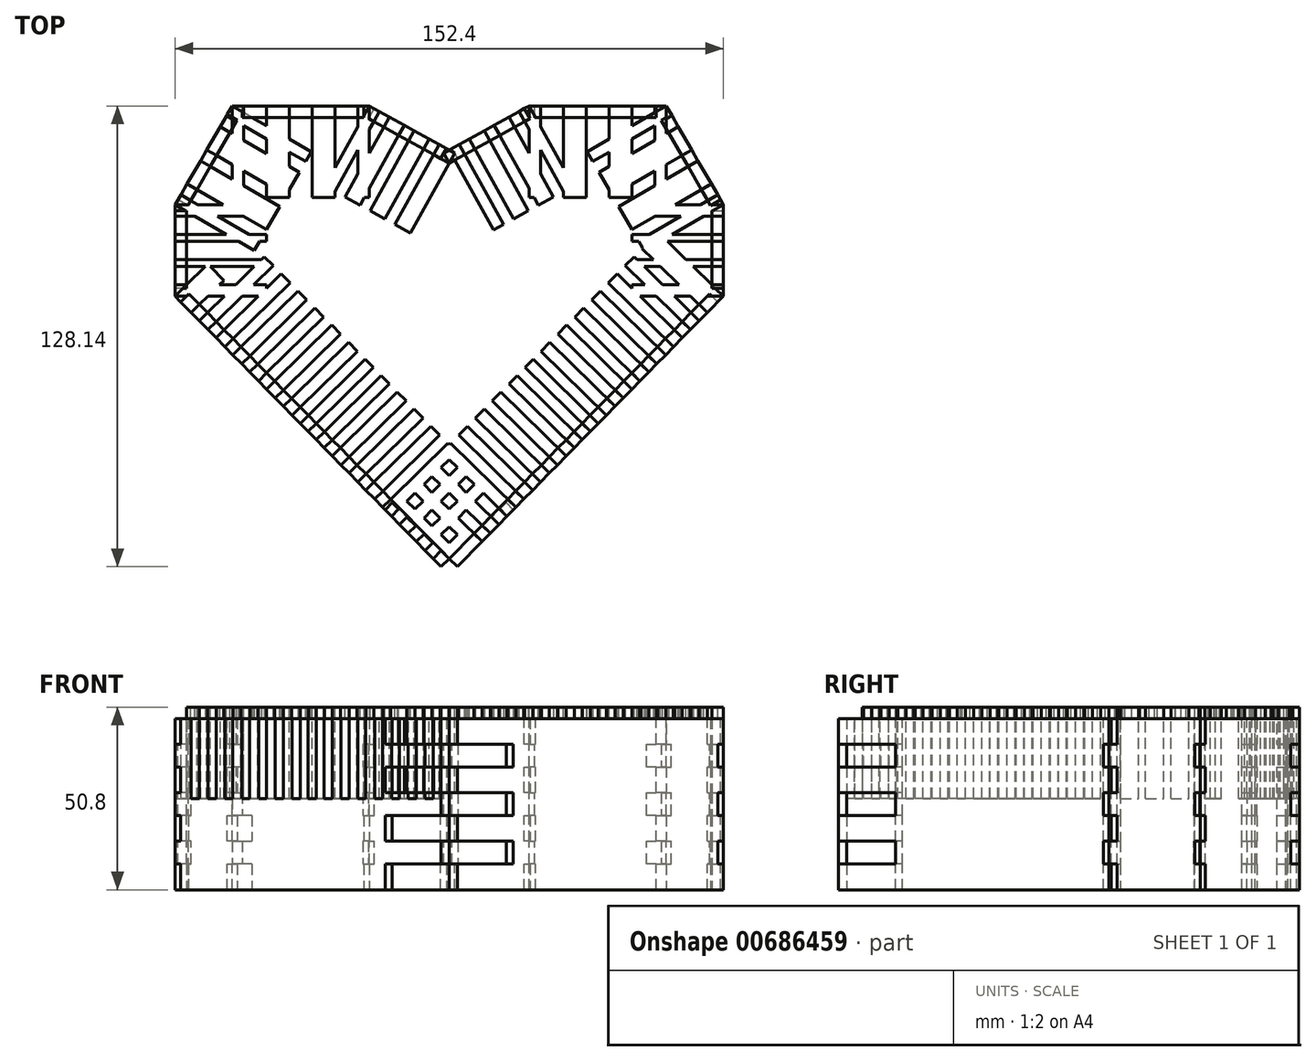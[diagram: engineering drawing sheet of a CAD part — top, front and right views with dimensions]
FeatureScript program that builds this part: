
annotation { "Feature Type Name" : "Feature", "Feature Type Description" : "" }
export const myFeature = defineFeature(function(context is Context, id is Id, definition is map)
    precondition{}
    {
        {
            var Q0;
            Q0=qCreatedBy(makeId("Top.planeOp"),FACE);
            var sketch = newSketch(context, id + "F0", { "sketchPlane" : qUnion([Q0])});
            skLineSegment(sketch, "E0", {"start": v(-76.2, 0) * mm, "end": v(0, -77.54) * mm});
            skLineSegment(sketch, "E1", {"start": v(0, -77.54) * mm, "end": v(76.2, 0) * mm});
            skLineSegment(sketch, "E2", {"start": v(76.2, 0) * mm, "end": v(76.2, 25.4) * mm});
            skLineSegment(sketch, "E3", {"start": v(76.2, 25.4) * mm, "end": v(60.32, 52.9) * mm});
            skLineSegment(sketch, "E4", {"start": v(60.32, 52.9) * mm, "end": v(22.23, 52.9) * mm});
            skLineSegment(sketch, "E5", {"start": v(22.23, 52.9) * mm, "end": v(0, 40.6) * mm});
            skLineSegment(sketch, "E6", {"start": v(0, 40.6) * mm, "end": v(-22.23, 52.9) * mm});
            skLineSegment(sketch, "E7", {"start": v(-22.23, 52.9) * mm, "end": v(-60.33, 52.9) * mm});
            skLineSegment(sketch, "E8", {"start": v(-60.32, 52.9) * mm, "end": v(-76.2, 25.4) * mm});
            skLineSegment(sketch, "E9", {"start": v(-76.2, 25.4) * mm, "end": v(-76.2, 0) * mm});
            skSolve(sketch);
        }
        {
            var Q0;
            Q0=makeQuery(id+"F0.imprint","IMPRINT",FACE,{"disambiguationData":[TD([[makeQuery(id+"F0.imprint","IMPRINT",EDGE,{"derivedFrom":sQuery(id+"F0.wireOp",EDGE,"E0")}),1.0]])]});
            extrude(context, id + "F1", {"entities" : qUnion([Q0]), "depth" : 3.17 * mm, "offsetDistance" : 25.4 * mm});
        }
        {
            var Q0;
            Q0=makeQuery(id+"F1.opExtrude","CAP_FACE",FACE,{"disambiguationData":[OSD([sQuery(id+"F0.wireOp",EDGE,"E0"),sQuery(id+"F0.wireOp",EDGE,"E1"),sQuery(id+"F0.wireOp",EDGE,"E2"),sQuery(id+"F0.wireOp",EDGE,"E3"),sQuery(id+"F0.wireOp",EDGE,"E4"),sQuery(id+"F0.wireOp",EDGE,"E5"),sQuery(id+"F0.wireOp",EDGE,"E6"),sQuery(id+"F0.wireOp",EDGE,"E7"),sQuery(id+"F0.wireOp",EDGE,"E8"),sQuery(id+"F0.wireOp",EDGE,"E9")])],"isStart":false});
            var sketch = newSketch(context, id + "F2", { "sketchPlane" : qUnion([Q0])});
            skLineSegment(sketch, "E10", {"start": v(-22.23, 52.9) * mm, "end": v(-23.76, 50.12) * mm});
            skLineSegment(sketch, "E11", {"start": v(-23.76, 50.12) * mm, "end": v(-1.54, 37.82) * mm});
            skLineSegment(sketch, "E12", {"start": v(-1.54, 37.82) * mm, "end": v(0, 40.6) * mm});
            skLineSegment(sketch, "E13", {"start": v(-76.2, 0) * mm, "end": v(-73.94, 2.23) * mm});
            skLineSegment(sketch, "E14", {"start": v(-73.94, 2.23) * mm, "end": v(2.26, -75.32) * mm});
            skLineSegment(sketch, "E15", {"start": v(2.26, -75.32) * mm, "end": v(0, -77.54) * mm});
            skLineSegment(sketch, "E16", {"start": v(76.2, 25.4) * mm, "end": v(73.03, 25.4) * mm});
            skLineSegment(sketch, "E17", {"start": v(73.03, 25.4) * mm, "end": v(73.03, 0) * mm});
            skLineSegment(sketch, "E18", {"start": v(73.03, 0) * mm, "end": v(76.2, 0) * mm});
            skLineSegment(sketch, "E19", {"start": v(-76.2, 25.4) * mm, "end": v(-73.03, 25.4) * mm});
            skLineSegment(sketch, "E20", {"start": v(-73.03, 25.4) * mm, "end": v(-73.03, 0) * mm});
            skLineSegment(sketch, "E21", {"start": v(-73.03, 0) * mm, "end": v(-76.2, 0) * mm});
            skLineSegment(sketch, "E22", {"start": v(-76.2, 25.4) * mm, "end": v(-73.45, 23.81) * mm});
            skPoint(sketch, "E22.endSnap0", {"position": v(-73.03, 12.7) * mm});
            skLineSegment(sketch, "E23", {"start": v(-73.45, 23.81) * mm, "end": v(-57.58, 51.3) * mm});
            skLineSegment(sketch, "E24", {"start": v(-57.58, 51.3) * mm, "end": v(-60.33, 52.9) * mm});
            skLineSegment(sketch, "E25", {"start": v(-60.33, 52.9) * mm, "end": v(-60.33, 49.72) * mm});
            skLineSegment(sketch, "E26", {"start": v(-60.33, 49.72) * mm, "end": v(-22.23, 49.72) * mm});
            skLineSegment(sketch, "E27", {"start": v(-22.23, 49.72) * mm, "end": v(-22.23, 52.9) * mm});
            skLineSegment(sketch, "E28", {"start": v(0, 40.6) * mm, "end": v(1.54, 37.82) * mm});
            skLineSegment(sketch, "E29", {"start": v(1.54, 37.82) * mm, "end": v(23.76, 50.12) * mm});
            skLineSegment(sketch, "E30", {"start": v(23.76, 50.12) * mm, "end": v(22.23, 52.9) * mm});
            skLineSegment(sketch, "E31", {"start": v(22.23, 52.9) * mm, "end": v(22.23, 49.72) * mm});
            skLineSegment(sketch, "E32", {"start": v(60.32, 49.72) * mm, "end": v(22.23, 49.72) * mm});
            skLineSegment(sketch, "E33", {"start": v(60.32, 49.72) * mm, "end": v(60.32, 52.9) * mm});
            skLineSegment(sketch, "E34", {"start": v(0, -77.54) * mm, "end": v(-2.26, -75.32) * mm});
            skLineSegment(sketch, "E35", {"start": v(-2.26, -75.32) * mm, "end": v(73.94, 2.23) * mm});
            skLineSegment(sketch, "E36", {"start": v(73.94, 2.23) * mm, "end": v(76.2, 0) * mm});
            skLineSegment(sketch, "E37", {"start": v(60.32, 52.9) * mm, "end": v(57.58, 51.3) * mm});
            skLineSegment(sketch, "E38", {"start": v(57.58, 51.3) * mm, "end": v(73.45, 23.81) * mm});
            skLineSegment(sketch, "E39", {"start": v(73.45, 23.81) * mm, "end": v(76.2, 25.4) * mm});
            skLineSegment(sketch, "E40", {"start": v(0, 40.6) * mm, "end": v(1.54, 39.75) * mm});
            skLineSegment(sketch, "E41", {"start": v(1.54, 39.75) * mm, "end": v(0, 36.97) * mm});
            skLineSegment(sketch, "E42", {"start": v(0, 36.97) * mm, "end": v(-1.54, 37.82) * mm});
            skLineSegment(sketch, "E43", {"start": v(1.54, 37.82) * mm, "end": v(0, 36.97) * mm});
            skLineSegment(sketch, "E44", {"start": v(0, 36.97) * mm, "end": v(-1.54, 39.75) * mm});
            skLineSegment(sketch, "E45", {"start": v(-1.54, 39.75) * mm, "end": v(0, 40.6) * mm});
            skSolve(sketch);
        }
        {
            var Q0;
            {var subQ0=sQuery(id+"F2.wireOp",EDGE,"E24");Q0=makeQuery(id+"F2.imprint","IMPRINT",FACE,{"disambiguationData":[TD([[makeQuery(id+"F2.imprint","IMPRINT",EDGE,{"derivedFrom":subQ0}),1.0]])]});}
            var Q1;
            {var subQ5=sQuery(id+"F2.wireOp",EDGE,"E10");Q1=makeQuery(id+"F2.imprint","IMPRINT",FACE,{"disambiguationData":[TD([[makeQuery(id+"F2.imprint","IMPRINT",EDGE,{"derivedFrom":subQ5}),-1.0]])]});}
            var Q2;
            {var subQ0=sQuery(id+"F2.wireOp",EDGE,"E10");Q2=makeQuery(id+"F2.imprint","IMPRINT",FACE,{"disambiguationData":[TD([[makeQuery(id+"F2.imprint","IMPRINT",EDGE,{"derivedFrom":subQ0}),1.0]])]});}
            extrude(context, id + "F3", {"entities" : qUnion([Q0, Q1, Q2]), "oppositeDirection" : true, "depth" : 50.8 * mm, "offsetDistance" : 25.4 * mm});
        }
        {
            var Q0;
            {var subQ5=sQuery(id+"F2.wireOp",EDGE,"E19");Q0=makeQuery(id+"F2.imprint","IMPRINT",FACE,{"disambiguationData":[TD([[makeQuery(id+"F2.imprint","IMPRINT",EDGE,{"derivedFrom":subQ5}),1.0]])]});}
            var Q1;
            {var subQ0=sQuery(id+"F2.wireOp",EDGE,"E19");Q1=makeQuery(id+"F2.imprint","IMPRINT",FACE,{"disambiguationData":[TD([[makeQuery(id+"F2.imprint","IMPRINT",EDGE,{"derivedFrom":subQ0}),-1.0]])]});}
            var Q2;
            {var subQ0=sQuery(id+"F2.wireOp",EDGE,"E24");Q2=makeQuery(id+"F2.imprint","IMPRINT",FACE,{"disambiguationData":[TD([[makeQuery(id+"F2.imprint","IMPRINT",EDGE,{"derivedFrom":subQ0}),1.0]])]});}
            var Q3;
            Q3=makeQuery(id+"F3.opExtrude","CAP_VERTEX",VERTEX,{"disambiguationData":[OSD([sQuery(id+"F2.wireOp",EDGE,"E25"),sQuery(id+"F2.wireOp",EDGE,"E26")])],"isStart":false});
            extrude(context, id + "F4", {"entities" : qUnion([Q0, Q1, Q2]), "endBound" : BoundingType.UP_TO_VERTEX, "oppositeDirection" : true, "depth" : 25.4 * mm, "endBoundEntityVertex" : qUnion([Q3]), "offsetDistance" : 25.4 * mm});
        }
        {
            var Q0;
            {var subQ6=sQuery(id+"F2.wireOp",EDGE,"E13");Q0=makeQuery(id+"F2.imprint","IMPRINT",FACE,{"disambiguationData":[TD([[makeQuery(id+"F2.imprint","IMPRINT",EDGE,{"derivedFrom":subQ6}),1.0]])]});}
            var Q1;
            {var subQ0=sQuery(id+"F2.wireOp",EDGE,"E13");Q1=makeQuery(id+"F2.imprint","IMPRINT",FACE,{"disambiguationData":[TD([[makeQuery(id+"F2.imprint","IMPRINT",EDGE,{"derivedFrom":subQ0}),-1.0]])]});}
            var Q2;
            {var subQ0=sQuery(id+"F2.wireOp",EDGE,"E19");Q2=makeQuery(id+"F2.imprint","IMPRINT",FACE,{"disambiguationData":[TD([[makeQuery(id+"F2.imprint","IMPRINT",EDGE,{"derivedFrom":subQ0}),-1.0]])]});}
            var Q3;
            Q3=makeQuery(id+"F4.opExtrude","CAP_VERTEX",VERTEX,{"disambiguationData":[OSD([sQuery(id+"F0.wireOp",EDGE,"E8"),sQuery(id+"F2.wireOp",EDGE,"E22")])],"isStart":false});
            extrude(context, id + "F5", {"entities" : qUnion([Q0, Q1, Q2]), "endBound" : BoundingType.UP_TO_VERTEX, "oppositeDirection" : true, "depth" : 25.4 * mm, "endBoundEntityVertex" : qUnion([Q3]), "offsetDistance" : 25.4 * mm});
        }
        {
            var Q0;
            {var subQ0=sQuery(id+"F2.wireOp",EDGE,"E21");Q0=makeQuery(id+"F2.imprint","IMPRINT",FACE,{"disambiguationData":[TD([[makeQuery(id+"F2.imprint","IMPRINT",EDGE,{"derivedFrom":subQ0}),1.0]])]});}
            var Q1;
            {var subQ0=sQuery(id+"F2.wireOp",EDGE,"E13");Q1=makeQuery(id+"F2.imprint","IMPRINT",FACE,{"disambiguationData":[TD([[makeQuery(id+"F2.imprint","IMPRINT",EDGE,{"derivedFrom":subQ0}),-1.0]])]});}
            var Q2;
            {var subQ0=sQuery(id+"F2.wireOp",EDGE,"E35");var subQ1=sQuery(id+"F2.wireOp",EDGE,"E14");var subQ2=makeQuery(id+"F2.imprint","INTERSECT",VERTEX,{"derivedFrom":[subQ1,subQ0]});Q2=makeQuery(id+"F2.imprint","IMPRINT",FACE,{"disambiguationData":[TD([[makeQuery(id+"F2.imprint","IMPRINT",EDGE,{"disambiguationData":[TD([[subQ2,-1.0]])],"derivedFrom":subQ1}),-1.0]])]});}
            var Q3;
            Q3=makeQuery(id+"F5.opExtrude","CAP_VERTEX",VERTEX,{"disambiguationData":[OSD([sQuery(id+"F0.wireOp",EDGE,"E9"),sQuery(id+"F2.wireOp",EDGE,"E21")])],"isStart":false});
            extrude(context, id + "F6", {"entities" : qUnion([Q0, Q1, Q2]), "endBound" : BoundingType.UP_TO_VERTEX, "oppositeDirection" : true, "depth" : 25.4 * mm, "endBoundEntityVertex" : qUnion([Q3]), "offsetDistance" : 25.4 * mm});
        }
        {
            var Q0;
            {var subQ0=sQuery(id+"F2.wireOp",EDGE,"E18");Q0=makeQuery(id+"F2.imprint","IMPRINT",FACE,{"disambiguationData":[TD([[makeQuery(id+"F2.imprint","IMPRINT",EDGE,{"derivedFrom":subQ0}),-1.0]])]});}
            var Q1;
            {var subQ0=sQuery(id+"F2.wireOp",EDGE,"E35");var subQ1=sQuery(id+"F2.wireOp",EDGE,"E14");var subQ2=makeQuery(id+"F2.imprint","INTERSECT",VERTEX,{"derivedFrom":[subQ1,subQ0]});Q1=makeQuery(id+"F2.imprint","IMPRINT",FACE,{"disambiguationData":[TD([[makeQuery(id+"F2.imprint","IMPRINT",EDGE,{"disambiguationData":[TD([[subQ2,-1.0]])],"derivedFrom":subQ1}),-1.0]])]});}
            var Q2;
            {var subQ0=sQuery(id+"F2.wireOp",EDGE,"E18");Q2=makeQuery(id+"F2.imprint","IMPRINT",FACE,{"disambiguationData":[TD([[makeQuery(id+"F2.imprint","IMPRINT",EDGE,{"derivedFrom":subQ0}),1.0]])]});}
            var Q3;
            Q3=makeQuery(id+"F6.opExtrude","CAP_VERTEX",VERTEX,{"disambiguationData":[OSD([sQuery(id+"F0.wireOp",EDGE,"E0"),sQuery(id+"F0.wireOp",EDGE,"E1")])],"isStart":false});
            extrude(context, id + "F7", {"entities" : qUnion([Q0, Q1, Q2]), "endBound" : BoundingType.UP_TO_VERTEX, "oppositeDirection" : true, "depth" : 25.4 * mm, "endBoundEntityVertex" : qUnion([Q3]), "offsetDistance" : 25.4 * mm});
        }
        {
            var Q0;
            {var subQ0=sQuery(id+"F2.wireOp",EDGE,"E36");Q0=makeQuery(id+"F2.imprint","IMPRINT",FACE,{"disambiguationData":[TD([[makeQuery(id+"F2.imprint","IMPRINT",EDGE,{"derivedFrom":subQ0}),1.0]])]});}
            var Q1;
            {var subQ0=sQuery(id+"F2.wireOp",EDGE,"E16");Q1=makeQuery(id+"F2.imprint","IMPRINT",FACE,{"disambiguationData":[TD([[makeQuery(id+"F2.imprint","IMPRINT",EDGE,{"derivedFrom":subQ0}),1.0]])]});}
            var Q2;
            {var subQ0=sQuery(id+"F2.wireOp",EDGE,"E18");Q2=makeQuery(id+"F2.imprint","IMPRINT",FACE,{"disambiguationData":[TD([[makeQuery(id+"F2.imprint","IMPRINT",EDGE,{"derivedFrom":subQ0}),1.0]])]});}
            var Q3;
            Q3=makeQuery(id+"F7.opExtrude","CAP_VERTEX",VERTEX,{"disambiguationData":[OSD([sQuery(id+"F2.wireOp",EDGE,"E35"),sQuery(id+"F2.wireOp",EDGE,"E36")])],"isStart":false});
            extrude(context, id + "F8", {"entities" : qUnion([Q0, Q1, Q2]), "endBound" : BoundingType.UP_TO_VERTEX, "oppositeDirection" : true, "depth" : 25.4 * mm, "endBoundEntityVertex" : qUnion([Q3]), "offsetDistance" : 25.4 * mm});
        }
        {
            var Q0;
            {var subQ2=sQuery(id+"F2.wireOp",EDGE,"E16");Q0=makeQuery(id+"F2.imprint","IMPRINT",FACE,{"disambiguationData":[TD([[makeQuery(id+"F2.imprint","IMPRINT",EDGE,{"derivedFrom":subQ2}),-1.0]])]});}
            var Q1;
            {var subQ0=sQuery(id+"F2.wireOp",EDGE,"E16");Q1=makeQuery(id+"F2.imprint","IMPRINT",FACE,{"disambiguationData":[TD([[makeQuery(id+"F2.imprint","IMPRINT",EDGE,{"derivedFrom":subQ0}),1.0]])]});}
            var Q2;
            {var subQ0=sQuery(id+"F2.wireOp",EDGE,"E33");Q2=makeQuery(id+"F2.imprint","IMPRINT",FACE,{"disambiguationData":[TD([[makeQuery(id+"F2.imprint","IMPRINT",EDGE,{"derivedFrom":subQ0}),1.0]])]});}
            var Q3;
            Q3=makeQuery(id+"F8.opExtrude","CAP_VERTEX",VERTEX,{"disambiguationData":[OSD([sQuery(id+"F2.wireOp",EDGE,"E16"),sQuery(id+"F2.wireOp",EDGE,"E17")])],"isStart":false});
            extrude(context, id + "F9", {"entities" : qUnion([Q0, Q1, Q2]), "endBound" : BoundingType.UP_TO_VERTEX, "oppositeDirection" : true, "depth" : 25.4 * mm, "endBoundEntityVertex" : qUnion([Q3]), "offsetDistance" : 25.4 * mm});
        }
        {
            var Q0;
            {var subQ6=sQuery(id+"F2.wireOp",EDGE,"E30");Q0=makeQuery(id+"F2.imprint","IMPRINT",FACE,{"disambiguationData":[TD([[makeQuery(id+"F2.imprint","IMPRINT",EDGE,{"derivedFrom":subQ6}),-1.0]])]});}
            var Q1;
            {var subQ0=sQuery(id+"F2.wireOp",EDGE,"E30");Q1=makeQuery(id+"F2.imprint","IMPRINT",FACE,{"disambiguationData":[TD([[makeQuery(id+"F2.imprint","IMPRINT",EDGE,{"derivedFrom":subQ0}),1.0]])]});}
            var Q2;
            {var subQ0=sQuery(id+"F2.wireOp",EDGE,"E33");Q2=makeQuery(id+"F2.imprint","IMPRINT",FACE,{"disambiguationData":[TD([[makeQuery(id+"F2.imprint","IMPRINT",EDGE,{"derivedFrom":subQ0}),1.0]])]});}
            var Q3;
            Q3=makeQuery(id+"F9.opExtrude","CAP_VERTEX",VERTEX,{"disambiguationData":[OSD([sQuery(id+"F0.wireOp",EDGE,"E3"),sQuery(id+"F2.wireOp",EDGE,"E37")])],"isStart":false});
            extrude(context, id + "F10", {"entities" : qUnion([Q0, Q1, Q2]), "endBound" : BoundingType.UP_TO_VERTEX, "oppositeDirection" : true, "depth" : 25.4 * mm, "endBoundEntityVertex" : qUnion([Q3]), "offsetDistance" : 25.4 * mm});
        }
        {
            var Q0;
            {var subQ4=sQuery(id+"F2.wireOp",EDGE,"E28");Q0=makeQuery(id+"F2.imprint","IMPRINT",FACE,{"disambiguationData":[TD([[makeQuery(id+"F2.imprint","IMPRINT",EDGE,{"derivedFrom":subQ4}),1.0]])]});}
            var Q1;
            {var subQ0=sQuery(id+"F2.wireOp",EDGE,"E30");Q1=makeQuery(id+"F2.imprint","IMPRINT",FACE,{"disambiguationData":[TD([[makeQuery(id+"F2.imprint","IMPRINT",EDGE,{"derivedFrom":subQ0}),1.0]])]});}
            var Q2;
            {var subQ0=sQuery(id+"F2.wireOp",EDGE,"E28");var subQ5=sQuery(id+"F2.wireOp",EDGE,"E41");var subQ7=makeQuery(id+"F2.imprint","INTERSECT",VERTEX,{"derivedFrom":[subQ0,subQ5]});Q2=makeQuery(id+"F2.imprint","IMPRINT",FACE,{"disambiguationData":[TD([[makeQuery(id+"F2.imprint","IMPRINT",EDGE,{"disambiguationData":[TD([[subQ7,-1.0]])],"derivedFrom":subQ5}),-1.0]])]});}
            var Q3;
            {var subQ0=sQuery(id+"F2.wireOp",EDGE,"E45");Q3=makeQuery(id+"F2.imprint","IMPRINT",FACE,{"disambiguationData":[TD([[makeQuery(id+"F2.imprint","IMPRINT",EDGE,{"derivedFrom":subQ0}),-1.0]])]});}
            var Q4;
            {var subQ0=sQuery(id+"F2.wireOp",EDGE,"E43");Q4=makeQuery(id+"F2.imprint","IMPRINT",FACE,{"disambiguationData":[TD([[makeQuery(id+"F2.imprint","IMPRINT",EDGE,{"derivedFrom":subQ0}),-1.0]])]});}
            var Q5;
            {var subQ1=sQuery(id+"F2.wireOp",EDGE,"E31");Q5=makeQuery(id+"F2.imprint","IMPRINT",FACE,{"disambiguationData":[TD([[makeQuery(id+"F2.imprint","IMPRINT",EDGE,{"derivedFrom":subQ1}),-1.0]])]});}
            var Q6;
            Q6=makeQuery(id+"F10.opExtrude","CAP_VERTEX",VERTEX,{"disambiguationData":[OSD([sQuery(id+"F2.wireOp",EDGE,"E31"),sQuery(id+"F2.wireOp",EDGE,"E32")])],"isStart":false});
            extrude(context, id + "F11", {"entities" : qUnion([Q0, Q1, Q2, Q3, Q4, Q5]), "endBound" : BoundingType.UP_TO_VERTEX, "oppositeDirection" : true, "depth" : 25.4 * mm, "endBoundEntityVertex" : qUnion([Q6]), "offsetDistance" : 25.4 * mm});
        }
        {
            var Q0;
            {var subQ4=sQuery(id+"F2.wireOp",EDGE,"E12");Q0=makeQuery(id+"F2.imprint","IMPRINT",FACE,{"disambiguationData":[TD([[makeQuery(id+"F2.imprint","IMPRINT",EDGE,{"derivedFrom":subQ4}),1.0]])]});}
            var Q1;
            {var subQ0=sQuery(id+"F2.wireOp",EDGE,"E10");Q1=makeQuery(id+"F2.imprint","IMPRINT",FACE,{"disambiguationData":[TD([[makeQuery(id+"F2.imprint","IMPRINT",EDGE,{"derivedFrom":subQ0}),1.0]])]});}
            var Q2;
            {var subQ0=sQuery(id+"F2.wireOp",EDGE,"E27");Q2=makeQuery(id+"F2.imprint","IMPRINT",FACE,{"disambiguationData":[TD([[makeQuery(id+"F2.imprint","IMPRINT",EDGE,{"derivedFrom":subQ0}),-1.0]])]});}
            var Q3;
            {var subQ0=sQuery(id+"F2.wireOp",EDGE,"E28");var subQ5=sQuery(id+"F2.wireOp",EDGE,"E41");var subQ7=makeQuery(id+"F2.imprint","INTERSECT",VERTEX,{"derivedFrom":[subQ0,subQ5]});Q3=makeQuery(id+"F2.imprint","IMPRINT",FACE,{"disambiguationData":[TD([[makeQuery(id+"F2.imprint","IMPRINT",EDGE,{"disambiguationData":[TD([[subQ7,-1.0]])],"derivedFrom":subQ5}),-1.0]])]});}
            var Q4;
            {var subQ0=sQuery(id+"F2.wireOp",EDGE,"E42");Q4=makeQuery(id+"F2.imprint","IMPRINT",FACE,{"disambiguationData":[TD([[makeQuery(id+"F2.imprint","IMPRINT",EDGE,{"derivedFrom":subQ0}),-1.0]])]});}
            var Q5;
            {var subQ0=sQuery(id+"F2.wireOp",EDGE,"E40");Q5=makeQuery(id+"F2.imprint","IMPRINT",FACE,{"disambiguationData":[TD([[makeQuery(id+"F2.imprint","IMPRINT",EDGE,{"derivedFrom":subQ0}),-1.0]])]});}
            var Q6;
            Q6=makeQuery(id+"F11.opExtrude","CAP_VERTEX",VERTEX,{"disambiguationData":[OSD([sQuery(id+"F0.wireOp",EDGE,"E5"),sQuery(id+"F2.wireOp",EDGE,"E44"),sQuery(id+"F2.wireOp",EDGE,"E45")])],"isStart":false});
            extrude(context, id + "F12", {"entities" : qUnion([Q0, Q1, Q2, Q3, Q4, Q5]), "endBound" : BoundingType.UP_TO_VERTEX, "oppositeDirection" : true, "depth" : 25.4 * mm, "endBoundEntityVertex" : qUnion([Q6]), "offsetDistance" : 25.4 * mm});
        }
        {
            var Q0;
            Q0=makeQuery(id+"F1.opExtrude","CAP_FACE",FACE,{"disambiguationData":[OSD([sQuery(id+"F0.wireOp",EDGE,"E0"),sQuery(id+"F0.wireOp",EDGE,"E1"),sQuery(id+"F0.wireOp",EDGE,"E2"),sQuery(id+"F0.wireOp",EDGE,"E3"),sQuery(id+"F0.wireOp",EDGE,"E4"),sQuery(id+"F0.wireOp",EDGE,"E5"),sQuery(id+"F0.wireOp",EDGE,"E6"),sQuery(id+"F0.wireOp",EDGE,"E7"),sQuery(id+"F0.wireOp",EDGE,"E8"),sQuery(id+"F0.wireOp",EDGE,"E9")])],"isStart":false});
            var sketch = newSketch(context, id + "F13", { "sketchPlane" : qUnion([Q0])});
            skCircle(sketch, "E46", {"center": v(-22.23, 52.9) * mm, "radius": 3.18 * mm});
            skCircle(sketch, "E47", {"center": v(0, 40.6) * mm, "radius": 3.18 * mm});
            skLineSegment(sketch, "E48", {"start": v(-19.45, 51.36) * mm, "end": v(-20.98, 48.58) * mm});
            skLineSegment(sketch, "E49", {"start": v(-20.98, 48.58) * mm, "end": v(-18.2, 47.04) * mm});
            skLineSegment(sketch, "E50", {"start": v(-18.2, 47.04) * mm, "end": v(-16.67, 49.82) * mm});
            skLineSegment(sketch, "E51", {"start": v(-12.5, 47.52) * mm, "end": v(-14.04, 44.74) * mm});
            skLineSegment(sketch, "E52", {"start": v(-14.04, 44.74) * mm, "end": v(-11.26, 43.2) * mm});
            skLineSegment(sketch, "E53", {"start": v(-11.26, 43.2) * mm, "end": v(-9.72, 45.98) * mm});
            skLineSegment(sketch, "E54", {"start": v(-5.56, 43.67) * mm, "end": v(-7.1, 40.9) * mm});
            skLineSegment(sketch, "E55", {"start": v(-7.1, 40.9) * mm, "end": v(-4.32, 39.36) * mm});
            skLineSegment(sketch, "E56", {"start": v(-4.32, 39.36) * mm, "end": v(-2.78, 42.14) * mm});
            skLineSegment(sketch, "E57", {"start": v(-17.44, 48.43) * mm, "end": v(-13.27, 46.13) * mm, "construction": true});
            skLineSegment(sketch, "E58", {"start": v(-10.5, 44.6) * mm, "end": v(-6.32, 42.28) * mm, "construction": true});
            skSolve(sketch);
        }
        {
            var Q0;
            {var subQ0=sQuery(id+"F13.wireOp",EDGE,"E48");Q0=makeQuery(id+"F13.imprint","IMPRINT",FACE,{"disambiguationData":[TD([[makeQuery(id+"F13.imprint","IMPRINT",EDGE,{"derivedFrom":subQ0}),1.0]])]});}
            var Q1;
            {var subQ0=sQuery(id+"F13.wireOp",EDGE,"E51");Q1=makeQuery(id+"F13.imprint","IMPRINT",FACE,{"disambiguationData":[TD([[makeQuery(id+"F13.imprint","IMPRINT",EDGE,{"derivedFrom":subQ0}),1.0]])]});}
            var Q2;
            {var subQ0=sQuery(id+"F13.wireOp",EDGE,"E54");Q2=makeQuery(id+"F13.imprint","IMPRINT",FACE,{"disambiguationData":[TD([[makeQuery(id+"F13.imprint","IMPRINT",EDGE,{"derivedFrom":subQ0}),1.0]])]});}
            extrude(context, id + "F14", {"entities" : qUnion([Q0, Q1, Q2]), "operationType" : NewBodyOperationType.REMOVE, "oppositeDirection" : true, "depth" : 25.4 * mm, "offsetDistance" : 25.4 * mm});
        }
        {
            var Q0;
            Q0=makeQuery(id+"F1.opExtrude","CAP_FACE",FACE,{"disambiguationData":[OSD([sQuery(id+"F0.wireOp",EDGE,"E0"),sQuery(id+"F0.wireOp",EDGE,"E1"),sQuery(id+"F0.wireOp",EDGE,"E2"),sQuery(id+"F0.wireOp",EDGE,"E3"),sQuery(id+"F0.wireOp",EDGE,"E4"),sQuery(id+"F0.wireOp",EDGE,"E5"),sQuery(id+"F0.wireOp",EDGE,"E6"),sQuery(id+"F0.wireOp",EDGE,"E7"),sQuery(id+"F0.wireOp",EDGE,"E8"),sQuery(id+"F0.wireOp",EDGE,"E9")])],"isStart":false});
            var sketch = newSketch(context, id + "F15", { "sketchPlane" : qUnion([Q0])});
            skCircle(sketch, "E59", {"center": v(-60.33, 52.9) * mm, "radius": 3.18 * mm});
            skCircle(sketch, "E60", {"center": v(-22.23, 52.9) * mm, "radius": 3.18 * mm});
            skLineSegment(sketch, "E61", {"start": v(-57.15, 52.9) * mm, "end": v(-57.15, 49.72) * mm});
            skLineSegment(sketch, "E62", {"start": v(-57.15, 49.72) * mm, "end": v(-50.8, 49.72) * mm});
            skLineSegment(sketch, "E63", {"start": v(-50.8, 49.72) * mm, "end": v(-50.8, 52.9) * mm});
            skLineSegment(sketch, "E64", {"start": v(-44.45, 52.9) * mm, "end": v(-44.45, 49.72) * mm});
            skLineSegment(sketch, "E65", {"start": v(-44.45, 49.72) * mm, "end": v(-38.1, 49.72) * mm});
            skLineSegment(sketch, "E66", {"start": v(-38.1, 49.72) * mm, "end": v(-38.1, 52.9) * mm});
            skLineSegment(sketch, "E67", {"start": v(-31.75, 52.9) * mm, "end": v(-31.75, 49.72) * mm});
            skLineSegment(sketch, "E68", {"start": v(-31.75, 49.72) * mm, "end": v(-25.4, 49.72) * mm});
            skLineSegment(sketch, "E69", {"start": v(-25.4, 49.72) * mm, "end": v(-25.4, 52.9) * mm});
            skLineSegment(sketch, "E70", {"start": v(-50.8, 51.3) * mm, "end": v(-44.45, 51.3) * mm, "construction": true});
            skPoint(sketch, "E70.startSnap0", {"position": v(-50.8, 51.3) * mm});
            skLineSegment(sketch, "E71", {"start": v(-38.1, 51.3) * mm, "end": v(-31.75, 51.3) * mm, "construction": true});
            skSolve(sketch);
        }
        {
            var Q0;
            {var subQ0=sQuery(id+"F15.wireOp",EDGE,"E61");Q0=makeQuery(id+"F15.imprint","IMPRINT",FACE,{"disambiguationData":[TD([[makeQuery(id+"F15.imprint","IMPRINT",EDGE,{"derivedFrom":subQ0}),1.0]])]});}
            var Q1;
            {var subQ0=sQuery(id+"F15.wireOp",EDGE,"E64");Q1=makeQuery(id+"F15.imprint","IMPRINT",FACE,{"disambiguationData":[TD([[makeQuery(id+"F15.imprint","IMPRINT",EDGE,{"derivedFrom":subQ0}),1.0]])]});}
            var Q2;
            {var subQ0=sQuery(id+"F15.wireOp",EDGE,"E67");Q2=makeQuery(id+"F15.imprint","IMPRINT",FACE,{"disambiguationData":[TD([[makeQuery(id+"F15.imprint","IMPRINT",EDGE,{"derivedFrom":subQ0}),1.0]])]});}
            extrude(context, id + "F16", {"entities" : qUnion([Q0, Q1, Q2]), "operationType" : NewBodyOperationType.REMOVE, "oppositeDirection" : true, "depth" : 25.4 * mm, "offsetDistance" : 25.4 * mm});
        }
        {
            var Q0;
            Q0=makeQuery(id+"F1.opExtrude","CAP_FACE",FACE,{"disambiguationData":[OSD([sQuery(id+"F0.wireOp",EDGE,"E0"),sQuery(id+"F0.wireOp",EDGE,"E1"),sQuery(id+"F0.wireOp",EDGE,"E2"),sQuery(id+"F0.wireOp",EDGE,"E3"),sQuery(id+"F0.wireOp",EDGE,"E4"),sQuery(id+"F0.wireOp",EDGE,"E5"),sQuery(id+"F0.wireOp",EDGE,"E6"),sQuery(id+"F0.wireOp",EDGE,"E7"),sQuery(id+"F0.wireOp",EDGE,"E8"),sQuery(id+"F0.wireOp",EDGE,"E9")])],"isStart":false});
            var sketch = newSketch(context, id + "F17", { "sketchPlane" : qUnion([Q0])});
            skCircle(sketch, "E72", {"center": v(-76.2, 25.4) * mm, "radius": 3.18 * mm});
            skCircle(sketch, "E73", {"center": v(-60.33, 52.9) * mm, "radius": 3.18 * mm});
            skLineSegment(sketch, "E74", {"start": v(-74.61, 28.15) * mm, "end": v(-71.86, 26.56) * mm});
            skLineSegment(sketch, "E75", {"start": v(-71.86, 26.56) * mm, "end": v(-70.1, 29.6) * mm});
            skLineSegment(sketch, "E76", {"start": v(-70.1, 29.6) * mm, "end": v(-72.86, 31.19) * mm});
            skLineSegment(sketch, "E77", {"start": v(-69.14, 37.63) * mm, "end": v(-66.4, 36.04) * mm});
            skLineSegment(sketch, "E78", {"start": v(-66.4, 36.04) * mm, "end": v(-64.64, 39.08) * mm});
            skLineSegment(sketch, "E79", {"start": v(-64.64, 39.08) * mm, "end": v(-67.39, 40.67) * mm});
            skLineSegment(sketch, "E80", {"start": v(-63.67, 47.1) * mm, "end": v(-60.92, 45.52) * mm});
            skLineSegment(sketch, "E81", {"start": v(-60.92, 45.52) * mm, "end": v(-59.16, 48.56) * mm});
            skLineSegment(sketch, "E82", {"start": v(-59.16, 48.56) * mm, "end": v(-61.91, 50.15) * mm});
            skLineSegment(sketch, "E83", {"start": v(-71.48, 30.4) * mm, "end": v(-67.76, 36.83) * mm, "construction": true});
            skLineSegment(sketch, "E84", {"start": v(-66.01, 39.87) * mm, "end": v(-62.3, 46.31) * mm, "construction": true});
            skSolve(sketch);
        }
        {
            var Q0;
            {var subQ0=sQuery(id+"F17.wireOp",EDGE,"E74");Q0=makeQuery(id+"F17.imprint","IMPRINT",FACE,{"disambiguationData":[TD([[makeQuery(id+"F17.imprint","IMPRINT",EDGE,{"derivedFrom":subQ0}),1.0]])]});}
            var Q1;
            {var subQ0=sQuery(id+"F17.wireOp",EDGE,"E77");Q1=makeQuery(id+"F17.imprint","IMPRINT",FACE,{"disambiguationData":[TD([[makeQuery(id+"F17.imprint","IMPRINT",EDGE,{"derivedFrom":subQ0}),1.0]])]});}
            var Q2;
            {var subQ0=sQuery(id+"F17.wireOp",EDGE,"E80");Q2=makeQuery(id+"F17.imprint","IMPRINT",FACE,{"disambiguationData":[TD([[makeQuery(id+"F17.imprint","IMPRINT",EDGE,{"derivedFrom":subQ0}),1.0]])]});}
            extrude(context, id + "F18", {"entities" : qUnion([Q0, Q1, Q2]), "operationType" : NewBodyOperationType.REMOVE, "oppositeDirection" : true, "depth" : 25.4 * mm, "offsetDistance" : 25.4 * mm});
        }
        {
            var Q0;
            Q0=makeQuery(id+"F1.opExtrude","CAP_FACE",FACE,{"disambiguationData":[OSD([sQuery(id+"F0.wireOp",EDGE,"E0"),sQuery(id+"F0.wireOp",EDGE,"E1"),sQuery(id+"F0.wireOp",EDGE,"E2"),sQuery(id+"F0.wireOp",EDGE,"E3"),sQuery(id+"F0.wireOp",EDGE,"E4"),sQuery(id+"F0.wireOp",EDGE,"E5"),sQuery(id+"F0.wireOp",EDGE,"E6"),sQuery(id+"F0.wireOp",EDGE,"E7"),sQuery(id+"F0.wireOp",EDGE,"E8"),sQuery(id+"F0.wireOp",EDGE,"E9")])],"isStart":false});
            var sketch = newSketch(context, id + "F19", { "sketchPlane" : qUnion([Q0])});
            skCircle(sketch, "E85", {"center": v(-76.2, 25.4) * mm, "radius": 3.18 * mm});
            skCircle(sketch, "E86", {"center": v(-76.2, 0) * mm, "radius": 3.18 * mm});
            skLineSegment(sketch, "E87", {"start": v(-76.2, 3.18) * mm, "end": v(-73.03, 3.18) * mm});
            skLineSegment(sketch, "E88", {"start": v(-73.03, 3.18) * mm, "end": v(-73.03, 8.22) * mm});
            skLineSegment(sketch, "E89", {"start": v(-73.03, 8.22) * mm, "end": v(-76.2, 8.22) * mm});
            skLineSegment(sketch, "E90", {"start": v(-76.2, 10.18) * mm, "end": v(-73.03, 10.18) * mm});
            skLineSegment(sketch, "E91", {"start": v(-73.03, 10.18) * mm, "end": v(-73.03, 15.22) * mm});
            skLineSegment(sketch, "E92", {"start": v(-73.03, 15.22) * mm, "end": v(-76.2, 15.22) * mm});
            skLineSegment(sketch, "E93", {"start": v(-76.2, 17.18) * mm, "end": v(-73.03, 17.18) * mm});
            skLineSegment(sketch, "E94", {"start": v(-73.03, 17.18) * mm, "end": v(-73.03, 22.22) * mm});
            skLineSegment(sketch, "E95", {"start": v(-73.03, 22.22) * mm, "end": v(-76.2, 22.22) * mm});
            skLineSegment(sketch, "E96", {"start": v(-74.61, 8.22) * mm, "end": v(-74.61, 10.18) * mm, "construction": true});
            skLineSegment(sketch, "E97", {"start": v(-74.61, 15.22) * mm, "end": v(-74.61, 17.18) * mm, "construction": true});
            skSolve(sketch);
        }
        {
            var Q0;
            {var subQ0=sQuery(id+"F19.wireOp",EDGE,"E87");Q0=makeQuery(id+"F19.imprint","IMPRINT",FACE,{"disambiguationData":[TD([[makeQuery(id+"F19.imprint","IMPRINT",EDGE,{"derivedFrom":subQ0}),1.0]])]});}
            var Q1;
            {var subQ0=sQuery(id+"F19.wireOp",EDGE,"E90");Q1=makeQuery(id+"F19.imprint","IMPRINT",FACE,{"disambiguationData":[TD([[makeQuery(id+"F19.imprint","IMPRINT",EDGE,{"derivedFrom":subQ0}),1.0]])]});}
            var Q2;
            {var subQ0=sQuery(id+"F19.wireOp",EDGE,"E93");Q2=makeQuery(id+"F19.imprint","IMPRINT",FACE,{"disambiguationData":[TD([[makeQuery(id+"F19.imprint","IMPRINT",EDGE,{"derivedFrom":subQ0}),1.0]])]});}
            extrude(context, id + "F20", {"entities" : qUnion([Q0, Q1, Q2]), "operationType" : NewBodyOperationType.REMOVE, "oppositeDirection" : true, "depth" : 25.4 * mm, "offsetDistance" : 25.4 * mm});
        }
        {
            var Q0;
            {var subQ8=sQuery(id+"F13.wireOp",EDGE,"E48");Q0=makeQuery(id+"F13.imprint","IMPRINT",FACE,{"disambiguationData":[TD([[makeQuery(id+"F13.imprint","IMPRINT",EDGE,{"derivedFrom":subQ8}),-1.0]])]});}
            var sketch = newSketch(context, id + "F21", { "sketchPlane" : qUnion([Q0])});
            skCircle(sketch, "E98", {"center": v(-76.2, 0) * mm, "radius": 3.18 * mm});
            skCircle(sketch, "E99", {"center": v(0, -77.54) * mm, "radius": 3.18 * mm});
            skLineSegment(sketch, "E100", {"start": v(-76.2, 0) * mm, "end": v(0, -77.54) * mm});
            skLineSegment(sketch, "E101", {"start": v(-38.1, -38.77) * mm, "end": v(-24.6, -25.5) * mm, "construction": true});
            skLineSegment(sketch, "E102", {"start": v(-39.21, -37.64) * mm, "end": v(-36.95, -35.41) * mm});
            skLineSegment(sketch, "E103", {"start": v(-36.95, -35.41) * mm, "end": v(-34.72, -37.68) * mm});
            skLineSegment(sketch, "E104", {"start": v(-34.72, -37.68) * mm, "end": v(-36.99, -39.9) * mm});
            skLineSegment(sketch, "E105", {"start": v(-34.76, -42.17) * mm, "end": v(-32.5, -39.94) * mm});
            skLineSegment(sketch, "E106", {"start": v(-32.5, -39.94) * mm, "end": v(-30.27, -42.2) * mm});
            skLineSegment(sketch, "E107", {"start": v(-30.27, -42.2) * mm, "end": v(-32.54, -44.43) * mm});
            skLineSegment(sketch, "E108.1.0.0", {"start": v(-30.09, -46.93) * mm, "end": v(-27.82, -44.7) * mm});
            skLineSegment(sketch, "E108.1.0.1", {"start": v(-27.82, -44.7) * mm, "end": v(-25.6, -46.97) * mm});
            skLineSegment(sketch, "E108.1.0.2", {"start": v(-25.6, -46.97) * mm, "end": v(-27.86, -49.2) * mm});
            skLineSegment(sketch, "E108.2.0.0", {"start": v(-25.41, -51.68) * mm, "end": v(-23.15, -49.46) * mm});
            skLineSegment(sketch, "E108.2.0.1", {"start": v(-23.15, -49.46) * mm, "end": v(-20.92, -51.72) * mm});
            skLineSegment(sketch, "E108.2.0.2", {"start": v(-20.92, -51.72) * mm, "end": v(-23.18, -53.95) * mm});
            skLineSegment(sketch, "E108.direction1", {"start": v(-34.76, -42.17) * mm, "end": v(-30.09, -46.93) * mm, "construction": true});
            skLineSegment(sketch, "E109.0.3.0", {"start": v(-20.73, -56.44) * mm, "end": v(-18.47, -54.22) * mm});
            skLineSegment(sketch, "E109.3.3.0", {"start": v(-18.47, -54.22) * mm, "end": v(-16.24, -56.48) * mm});
            skLineSegment(sketch, "E109.6.3.0", {"start": v(-16.24, -56.48) * mm, "end": v(-18.5, -58.7) * mm});
            skLineSegment(sketch, "E109.0.4.0", {"start": v(-16.06, -61.2) * mm, "end": v(-13.8, -58.98) * mm});
            skLineSegment(sketch, "E109.3.4.0", {"start": v(-13.8, -58.98) * mm, "end": v(-11.57, -61.24) * mm});
            skLineSegment(sketch, "E109.6.4.0", {"start": v(-11.57, -61.24) * mm, "end": v(-13.83, -63.47) * mm});
            skLineSegment(sketch, "E109.0.5.0", {"start": v(-11.38, -65.96) * mm, "end": v(-9.12, -63.73) * mm});
            skLineSegment(sketch, "E109.3.5.0", {"start": v(-9.12, -63.73) * mm, "end": v(-6.9, -66) * mm});
            skLineSegment(sketch, "E109.6.5.0", {"start": v(-6.9, -66) * mm, "end": v(-9.16, -68.22) * mm});
            skLineSegment(sketch, "E109.0.6.0", {"start": v(-6.7, -70.72) * mm, "end": v(-4.44, -68.5) * mm});
            skLineSegment(sketch, "E109.3.6.0", {"start": v(-4.44, -68.5) * mm, "end": v(-2.22, -70.76) * mm});
            skLineSegment(sketch, "E109.6.6.0", {"start": v(-2.22, -70.76) * mm, "end": v(-4.48, -72.98) * mm});
            skLineSegment(sketch, "E110.MirrorCS", {"start": v(-41.44, -35.37) * mm, "end": v(-39.17, -33.15) * mm});
            skLineSegment(sketch, "E111.MirrorCS", {"start": v(-39.17, -33.15) * mm, "end": v(-41.4, -30.88) * mm});
            skLineSegment(sketch, "E112.MirrorCS", {"start": v(-41.4, -30.88) * mm, "end": v(-43.66, -33.1) * mm});
            skLineSegment(sketch, "E113.MirrorCS", {"start": v(-46.11, -30.62) * mm, "end": v(-43.85, -28.4) * mm});
            skLineSegment(sketch, "E114.MirrorCS", {"start": v(-43.85, -28.4) * mm, "end": v(-46.07, -26.13) * mm});
            skLineSegment(sketch, "E115.MirrorCS", {"start": v(-46.07, -26.13) * mm, "end": v(-48.34, -28.35) * mm});
            skLineSegment(sketch, "E116.MirrorCS", {"start": v(-50.79, -25.86) * mm, "end": v(-48.53, -23.63) * mm});
            skLineSegment(sketch, "E117.MirrorCS", {"start": v(-48.53, -23.63) * mm, "end": v(-50.75, -21.37) * mm});
            skLineSegment(sketch, "E118.MirrorCS", {"start": v(-50.75, -21.37) * mm, "end": v(-53.02, -23.6) * mm});
            skLineSegment(sketch, "E119.MirrorCS", {"start": v(-55.47, -21.1) * mm, "end": v(-53.2, -18.87) * mm});
            skLineSegment(sketch, "E120.MirrorCS", {"start": v(-53.2, -18.87) * mm, "end": v(-55.43, -16.6) * mm});
            skLineSegment(sketch, "E121.MirrorCS", {"start": v(-55.43, -16.6) * mm, "end": v(-57.7, -18.83) * mm});
            skLineSegment(sketch, "E122.MirrorCS", {"start": v(-60.14, -16.34) * mm, "end": v(-57.88, -14.12) * mm});
            skLineSegment(sketch, "E123.MirrorCS", {"start": v(-57.88, -14.12) * mm, "end": v(-60.1, -11.85) * mm});
            skLineSegment(sketch, "E124.MirrorCS", {"start": v(-60.1, -11.85) * mm, "end": v(-62.37, -14.08) * mm});
            skLineSegment(sketch, "E125.MirrorCS", {"start": v(-64.82, -11.58) * mm, "end": v(-62.55, -9.36) * mm});
            skLineSegment(sketch, "E126.MirrorCS", {"start": v(-62.55, -9.36) * mm, "end": v(-64.78, -7.1) * mm});
            skLineSegment(sketch, "E127.MirrorCS", {"start": v(-64.78, -7.1) * mm, "end": v(-67.04, -9.32) * mm});
            skLineSegment(sketch, "E128.MirrorCS", {"start": v(-69.5, -6.82) * mm, "end": v(-67.23, -4.6) * mm});
            skLineSegment(sketch, "E129.MirrorCS", {"start": v(-67.23, -4.6) * mm, "end": v(-69.45, -2.33) * mm});
            skLineSegment(sketch, "E130.MirrorCS", {"start": v(-69.45, -2.33) * mm, "end": v(-71.72, -4.56) * mm});
            skSolve(sketch);
        }
        {
            var Q0;
            {var subQ0=sQuery(id+"F21.wireOp",EDGE,"E128.MirrorCS");Q0=makeQuery(id+"F21.imprint","IMPRINT",FACE,{"disambiguationData":[TD([[makeQuery(id+"F21.imprint","IMPRINT",EDGE,{"derivedFrom":subQ0}),1.0]])]});}
            var Q1;
            {var subQ0=sQuery(id+"F21.wireOp",EDGE,"E125.MirrorCS");Q1=makeQuery(id+"F21.imprint","IMPRINT",FACE,{"disambiguationData":[TD([[makeQuery(id+"F21.imprint","IMPRINT",EDGE,{"derivedFrom":subQ0}),1.0]])]});}
            var Q2;
            {var subQ0=sQuery(id+"F21.wireOp",EDGE,"E122.MirrorCS");Q2=makeQuery(id+"F21.imprint","IMPRINT",FACE,{"disambiguationData":[TD([[makeQuery(id+"F21.imprint","IMPRINT",EDGE,{"derivedFrom":subQ0}),1.0]])]});}
            var Q3;
            {var subQ0=sQuery(id+"F21.wireOp",EDGE,"E119.MirrorCS");Q3=makeQuery(id+"F21.imprint","IMPRINT",FACE,{"disambiguationData":[TD([[makeQuery(id+"F21.imprint","IMPRINT",EDGE,{"derivedFrom":subQ0}),1.0]])]});}
            var Q4;
            {var subQ0=sQuery(id+"F21.wireOp",EDGE,"E116.MirrorCS");Q4=makeQuery(id+"F21.imprint","IMPRINT",FACE,{"disambiguationData":[TD([[makeQuery(id+"F21.imprint","IMPRINT",EDGE,{"derivedFrom":subQ0}),1.0]])]});}
            var Q5;
            {var subQ0=sQuery(id+"F21.wireOp",EDGE,"E113.MirrorCS");Q5=makeQuery(id+"F21.imprint","IMPRINT",FACE,{"disambiguationData":[TD([[makeQuery(id+"F21.imprint","IMPRINT",EDGE,{"derivedFrom":subQ0}),1.0]])]});}
            var Q6;
            {var subQ0=sQuery(id+"F21.wireOp",EDGE,"E110.MirrorCS");Q6=makeQuery(id+"F21.imprint","IMPRINT",FACE,{"disambiguationData":[TD([[makeQuery(id+"F21.imprint","IMPRINT",EDGE,{"derivedFrom":subQ0}),1.0]])]});}
            var Q7;
            {var subQ0=sQuery(id+"F21.wireOp",EDGE,"E102");Q7=makeQuery(id+"F21.imprint","IMPRINT",FACE,{"disambiguationData":[TD([[makeQuery(id+"F21.imprint","IMPRINT",EDGE,{"derivedFrom":subQ0}),-1.0]])]});}
            var Q8;
            {var subQ0=sQuery(id+"F21.wireOp",EDGE,"E105");Q8=makeQuery(id+"F21.imprint","IMPRINT",FACE,{"disambiguationData":[TD([[makeQuery(id+"F21.imprint","IMPRINT",EDGE,{"derivedFrom":subQ0}),-1.0]])]});}
            var Q9;
            {var subQ0=sQuery(id+"F21.wireOp",EDGE,"E108.1.0.0");Q9=makeQuery(id+"F21.imprint","IMPRINT",FACE,{"disambiguationData":[TD([[makeQuery(id+"F21.imprint","IMPRINT",EDGE,{"derivedFrom":subQ0}),-1.0]])]});}
            var Q10;
            {var subQ0=sQuery(id+"F21.wireOp",EDGE,"E108.2.0.0");Q10=makeQuery(id+"F21.imprint","IMPRINT",FACE,{"disambiguationData":[TD([[makeQuery(id+"F21.imprint","IMPRINT",EDGE,{"derivedFrom":subQ0}),-1.0]])]});}
            var Q11;
            {var subQ0=sQuery(id+"F21.wireOp",EDGE,"E109.0.3.0");Q11=makeQuery(id+"F21.imprint","IMPRINT",FACE,{"disambiguationData":[TD([[makeQuery(id+"F21.imprint","IMPRINT",EDGE,{"derivedFrom":subQ0}),-1.0]])]});}
            var Q12;
            {var subQ0=sQuery(id+"F21.wireOp",EDGE,"E109.0.4.0");Q12=makeQuery(id+"F21.imprint","IMPRINT",FACE,{"disambiguationData":[TD([[makeQuery(id+"F21.imprint","IMPRINT",EDGE,{"derivedFrom":subQ0}),-1.0]])]});}
            var Q13;
            {var subQ0=sQuery(id+"F21.wireOp",EDGE,"E109.0.5.0");Q13=makeQuery(id+"F21.imprint","IMPRINT",FACE,{"disambiguationData":[TD([[makeQuery(id+"F21.imprint","IMPRINT",EDGE,{"derivedFrom":subQ0}),-1.0]])]});}
            var Q14;
            {var subQ0=sQuery(id+"F21.wireOp",EDGE,"E109.0.6.0");Q14=makeQuery(id+"F21.imprint","IMPRINT",FACE,{"disambiguationData":[TD([[makeQuery(id+"F21.imprint","IMPRINT",EDGE,{"derivedFrom":subQ0}),-1.0]])]});}
            extrude(context, id + "F22", {"entities" : qUnion([Q0, Q1, Q2, Q3, Q4, Q5, Q6, Q7, Q8, Q9, Q10, Q11, Q12, Q13, Q14]), "operationType" : NewBodyOperationType.REMOVE, "oppositeDirection" : true, "depth" : 25.4 * mm, "offsetDistance" : 25.4 * mm});
        }
        {
            var Q0;
            Q0=makeQuery(id+"F1.opExtrude","CAP_VERTEX",VERTEX,{"disambiguationData":[OSD([sQuery(id+"F0.wireOp",EDGE,"E5"),sQuery(id+"F0.wireOp",EDGE,"E6")])],"isStart":false});
            var Q1;
            Q1=makeQuery(id+"F1.opExtrude","CAP_VERTEX",VERTEX,{"disambiguationData":[OSD([sQuery(id+"F0.wireOp",EDGE,"E0"),sQuery(id+"F0.wireOp",EDGE,"E1")])],"isStart":false});
            var Q2;
            Q2=makeQuery(id+"F1.opExtrude","CAP_VERTEX",VERTEX,{"disambiguationData":[OSD([sQuery(id+"F0.wireOp",EDGE,"E0"),sQuery(id+"F0.wireOp",EDGE,"E1")])],"isStart":true});
            cPlane(context, id + "F23", {"entities" : qUnion([Q0, Q1, Q2]), "cplaneType" : CPlaneType.THREE_POINT, "offset" : 25.4 * mm, "width" : 152.4 * mm, "height" : 152.4 * mm});
        }
        {
            var Q0;
            Q0=makeQuery(id+"F6.opExtrude","SWEPT_FACE",FACE,{"disambiguationData":[OSD([sQuery(id+"F0.wireOp",EDGE,"E0")])]});
            var sketch = newSketch(context, id + "F24", { "sketchPlane" : qUnion([Q0])});
            skLineSegment(sketch, "E131.0.0", {"start": v(48.91, 3.17) * mm, "end": v(48.91, 0) * mm});
            skLineSegment(sketch, "E131.0.1", {"start": v(48.91, 0) * mm, "end": v(55.3, 0) * mm});
            skLineSegment(sketch, "E131.0.2", {"start": v(55.3, 0) * mm, "end": v(55.3, 3.18) * mm});
            skLineSegment(sketch, "E131.0.3", {"start": v(55.3, 3.18) * mm, "end": v(48.91, 3.18) * mm});
            skPoint(sketch, "E132.0", {"position": v(43.99, 0) * mm});
            skLineSegment(sketch, "E133.0.0", {"start": v(42.24, 3.17) * mm, "end": v(42.24, 0) * mm});
            skLineSegment(sketch, "E133.0.1", {"start": v(42.24, 0) * mm, "end": v(45.74, 0) * mm});
            skLineSegment(sketch, "E133.0.2", {"start": v(45.74, 0) * mm, "end": v(45.74, 3.17) * mm});
            skLineSegment(sketch, "E133.0.3", {"start": v(45.74, 3.18) * mm, "end": v(42.24, 3.18) * mm});
            skLineSegment(sketch, "E134.0.0", {"start": v(35.57, 3.17) * mm, "end": v(35.57, 0) * mm});
            skLineSegment(sketch, "E134.0.1", {"start": v(35.57, 0) * mm, "end": v(39.07, 0) * mm});
            skLineSegment(sketch, "E134.0.2", {"start": v(39.07, 0) * mm, "end": v(39.07, 3.17) * mm});
            skLineSegment(sketch, "E134.0.3", {"start": v(39.07, 3.18) * mm, "end": v(35.57, 3.18) * mm});
            skLineSegment(sketch, "E135.0.0", {"start": v(28.9, 3.17) * mm, "end": v(28.9, 0) * mm});
            skLineSegment(sketch, "E135.0.1", {"start": v(28.9, 0) * mm, "end": v(32.4, 0) * mm});
            skLineSegment(sketch, "E135.0.2", {"start": v(32.4, 0) * mm, "end": v(32.4, 3.17) * mm});
            skLineSegment(sketch, "E135.0.3", {"start": v(32.4, 3.18) * mm, "end": v(28.9, 3.18) * mm});
            skLineSegment(sketch, "E136.0.0", {"start": v(22.23, 3.17) * mm, "end": v(22.23, 0) * mm});
            skLineSegment(sketch, "E136.0.1", {"start": v(22.23, 0) * mm, "end": v(25.72, 0) * mm});
            skLineSegment(sketch, "E136.0.2", {"start": v(25.72, 0) * mm, "end": v(25.72, 3.17) * mm});
            skLineSegment(sketch, "E136.0.3", {"start": v(25.72, 3.18) * mm, "end": v(22.23, 3.18) * mm});
            skLineSegment(sketch, "E137.0.0", {"start": v(15.56, 3.17) * mm, "end": v(15.56, 0) * mm});
            skLineSegment(sketch, "E137.0.1", {"start": v(15.56, 0) * mm, "end": v(19.05, 0) * mm});
            skLineSegment(sketch, "E137.0.2", {"start": v(19.05, 0) * mm, "end": v(19.05, 3.17) * mm});
            skLineSegment(sketch, "E137.0.3", {"start": v(19.05, 3.18) * mm, "end": v(15.56, 3.18) * mm});
            skLineSegment(sketch, "E138.0.0", {"start": v(8.89, 3.17) * mm, "end": v(8.89, 0) * mm});
            skLineSegment(sketch, "E138.0.1", {"start": v(8.89, 0) * mm, "end": v(12.38, 0) * mm});
            skLineSegment(sketch, "E138.0.2", {"start": v(12.38, 0) * mm, "end": v(12.38, 3.17) * mm});
            skLineSegment(sketch, "E138.0.3", {"start": v(12.38, 3.18) * mm, "end": v(8.89, 3.18) * mm});
            skLineSegment(sketch, "E139.0.0", {"start": v(2.54, 3.17) * mm, "end": v(2.54, 0) * mm});
            skLineSegment(sketch, "E139.0.1", {"start": v(2.54, 0) * mm, "end": v(5.71, 0) * mm});
            skLineSegment(sketch, "E139.0.2", {"start": v(5.71, 0) * mm, "end": v(5.71, 3.17) * mm});
            skLineSegment(sketch, "E139.0.3", {"start": v(5.71, 3.18) * mm, "end": v(2.54, 3.18) * mm});
            skLineSegment(sketch, "E140.0.0", {"start": v(-3.81, 3.17) * mm, "end": v(-3.81, 0) * mm});
            skLineSegment(sketch, "E140.0.1", {"start": v(-3.81, 0) * mm, "end": v(-0.64, 0) * mm});
            skLineSegment(sketch, "E140.0.2", {"start": v(-0.64, 0) * mm, "end": v(-0.64, 3.17) * mm});
            skLineSegment(sketch, "E140.0.3", {"start": v(-0.64, 3.18) * mm, "end": v(-3.81, 3.18) * mm});
            skLineSegment(sketch, "E141.0.0", {"start": v(-10.48, 3.17) * mm, "end": v(-10.48, 0) * mm});
            skLineSegment(sketch, "E141.0.1", {"start": v(-10.48, 0) * mm, "end": v(-6.99, 0) * mm});
            skLineSegment(sketch, "E141.0.2", {"start": v(-6.99, 0) * mm, "end": v(-6.99, 3.17) * mm});
            skLineSegment(sketch, "E141.0.3", {"start": v(-6.99, 3.18) * mm, "end": v(-10.48, 3.18) * mm});
            skLineSegment(sketch, "E142.0.0", {"start": v(-17.16, 3.17) * mm, "end": v(-17.16, 0) * mm});
            skLineSegment(sketch, "E142.0.1", {"start": v(-17.16, 0) * mm, "end": v(-13.66, 0) * mm});
            skLineSegment(sketch, "E142.0.2", {"start": v(-13.66, 0) * mm, "end": v(-13.66, 3.17) * mm});
            skLineSegment(sketch, "E142.0.3", {"start": v(-13.66, 3.18) * mm, "end": v(-17.16, 3.18) * mm});
            skLineSegment(sketch, "E143.0.0", {"start": v(-23.83, 3.17) * mm, "end": v(-23.83, 0) * mm});
            skLineSegment(sketch, "E143.0.1", {"start": v(-23.83, 0) * mm, "end": v(-20.33, 0) * mm});
            skLineSegment(sketch, "E143.0.2", {"start": v(-20.33, 0) * mm, "end": v(-20.33, 3.17) * mm});
            skLineSegment(sketch, "E143.0.3", {"start": v(-20.33, 3.18) * mm, "end": v(-23.83, 3.18) * mm});
            skLineSegment(sketch, "E144.0.0", {"start": v(-43.84, 3.17) * mm, "end": v(-43.84, 0) * mm});
            skLineSegment(sketch, "E144.0.1", {"start": v(-43.84, 0) * mm, "end": v(-40.34, 0) * mm});
            skLineSegment(sketch, "E144.0.2", {"start": v(-40.34, 0) * mm, "end": v(-40.34, 3.17) * mm});
            skLineSegment(sketch, "E144.0.3", {"start": v(-40.34, 3.18) * mm, "end": v(-43.84, 3.18) * mm});
            skLineSegment(sketch, "E145.0.0", {"start": v(-37.17, 3.17) * mm, "end": v(-37.17, 0) * mm});
            skLineSegment(sketch, "E145.0.1", {"start": v(-37.17, 0) * mm, "end": v(-33.67, 0) * mm});
            skLineSegment(sketch, "E145.0.2", {"start": v(-33.67, 0) * mm, "end": v(-33.67, 3.17) * mm});
            skLineSegment(sketch, "E145.0.3", {"start": v(-33.67, 3.18) * mm, "end": v(-37.17, 3.18) * mm});
            skLineSegment(sketch, "E146.0.0", {"start": v(-30.5, 3.17) * mm, "end": v(-30.5, 0) * mm});
            skLineSegment(sketch, "E146.0.1", {"start": v(-30.5, 0) * mm, "end": v(-27, 0) * mm});
            skLineSegment(sketch, "E146.0.2", {"start": v(-27, 0) * mm, "end": v(-27, 3.17) * mm});
            skLineSegment(sketch, "E146.0.3", {"start": v(-27, 3.18) * mm, "end": v(-30.5, 3.18) * mm});
            skLineSegment(sketch, "E147.0.0", {"start": v(-53.4, 0) * mm, "end": v(-47.02, 0) * mm});
            skLineSegment(sketch, "E147.0.1", {"start": v(-47.02, 0) * mm, "end": v(-47.02, 3.17) * mm});
            skLineSegment(sketch, "E147.0.2", {"start": v(-47.02, 3.18) * mm, "end": v(-53.4, 3.18) * mm});
            skLineSegment(sketch, "E147.0.3", {"start": v(-53.4, 3.18) * mm, "end": v(-53.4, 0) * mm});
            skSolve(sketch);
        }
        {
            var Q0;
            Q0 = qSketchRegion(id + "F24", true);
            extrude(context, id + "F25", {"entities" : qUnion([Q0]), "operationType" : NewBodyOperationType.REMOVE, "endBound" : BoundingType.SYMMETRIC, "oppositeDirection" : true, "depth" : 25.4 * mm, "offsetDistance" : 25.4 * mm});
        }
        {
            var Q0;
            Q0=makeQuery(id+"F3.opExtrude","SWEPT_FACE",FACE,{"disambiguationData":[OSD([sQuery(id+"F0.wireOp",EDGE,"E7")])]});
            var sketch = newSketch(context, id + "F26", { "sketchPlane" : qUnion([Q0])});
            skLineSegment(sketch, "E148.0.0", {"start": v(57.15, 3.17) * mm, "end": v(57.15, 0) * mm});
            skLineSegment(sketch, "E148.0.1", {"start": v(57.15, 0) * mm, "end": v(60.32, 0) * mm});
            skLineSegment(sketch, "E148.0.2", {"start": v(60.32, 0) * mm, "end": v(60.32, 3.18) * mm});
            skLineSegment(sketch, "E148.0.3", {"start": v(60.32, 3.18) * mm, "end": v(57.15, 3.18) * mm});
            skLineSegment(sketch, "E149.0.0", {"start": v(44.45, 0) * mm, "end": v(50.8, 0) * mm});
            skLineSegment(sketch, "E149.0.1", {"start": v(50.8, 0) * mm, "end": v(50.8, 3.17) * mm});
            skLineSegment(sketch, "E149.0.2", {"start": v(50.8, 3.18) * mm, "end": v(44.45, 3.18) * mm});
            skLineSegment(sketch, "E149.0.3", {"start": v(44.45, 3.17) * mm, "end": v(44.45, 0) * mm});
            skLineSegment(sketch, "E150.0.0", {"start": v(31.75, 0) * mm, "end": v(38.1, 0) * mm});
            skLineSegment(sketch, "E150.0.1", {"start": v(38.1, 0) * mm, "end": v(38.1, 3.17) * mm});
            skLineSegment(sketch, "E150.0.2", {"start": v(38.1, 3.18) * mm, "end": v(31.75, 3.18) * mm});
            skLineSegment(sketch, "E150.0.3", {"start": v(31.75, 3.17) * mm, "end": v(31.75, 0) * mm});
            skLineSegment(sketch, "E151.0.0", {"start": v(22.23, 0) * mm, "end": v(25.4, 0) * mm});
            skLineSegment(sketch, "E151.0.1", {"start": v(25.4, 0) * mm, "end": v(25.4, 3.17) * mm});
            skLineSegment(sketch, "E151.0.2", {"start": v(25.4, 3.18) * mm, "end": v(22.23, 3.18) * mm});
            skLineSegment(sketch, "E151.0.3", {"start": v(22.23, 3.18) * mm, "end": v(22.23, 0) * mm});
            skSolve(sketch);
        }
        {
            var Q0;
            Q0 = qSketchRegion(id + "F26", true);
            extrude(context, id + "F27", {"entities" : qUnion([Q0]), "operationType" : NewBodyOperationType.REMOVE, "oppositeDirection" : true, "depth" : 25.4 * mm, "offsetDistance" : 25.4 * mm});
        }
        {
            var Q0;
            Q0=makeQuery(id+"F4.opExtrude","SWEPT_FACE",FACE,{"disambiguationData":[OSD([sQuery(id+"F0.wireOp",EDGE,"E8")])]});
            var sketch = newSketch(context, id + "F28", { "sketchPlane" : qUnion([Q0])});
            skLineSegment(sketch, "E152.0.0", {"start": v(12.93, 3.17) * mm, "end": v(12.93, 0) * mm});
            skLineSegment(sketch, "E152.0.1", {"start": v(12.93, 0) * mm, "end": v(16.1, 0) * mm});
            skLineSegment(sketch, "E152.0.2", {"start": v(16.1, 0) * mm, "end": v(16.1, 3.18) * mm});
            skLineSegment(sketch, "E152.0.3", {"start": v(16.1, 3.18) * mm, "end": v(12.93, 3.18) * mm});
            skLineSegment(sketch, "E153.0.0", {"start": v(1.98, 0) * mm, "end": v(9.42, 0) * mm});
            skLineSegment(sketch, "E153.0.1", {"start": v(9.42, 0) * mm, "end": v(9.42, 3.17) * mm});
            skLineSegment(sketch, "E153.0.2", {"start": v(9.42, 3.18) * mm, "end": v(1.98, 3.18) * mm});
            skLineSegment(sketch, "E153.0.3", {"start": v(1.98, 3.17) * mm, "end": v(1.98, 0) * mm});
            skLineSegment(sketch, "E154.0.0", {"start": v(-8.96, 0) * mm, "end": v(-1.53, 0) * mm});
            skLineSegment(sketch, "E154.0.1", {"start": v(-1.53, 0) * mm, "end": v(-1.53, 3.17) * mm});
            skLineSegment(sketch, "E154.0.2", {"start": v(-1.53, 3.18) * mm, "end": v(-8.96, 3.18) * mm});
            skLineSegment(sketch, "E154.0.3", {"start": v(-8.96, 3.17) * mm, "end": v(-8.96, 0) * mm});
            skLineSegment(sketch, "E155.0.0", {"start": v(-15.65, 0) * mm, "end": v(-12.47, 0) * mm});
            skLineSegment(sketch, "E155.0.1", {"start": v(-12.47, 0) * mm, "end": v(-12.47, 3.17) * mm});
            skLineSegment(sketch, "E155.0.2", {"start": v(-12.47, 3.18) * mm, "end": v(-15.65, 3.18) * mm});
            skLineSegment(sketch, "E155.0.3", {"start": v(-15.65, 3.18) * mm, "end": v(-15.65, 0) * mm});
            skSolve(sketch);
        }
        {
            var Q0;
            Q0 = qSketchRegion(id + "F28", true);
            extrude(context, id + "F29", {"entities" : qUnion([Q0]), "operationType" : NewBodyOperationType.REMOVE, "oppositeDirection" : true, "depth" : 25.4 * mm, "offsetDistance" : 25.4 * mm});
        }
        {
            var Q0;
            Q0=makeQuery(id+"F5.opExtrude","SWEPT_FACE",FACE,{"disambiguationData":[OSD([sQuery(id+"F0.wireOp",EDGE,"E9")])]});
            var sketch = newSketch(context, id + "F30", { "sketchPlane" : qUnion([Q0])});
            skLineSegment(sketch, "E156.0.0", {"start": v(-3.17, 3.17) * mm, "end": v(-3.17, 0) * mm});
            skLineSegment(sketch, "E156.0.1", {"start": v(-3.17, 0) * mm, "end": v(0, 0) * mm});
            skLineSegment(sketch, "E156.0.2", {"start": v(0, 0) * mm, "end": v(0, 3.18) * mm});
            skLineSegment(sketch, "E156.0.3", {"start": v(0, 3.18) * mm, "end": v(-3.17, 3.18) * mm});
            skPoint(sketch, "E157.0", {"position": v(-10.18, 1.59) * mm});
            skLineSegment(sketch, "E158.0.0", {"start": v(-10.18, 0) * mm, "end": v(-8.22, 0) * mm});
            skLineSegment(sketch, "E158.0.1", {"start": v(-8.22, 0) * mm, "end": v(-8.22, 3.17) * mm});
            skLineSegment(sketch, "E158.0.2", {"start": v(-8.22, 3.18) * mm, "end": v(-10.18, 3.18) * mm});
            skLineSegment(sketch, "E158.0.3", {"start": v(-10.18, 3.17) * mm, "end": v(-10.18, 0) * mm});
            skLineSegment(sketch, "E159.0.0", {"start": v(-17.18, 0) * mm, "end": v(-15.22, 0) * mm});
            skLineSegment(sketch, "E159.0.1", {"start": v(-15.22, 0) * mm, "end": v(-15.22, 3.17) * mm});
            skLineSegment(sketch, "E159.0.2", {"start": v(-15.22, 3.18) * mm, "end": v(-17.18, 3.18) * mm});
            skLineSegment(sketch, "E159.0.3", {"start": v(-17.18, 3.17) * mm, "end": v(-17.18, 0) * mm});
            skLineSegment(sketch, "E160.0.0", {"start": v(-25.4, 0) * mm, "end": v(-22.22, 0) * mm});
            skLineSegment(sketch, "E160.0.1", {"start": v(-22.22, 0) * mm, "end": v(-22.22, 3.17) * mm});
            skLineSegment(sketch, "E160.0.2", {"start": v(-22.22, 3.18) * mm, "end": v(-25.4, 3.18) * mm});
            skLineSegment(sketch, "E160.0.3", {"start": v(-25.4, 3.18) * mm, "end": v(-25.4, 0) * mm});
            skSolve(sketch);
        }
        {
            var Q0;
            Q0 = qSketchRegion(id + "F30", true);
            extrude(context, id + "F31", {"entities" : qUnion([Q0]), "operationType" : NewBodyOperationType.REMOVE, "oppositeDirection" : true, "depth" : 25.4 * mm, "offsetDistance" : 25.4 * mm});
        }
        {
            var Q0;
            Q0=makeQuery(id+"F6.opExtrude","SWEPT_FACE",FACE,{"disambiguationData":[OSD([sQuery(id+"F0.wireOp",EDGE,"E0")])]});
            var sketch = newSketch(context, id + "F32", { "sketchPlane" : qUnion([Q0])});
            skLineSegment(sketch, "E161.0.0", {"start": v(42.24, 3.17) * mm, "end": v(42.24, 0) * mm});
            skLineSegment(sketch, "E161.0.1", {"start": v(42.24, 0) * mm, "end": v(45.74, 0) * mm});
            skLineSegment(sketch, "E161.0.2", {"start": v(45.74, 0) * mm, "end": v(45.74, 3.17) * mm});
            skLineSegment(sketch, "E161.0.3", {"start": v(45.74, 3.18) * mm, "end": v(42.24, 3.18) * mm});
            skLineSegment(sketch, "E162.0.0", {"start": v(35.57, 3.17) * mm, "end": v(35.57, 0) * mm});
            skLineSegment(sketch, "E162.0.1", {"start": v(35.57, 0) * mm, "end": v(39.07, 0) * mm});
            skLineSegment(sketch, "E162.0.2", {"start": v(39.07, 0) * mm, "end": v(39.07, 3.17) * mm});
            skLineSegment(sketch, "E162.0.3", {"start": v(39.07, 3.18) * mm, "end": v(35.57, 3.18) * mm});
            skLineSegment(sketch, "E163.0.0", {"start": v(28.9, 3.17) * mm, "end": v(28.9, 0) * mm});
            skLineSegment(sketch, "E163.0.1", {"start": v(28.9, 0) * mm, "end": v(32.4, 0) * mm});
            skLineSegment(sketch, "E163.0.2", {"start": v(32.4, 0) * mm, "end": v(32.4, 3.17) * mm});
            skLineSegment(sketch, "E163.0.3", {"start": v(32.4, 3.18) * mm, "end": v(28.9, 3.18) * mm});
            skLineSegment(sketch, "E164.0.0", {"start": v(22.23, 3.17) * mm, "end": v(22.23, 0) * mm});
            skLineSegment(sketch, "E164.0.1", {"start": v(22.23, 0) * mm, "end": v(25.72, 0) * mm});
            skLineSegment(sketch, "E164.0.2", {"start": v(25.72, 0) * mm, "end": v(25.72, 3.17) * mm});
            skLineSegment(sketch, "E164.0.3", {"start": v(25.72, 3.18) * mm, "end": v(22.23, 3.18) * mm});
            skLineSegment(sketch, "E165.0.0", {"start": v(15.56, 3.17) * mm, "end": v(15.56, 0) * mm});
            skLineSegment(sketch, "E165.0.1", {"start": v(15.56, 0) * mm, "end": v(19.05, 0) * mm});
            skLineSegment(sketch, "E165.0.2", {"start": v(19.05, 0) * mm, "end": v(19.05, 3.17) * mm});
            skLineSegment(sketch, "E165.0.3", {"start": v(19.05, 3.18) * mm, "end": v(15.56, 3.18) * mm});
            skLineSegment(sketch, "E166.0.0", {"start": v(8.89, 3.17) * mm, "end": v(8.89, 0) * mm});
            skLineSegment(sketch, "E166.0.1", {"start": v(8.89, 0) * mm, "end": v(12.38, 0) * mm});
            skLineSegment(sketch, "E166.0.2", {"start": v(12.38, 0) * mm, "end": v(12.38, 3.17) * mm});
            skLineSegment(sketch, "E166.0.3", {"start": v(12.38, 3.18) * mm, "end": v(8.89, 3.18) * mm});
            skLineSegment(sketch, "E167.0.0", {"start": v(2.54, 3.17) * mm, "end": v(2.54, 0) * mm});
            skLineSegment(sketch, "E167.0.1", {"start": v(2.54, 0) * mm, "end": v(5.71, 0) * mm});
            skLineSegment(sketch, "E167.0.2", {"start": v(5.71, 0) * mm, "end": v(5.71, 3.17) * mm});
            skLineSegment(sketch, "E167.0.3", {"start": v(5.71, 3.18) * mm, "end": v(2.54, 3.18) * mm});
            skLineSegment(sketch, "E168.0.0", {"start": v(-3.81, 3.17) * mm, "end": v(-3.81, 0) * mm});
            skLineSegment(sketch, "E168.0.1", {"start": v(-3.81, 0) * mm, "end": v(-0.64, 0) * mm});
            skLineSegment(sketch, "E168.0.2", {"start": v(-0.64, 0) * mm, "end": v(-0.64, 3.17) * mm});
            skLineSegment(sketch, "E168.0.3", {"start": v(-0.64, 3.18) * mm, "end": v(-3.81, 3.18) * mm});
            skLineSegment(sketch, "E169.0.0", {"start": v(-10.48, 3.17) * mm, "end": v(-10.48, 0) * mm});
            skLineSegment(sketch, "E169.0.1", {"start": v(-10.48, 0) * mm, "end": v(-6.99, 0) * mm});
            skLineSegment(sketch, "E169.0.2", {"start": v(-6.99, 0) * mm, "end": v(-6.99, 3.17) * mm});
            skLineSegment(sketch, "E169.0.3", {"start": v(-6.99, 3.18) * mm, "end": v(-10.48, 3.18) * mm});
            skLineSegment(sketch, "E170.0.0", {"start": v(-17.16, 3.17) * mm, "end": v(-17.16, 0) * mm});
            skLineSegment(sketch, "E170.0.1", {"start": v(-17.16, 0) * mm, "end": v(-13.66, 0) * mm});
            skLineSegment(sketch, "E170.0.2", {"start": v(-13.66, 0) * mm, "end": v(-13.66, 3.17) * mm});
            skLineSegment(sketch, "E170.0.3", {"start": v(-13.66, 3.18) * mm, "end": v(-17.16, 3.18) * mm});
            skLineSegment(sketch, "E171.0.0", {"start": v(-23.83, 3.17) * mm, "end": v(-23.83, 0) * mm});
            skLineSegment(sketch, "E171.0.1", {"start": v(-23.83, 0) * mm, "end": v(-20.33, 0) * mm});
            skLineSegment(sketch, "E171.0.2", {"start": v(-20.33, 0) * mm, "end": v(-20.33, 3.17) * mm});
            skLineSegment(sketch, "E171.0.3", {"start": v(-20.33, 3.18) * mm, "end": v(-23.83, 3.18) * mm});
            skLineSegment(sketch, "E172.0.0", {"start": v(-30.5, 3.17) * mm, "end": v(-30.5, 0) * mm});
            skLineSegment(sketch, "E172.0.1", {"start": v(-30.5, 0) * mm, "end": v(-27, 0) * mm});
            skLineSegment(sketch, "E172.0.2", {"start": v(-27, 0) * mm, "end": v(-27, 3.17) * mm});
            skLineSegment(sketch, "E172.0.3", {"start": v(-27, 3.18) * mm, "end": v(-30.5, 3.18) * mm});
            skLineSegment(sketch, "E173.0.0", {"start": v(-37.17, 3.17) * mm, "end": v(-37.17, 0) * mm});
            skLineSegment(sketch, "E173.0.1", {"start": v(-37.17, 0) * mm, "end": v(-33.67, 0) * mm});
            skLineSegment(sketch, "E173.0.2", {"start": v(-33.67, 0) * mm, "end": v(-33.67, 3.17) * mm});
            skLineSegment(sketch, "E173.0.3", {"start": v(-33.67, 3.18) * mm, "end": v(-37.17, 3.18) * mm});
            skLineSegment(sketch, "E174.0.0", {"start": v(-43.84, 3.17) * mm, "end": v(-43.84, 0) * mm});
            skLineSegment(sketch, "E174.0.1", {"start": v(-43.84, 0) * mm, "end": v(-40.34, 0) * mm});
            skLineSegment(sketch, "E174.0.2", {"start": v(-40.34, 0) * mm, "end": v(-40.34, 3.17) * mm});
            skLineSegment(sketch, "E174.0.3", {"start": v(-40.34, 3.18) * mm, "end": v(-43.84, 3.18) * mm});
            skSolve(sketch);
        }
        {
            var Q0;
            Q0 = qSketchRegion(id + "F32", true);
            extrude(context, id + "F33", {"entities" : qUnion([Q0]), "operationType" : NewBodyOperationType.REMOVE, "oppositeDirection" : true, "depth" : 25.4 * mm, "offsetDistance" : 25.4 * mm});
        }
        {
            var Q0;
            Q0=makeQuery(id+"F7.opExtrude","SWEPT_FACE",FACE,{"disambiguationData":[OSD([sQuery(id+"F0.wireOp",EDGE,"E1")])]});
            var sketch = newSketch(context, id + "F34", { "sketchPlane" : qUnion([Q0])});
            skLineSegment(sketch, "E175.0.0", {"start": v(47.02, 3.17) * mm, "end": v(47.02, 0) * mm});
            skLineSegment(sketch, "E175.0.1", {"start": v(47.02, 0) * mm, "end": v(53.4, 0) * mm});
            skLineSegment(sketch, "E175.0.2", {"start": v(53.4, 0) * mm, "end": v(53.4, 3.18) * mm});
            skLineSegment(sketch, "E175.0.3", {"start": v(53.4, 3.18) * mm, "end": v(47.02, 3.18) * mm});
            skLineSegment(sketch, "E176.0.0", {"start": v(43.84, 0) * mm, "end": v(43.84, 3.17) * mm});
            skLineSegment(sketch, "E176.0.1", {"start": v(43.84, 3.18) * mm, "end": v(40.34, 3.18) * mm});
            skLineSegment(sketch, "E176.0.2", {"start": v(40.34, 3.17) * mm, "end": v(40.34, 0) * mm});
            skLineSegment(sketch, "E176.0.3", {"start": v(40.34, 0) * mm, "end": v(43.84, 0) * mm});
            skLineSegment(sketch, "E177.0.0", {"start": v(37.17, 0) * mm, "end": v(37.17, 3.17) * mm});
            skLineSegment(sketch, "E177.0.1", {"start": v(37.17, 3.18) * mm, "end": v(33.67, 3.18) * mm});
            skLineSegment(sketch, "E177.0.2", {"start": v(33.67, 3.17) * mm, "end": v(33.67, 0) * mm});
            skLineSegment(sketch, "E177.0.3", {"start": v(33.67, 0) * mm, "end": v(37.17, 0) * mm});
            skLineSegment(sketch, "E178.0.0", {"start": v(30.5, 0) * mm, "end": v(30.5, 3.17) * mm});
            skLineSegment(sketch, "E178.0.1", {"start": v(30.5, 3.18) * mm, "end": v(27, 3.18) * mm});
            skLineSegment(sketch, "E178.0.2", {"start": v(27, 3.17) * mm, "end": v(27, 0) * mm});
            skLineSegment(sketch, "E178.0.3", {"start": v(27, 0) * mm, "end": v(30.5, 0) * mm});
            skLineSegment(sketch, "E179.0.0", {"start": v(23.83, 0) * mm, "end": v(23.83, 3.17) * mm});
            skLineSegment(sketch, "E179.0.1", {"start": v(23.83, 3.18) * mm, "end": v(20.33, 3.18) * mm});
            skLineSegment(sketch, "E179.0.2", {"start": v(20.33, 3.17) * mm, "end": v(20.33, 0) * mm});
            skLineSegment(sketch, "E179.0.3", {"start": v(20.33, 0) * mm, "end": v(23.83, 0) * mm});
            skLineSegment(sketch, "E180.0.0", {"start": v(17.16, 0) * mm, "end": v(17.16, 3.17) * mm});
            skLineSegment(sketch, "E180.0.1", {"start": v(17.16, 3.18) * mm, "end": v(13.66, 3.18) * mm});
            skLineSegment(sketch, "E180.0.2", {"start": v(13.66, 3.17) * mm, "end": v(13.66, 0) * mm});
            skLineSegment(sketch, "E180.0.3", {"start": v(13.66, 0) * mm, "end": v(17.16, 0) * mm});
            skLineSegment(sketch, "E181.0.0", {"start": v(-55.3, 0) * mm, "end": v(-48.91, 0) * mm});
            skLineSegment(sketch, "E181.0.1", {"start": v(-48.91, 0) * mm, "end": v(-48.91, 3.17) * mm});
            skLineSegment(sketch, "E181.0.2", {"start": v(-48.91, 3.18) * mm, "end": v(-55.3, 3.18) * mm});
            skLineSegment(sketch, "E181.0.3", {"start": v(-55.3, 3.18) * mm, "end": v(-55.3, 0) * mm});
            skLineSegment(sketch, "E182.0.0", {"start": v(-45.74, 0) * mm, "end": v(-42.24, 0) * mm});
            skLineSegment(sketch, "E182.0.1", {"start": v(-42.24, 0) * mm, "end": v(-42.24, 3.17) * mm});
            skLineSegment(sketch, "E182.0.2", {"start": v(-42.24, 3.18) * mm, "end": v(-45.74, 3.18) * mm});
            skLineSegment(sketch, "E182.0.3", {"start": v(-45.74, 3.17) * mm, "end": v(-45.74, 0) * mm});
            skLineSegment(sketch, "E183.0.0", {"start": v(-39.07, 0) * mm, "end": v(-35.57, 0) * mm});
            skLineSegment(sketch, "E183.0.1", {"start": v(-35.57, 0) * mm, "end": v(-35.57, 3.17) * mm});
            skLineSegment(sketch, "E183.0.2", {"start": v(-35.57, 3.18) * mm, "end": v(-39.07, 3.18) * mm});
            skLineSegment(sketch, "E183.0.3", {"start": v(-39.07, 3.17) * mm, "end": v(-39.07, 0) * mm});
            skLineSegment(sketch, "E184.0.0", {"start": v(-32.4, 0) * mm, "end": v(-28.9, 0) * mm});
            skLineSegment(sketch, "E184.0.1", {"start": v(-28.9, 0) * mm, "end": v(-28.9, 3.17) * mm});
            skLineSegment(sketch, "E184.0.2", {"start": v(-28.9, 3.18) * mm, "end": v(-32.4, 3.18) * mm});
            skLineSegment(sketch, "E184.0.3", {"start": v(-32.4, 3.17) * mm, "end": v(-32.4, 0) * mm});
            skLineSegment(sketch, "E185.0.0", {"start": v(-25.72, 0) * mm, "end": v(-22.23, 0) * mm});
            skLineSegment(sketch, "E185.0.1", {"start": v(-22.23, 0) * mm, "end": v(-22.23, 3.17) * mm});
            skLineSegment(sketch, "E185.0.2", {"start": v(-22.23, 3.18) * mm, "end": v(-25.72, 3.18) * mm});
            skLineSegment(sketch, "E185.0.3", {"start": v(-25.72, 3.17) * mm, "end": v(-25.72, 0) * mm});
            skLineSegment(sketch, "E186.0.0", {"start": v(-19.05, 0) * mm, "end": v(-15.56, 0) * mm});
            skLineSegment(sketch, "E186.0.1", {"start": v(-15.56, 0) * mm, "end": v(-15.56, 3.17) * mm});
            skLineSegment(sketch, "E186.0.2", {"start": v(-15.56, 3.18) * mm, "end": v(-19.05, 3.18) * mm});
            skLineSegment(sketch, "E186.0.3", {"start": v(-19.05, 3.17) * mm, "end": v(-19.05, 0) * mm});
            skPoint(sketch, "E187.0", {"position": v(-8.89, 1.59) * mm});
            skLineSegment(sketch, "E188.0.0", {"start": v(-5.71, 0) * mm, "end": v(-2.54, 0) * mm});
            skLineSegment(sketch, "E188.0.1", {"start": v(-2.54, 0) * mm, "end": v(-2.54, 3.17) * mm});
            skLineSegment(sketch, "E188.0.2", {"start": v(-2.54, 3.18) * mm, "end": v(-5.71, 3.18) * mm});
            skLineSegment(sketch, "E188.0.3", {"start": v(-5.71, 3.17) * mm, "end": v(-5.71, 0) * mm});
            skLineSegment(sketch, "E189.0.0", {"start": v(-12.38, 0) * mm, "end": v(-8.89, 0) * mm});
            skLineSegment(sketch, "E189.0.1", {"start": v(-8.89, 0) * mm, "end": v(-8.89, 3.17) * mm});
            skLineSegment(sketch, "E189.0.2", {"start": v(-8.89, 3.18) * mm, "end": v(-12.38, 3.18) * mm});
            skLineSegment(sketch, "E189.0.3", {"start": v(-12.38, 3.17) * mm, "end": v(-12.38, 0) * mm});
            skLineSegment(sketch, "E190.0.0", {"start": v(3.81, 0) * mm, "end": v(3.81, 3.17) * mm});
            skLineSegment(sketch, "E190.0.1", {"start": v(3.81, 3.18) * mm, "end": v(0.64, 3.18) * mm});
            skLineSegment(sketch, "E190.0.2", {"start": v(0.64, 3.17) * mm, "end": v(0.64, 0) * mm});
            skLineSegment(sketch, "E190.0.3", {"start": v(0.64, 0) * mm, "end": v(3.81, 0) * mm});
            skLineSegment(sketch, "E191.0.0", {"start": v(10.48, 0) * mm, "end": v(10.48, 3.17) * mm});
            skLineSegment(sketch, "E191.0.1", {"start": v(10.48, 3.18) * mm, "end": v(6.99, 3.18) * mm});
            skLineSegment(sketch, "E191.0.2", {"start": v(6.99, 3.17) * mm, "end": v(6.99, 0) * mm});
            skLineSegment(sketch, "E191.0.3", {"start": v(6.99, 0) * mm, "end": v(10.48, 0) * mm});
            skSolve(sketch);
        }
        {
            var Q0;
            Q0 = qSketchRegion(id + "F34", true);
            extrude(context, id + "F35", {"entities" : qUnion([Q0]), "operationType" : NewBodyOperationType.REMOVE, "oppositeDirection" : true, "depth" : 25.4 * mm, "offsetDistance" : 25.4 * mm});
        }
        {
            var Q0;
            Q0=makeQuery(id+"F8.opExtrude","SWEPT_FACE",FACE,{"disambiguationData":[OSD([sQuery(id+"F0.wireOp",EDGE,"E2")])]});
            var sketch = newSketch(context, id + "F36", { "sketchPlane" : qUnion([Q0])});
            skLineSegment(sketch, "E192.0.0", {"start": v(22.23, 3.17) * mm, "end": v(22.23, 0) * mm});
            skLineSegment(sketch, "E192.0.1", {"start": v(22.23, 0) * mm, "end": v(25.4, 0) * mm});
            skLineSegment(sketch, "E192.0.2", {"start": v(25.4, 0) * mm, "end": v(25.4, 3.18) * mm});
            skLineSegment(sketch, "E192.0.3", {"start": v(25.4, 3.18) * mm, "end": v(22.23, 3.18) * mm});
            skLineSegment(sketch, "E193.0.0", {"start": v(15.22, 3.17) * mm, "end": v(15.22, 0) * mm});
            skLineSegment(sketch, "E193.0.1", {"start": v(15.22, 0) * mm, "end": v(17.18, 0) * mm});
            skLineSegment(sketch, "E193.0.2", {"start": v(17.18, 0) * mm, "end": v(17.18, 3.17) * mm});
            skLineSegment(sketch, "E193.0.3", {"start": v(17.18, 3.18) * mm, "end": v(15.22, 3.18) * mm});
            skLineSegment(sketch, "E194.0.0", {"start": v(8.22, 3.17) * mm, "end": v(8.22, 0) * mm});
            skLineSegment(sketch, "E194.0.1", {"start": v(8.22, 0) * mm, "end": v(10.18, 0) * mm});
            skLineSegment(sketch, "E194.0.2", {"start": v(10.18, 0) * mm, "end": v(10.18, 3.17) * mm});
            skLineSegment(sketch, "E194.0.3", {"start": v(10.18, 3.18) * mm, "end": v(8.22, 3.18) * mm});
            skLineSegment(sketch, "E195.0.0", {"start": v(0, 3.17) * mm, "end": v(0, -47.62) * mm});
            skLineSegment(sketch, "E195.0.1", {"start": v(0, -47.63) * mm, "end": v(25.4, -47.63) * mm});
            skLineSegment(sketch, "E195.0.2", {"start": v(25.4, -47.62) * mm, "end": v(25.4, 3.17) * mm});
            skLineSegment(sketch, "E195.0.3", {"start": v(25.4, 3.18) * mm, "end": v(0, 3.18) * mm});
            skLineSegment(sketch, "E196.0.0", {"start": v(3.18, 0) * mm, "end": v(3.18, 3.17) * mm});
            skLineSegment(sketch, "E196.0.1", {"start": v(3.18, 3.18) * mm, "end": v(0, 3.18) * mm});
            skLineSegment(sketch, "E196.0.2", {"start": v(0, 3.18) * mm, "end": v(0, 0) * mm});
            skLineSegment(sketch, "E196.0.3", {"start": v(0, 0) * mm, "end": v(3.18, 0) * mm});
            skSolve(sketch);
        }
        {
            var Q0;
            Q0=makeQuery(id+"F36.imprint","IMPRINT",FACE,{"disambiguationData":[TD([[makeQuery(id+"F36.imprint","IMPRINT",EDGE,{"derivedFrom":sQuery(id+"F36.wireOp",EDGE,"E196.0.0")}),1.0]])]});
            var Q1;
            {var subQ0=sQuery(id+"F36.wireOp",EDGE,"E194.0.0");Q1=makeQuery(id+"F36.imprint","IMPRINT",FACE,{"disambiguationData":[TD([[makeQuery(id+"F36.imprint","IMPRINT",EDGE,{"derivedFrom":subQ0}),1.0]])]});}
            var Q2;
            {var subQ0=sQuery(id+"F36.wireOp",EDGE,"E193.0.0");Q2=makeQuery(id+"F36.imprint","IMPRINT",FACE,{"disambiguationData":[TD([[makeQuery(id+"F36.imprint","IMPRINT",EDGE,{"derivedFrom":subQ0}),1.0]])]});}
            var Q3;
            {var subQ0=sQuery(id+"F36.wireOp",EDGE,"E192.0.0");Q3=makeQuery(id+"F36.imprint","IMPRINT",FACE,{"disambiguationData":[TD([[makeQuery(id+"F36.imprint","IMPRINT",EDGE,{"derivedFrom":subQ0}),1.0]])]});}
            extrude(context, id + "F37", {"entities" : qUnion([Q0, Q1, Q2, Q3]), "operationType" : NewBodyOperationType.REMOVE, "oppositeDirection" : true, "depth" : 25.4 * mm, "offsetDistance" : 25.4 * mm});
        }
        {
            var Q0;
            Q0=makeQuery(id+"F9.opExtrude","SWEPT_FACE",FACE,{"disambiguationData":[OSD([sQuery(id+"F0.wireOp",EDGE,"E3")])]});
            var sketch = newSketch(context, id + "F38", { "sketchPlane" : qUnion([Q0])});
            skLineSegment(sketch, "E197.0.0", {"start": v(12.47, 3.17) * mm, "end": v(12.47, 0) * mm});
            skLineSegment(sketch, "E197.0.1", {"start": v(12.47, 0) * mm, "end": v(15.65, 0) * mm});
            skLineSegment(sketch, "E197.0.2", {"start": v(15.65, 0) * mm, "end": v(15.65, 3.18) * mm});
            skLineSegment(sketch, "E197.0.3", {"start": v(15.65, 3.18) * mm, "end": v(12.47, 3.18) * mm});
            skLineSegment(sketch, "E198.0.0", {"start": v(1.53, 3.17) * mm, "end": v(1.53, 0) * mm});
            skLineSegment(sketch, "E198.0.1", {"start": v(1.53, 0) * mm, "end": v(8.96, 0) * mm});
            skLineSegment(sketch, "E198.0.2", {"start": v(8.96, 0) * mm, "end": v(8.96, 3.17) * mm});
            skLineSegment(sketch, "E198.0.3", {"start": v(8.96, 3.18) * mm, "end": v(1.53, 3.18) * mm});
            skLineSegment(sketch, "E199.0.0", {"start": v(-9.42, 3.17) * mm, "end": v(-9.42, 0) * mm});
            skLineSegment(sketch, "E199.0.1", {"start": v(-9.42, 0) * mm, "end": v(-1.98, 0) * mm});
            skLineSegment(sketch, "E199.0.2", {"start": v(-1.98, 0) * mm, "end": v(-1.98, 3.17) * mm});
            skLineSegment(sketch, "E199.0.3", {"start": v(-1.98, 3.18) * mm, "end": v(-9.42, 3.18) * mm});
            skLineSegment(sketch, "E200.0.0", {"start": v(-12.93, 0) * mm, "end": v(-12.93, 3.17) * mm});
            skLineSegment(sketch, "E200.0.1", {"start": v(-12.93, 3.18) * mm, "end": v(-16.1, 3.18) * mm});
            skLineSegment(sketch, "E200.0.2", {"start": v(-16.1, 3.18) * mm, "end": v(-16.1, 0) * mm});
            skLineSegment(sketch, "E200.0.3", {"start": v(-16.1, 0) * mm, "end": v(-12.93, 0) * mm});
            skSolve(sketch);
        }
        {
            var Q0;
            {var subQ3=sQuery(id+"F38.wireOp",EDGE,"E197.0.0");Q0=makeQuery(id+"F38.imprint","IMPRINT",FACE,{"disambiguationData":[TD([[makeQuery(id+"F38.imprint","IMPRINT",EDGE,{"derivedFrom":subQ3}),-1.0]])]});}
            var sketch = newSketch(context, id + "F39", { "sketchPlane" : qUnion([Q0])});
            skLineSegment(sketch, "E201.0.0", {"start": v(12.47, 3.18) * mm, "end": v(12.47, 0) * mm});
            skLineSegment(sketch, "E201.0.1", {"start": v(12.47, 0) * mm, "end": v(15.65, 0) * mm});
            skLineSegment(sketch, "E201.0.2", {"start": v(15.65, 0) * mm, "end": v(15.65, 3.17) * mm});
            skLineSegment(sketch, "E201.0.3", {"start": v(15.65, 3.18) * mm, "end": v(12.47, 3.18) * mm});
            skLineSegment(sketch, "E202.0.0", {"start": v(1.53, 0) * mm, "end": v(8.96, 0) * mm});
            skLineSegment(sketch, "E202.0.1", {"start": v(8.96, 0) * mm, "end": v(8.96, 3.18) * mm});
            skLineSegment(sketch, "E202.0.2", {"start": v(8.96, 3.18) * mm, "end": v(1.53, 3.18) * mm});
            skLineSegment(sketch, "E202.0.3", {"start": v(1.53, 3.18) * mm, "end": v(1.53, 0) * mm});
            skLineSegment(sketch, "E203.0.0", {"start": v(-9.42, 0) * mm, "end": v(-1.98, 0) * mm});
            skLineSegment(sketch, "E203.0.1", {"start": v(-1.98, 0) * mm, "end": v(-1.98, 3.18) * mm});
            skLineSegment(sketch, "E203.0.2", {"start": v(-1.98, 3.18) * mm, "end": v(-9.42, 3.18) * mm});
            skLineSegment(sketch, "E203.0.3", {"start": v(-9.42, 3.18) * mm, "end": v(-9.42, 0) * mm});
            skLineSegment(sketch, "E204.0.0", {"start": v(-16.1, 3.17) * mm, "end": v(-16.1, 0) * mm});
            skLineSegment(sketch, "E204.0.1", {"start": v(-16.1, 0) * mm, "end": v(-12.93, 0) * mm});
            skLineSegment(sketch, "E204.0.2", {"start": v(-12.93, 0) * mm, "end": v(-12.93, 3.18) * mm});
            skLineSegment(sketch, "E204.0.3", {"start": v(-12.93, 3.18) * mm, "end": v(-16.1, 3.18) * mm});
            skSolve(sketch);
        }
        {
            var Q0;
            Q0 = qSketchRegion(id + "F39", true);
            extrude(context, id + "F40", {"entities" : qUnion([Q0]), "operationType" : NewBodyOperationType.REMOVE, "oppositeDirection" : true, "depth" : 25.4 * mm, "offsetDistance" : 25.4 * mm});
        }
        {
            var Q0;
            Q0=makeQuery(id+"F10.opExtrude","SWEPT_FACE",FACE,{"disambiguationData":[OSD([sQuery(id+"F0.wireOp",EDGE,"E4")])]});
            var sketch = newSketch(context, id + "F41", { "sketchPlane" : qUnion([Q0])});
            skLineSegment(sketch, "E205.0.0", {"start": v(-25.4, 3.17) * mm, "end": v(-25.4, 0) * mm});
            skLineSegment(sketch, "E205.0.1", {"start": v(-25.4, 0) * mm, "end": v(-22.23, 0) * mm});
            skLineSegment(sketch, "E205.0.2", {"start": v(-22.23, 0) * mm, "end": v(-22.23, 3.18) * mm});
            skLineSegment(sketch, "E205.0.3", {"start": v(-22.23, 3.18) * mm, "end": v(-25.4, 3.18) * mm});
            skLineSegment(sketch, "E206.0.0", {"start": v(-38.1, 3.17) * mm, "end": v(-38.1, 0) * mm});
            skLineSegment(sketch, "E206.0.1", {"start": v(-38.1, 0) * mm, "end": v(-31.75, 0) * mm});
            skLineSegment(sketch, "E206.0.2", {"start": v(-31.75, 0) * mm, "end": v(-31.75, 3.17) * mm});
            skLineSegment(sketch, "E206.0.3", {"start": v(-31.75, 3.18) * mm, "end": v(-38.1, 3.18) * mm});
            skLineSegment(sketch, "E207.0.0", {"start": v(-50.8, 3.17) * mm, "end": v(-50.8, 0) * mm});
            skLineSegment(sketch, "E207.0.1", {"start": v(-50.8, 0) * mm, "end": v(-44.45, 0) * mm});
            skLineSegment(sketch, "E207.0.2", {"start": v(-44.45, 0) * mm, "end": v(-44.45, 3.17) * mm});
            skLineSegment(sketch, "E207.0.3", {"start": v(-44.45, 3.18) * mm, "end": v(-50.8, 3.18) * mm});
            skLineSegment(sketch, "E208.0.0", {"start": v(-57.15, 0) * mm, "end": v(-57.15, 3.17) * mm});
            skLineSegment(sketch, "E208.0.1", {"start": v(-57.15, 3.18) * mm, "end": v(-60.32, 3.18) * mm});
            skLineSegment(sketch, "E208.0.2", {"start": v(-60.33, 3.18) * mm, "end": v(-60.33, 0) * mm});
            skLineSegment(sketch, "E208.0.3", {"start": v(-60.32, 0) * mm, "end": v(-57.15, 0) * mm});
            skSolve(sketch);
        }
        {
            var Q0;
            Q0 = qSketchRegion(id + "F41", true);
            extrude(context, id + "F42", {"entities" : qUnion([Q0]), "operationType" : NewBodyOperationType.REMOVE, "oppositeDirection" : true, "depth" : 25.4 * mm, "offsetDistance" : 25.4 * mm});
        }
        {
            var Q0;
            Q0=makeQuery(id+"F11.opExtrude","SWEPT_FACE",FACE,{"disambiguationData":[OSD([sQuery(id+"F0.wireOp",EDGE,"E5"),sQuery(id+"F2.wireOp",EDGE,"E45")])]});
            var sketch = newSketch(context, id + "F43", { "sketchPlane" : qUnion([Q0])});
            skLineSegment(sketch, "E209.0.0", {"start": v(-22.83, 3.17) * mm, "end": v(-22.83, 0) * mm});
            skLineSegment(sketch, "E209.0.1", {"start": v(-22.83, 0) * mm, "end": v(-19.66, 0) * mm});
            skLineSegment(sketch, "E209.0.2", {"start": v(-19.66, 0) * mm, "end": v(-19.66, 3.18) * mm});
            skLineSegment(sketch, "E209.0.3", {"start": v(-19.66, 3.18) * mm, "end": v(-22.83, 3.18) * mm});
            skLineSegment(sketch, "E210.0.0", {"start": v(-30.77, 3.17) * mm, "end": v(-30.77, 0) * mm});
            skLineSegment(sketch, "E210.0.1", {"start": v(-30.77, 0) * mm, "end": v(-26, 0) * mm});
            skLineSegment(sketch, "E210.0.2", {"start": v(-26, 0) * mm, "end": v(-26, 3.17) * mm});
            skLineSegment(sketch, "E210.0.3", {"start": v(-26, 3.18) * mm, "end": v(-30.77, 3.18) * mm});
            skLineSegment(sketch, "E211.0.0", {"start": v(-38.7, 3.17) * mm, "end": v(-38.7, 0) * mm});
            skLineSegment(sketch, "E211.0.1", {"start": v(-38.7, 0) * mm, "end": v(-33.94, 0) * mm});
            skLineSegment(sketch, "E211.0.2", {"start": v(-33.94, 0) * mm, "end": v(-33.94, 3.17) * mm});
            skLineSegment(sketch, "E211.0.3", {"start": v(-33.94, 3.18) * mm, "end": v(-38.7, 3.18) * mm});
            skLineSegment(sketch, "E212.0.0", {"start": v(-41.88, 0) * mm, "end": v(-41.88, 3.17) * mm});
            skLineSegment(sketch, "E212.0.1", {"start": v(-41.88, 3.18) * mm, "end": v(-45.06, 3.18) * mm});
            skLineSegment(sketch, "E212.0.2", {"start": v(-45.06, 3.18) * mm, "end": v(-45.06, 0) * mm});
            skLineSegment(sketch, "E212.0.3", {"start": v(-45.06, 0) * mm, "end": v(-41.88, 0) * mm});
            skSolve(sketch);
        }
        {
            var Q0;
            Q0 = qSketchRegion(id + "F43", true);
            extrude(context, id + "F44", {"entities" : qUnion([Q0]), "operationType" : NewBodyOperationType.REMOVE, "oppositeDirection" : true, "depth" : 25.4 * mm, "offsetDistance" : 25.4 * mm});
        }
        {
            var Q0;
            Q0=makeQuery(id+"F12.opExtrude","SWEPT_FACE",FACE,{"disambiguationData":[OSD([sQuery(id+"F0.wireOp",EDGE,"E6"),sQuery(id+"F2.wireOp",EDGE,"E40")])]});
            var sketch = newSketch(context, id + "F45", { "sketchPlane" : qUnion([Q0])});
            skLineSegment(sketch, "E213.0.0", {"start": v(41.88, 3.17) * mm, "end": v(41.88, 0) * mm});
            skLineSegment(sketch, "E213.0.1", {"start": v(41.88, 0) * mm, "end": v(45.06, 0) * mm});
            skLineSegment(sketch, "E213.0.2", {"start": v(45.06, 0) * mm, "end": v(45.06, 3.18) * mm});
            skLineSegment(sketch, "E213.0.3", {"start": v(45.06, 3.18) * mm, "end": v(41.88, 3.18) * mm});
            skLineSegment(sketch, "E214.0.0", {"start": v(33.94, 0) * mm, "end": v(38.7, 0) * mm});
            skLineSegment(sketch, "E214.0.1", {"start": v(38.7, 0) * mm, "end": v(38.7, 3.17) * mm});
            skLineSegment(sketch, "E214.0.2", {"start": v(38.7, 3.18) * mm, "end": v(33.94, 3.18) * mm});
            skLineSegment(sketch, "E214.0.3", {"start": v(33.94, 3.17) * mm, "end": v(33.94, 0) * mm});
            skLineSegment(sketch, "E215.0.0", {"start": v(26, 0) * mm, "end": v(30.77, 0) * mm});
            skLineSegment(sketch, "E215.0.1", {"start": v(30.77, 0) * mm, "end": v(30.77, 3.17) * mm});
            skLineSegment(sketch, "E215.0.2", {"start": v(30.77, 3.18) * mm, "end": v(26, 3.18) * mm});
            skLineSegment(sketch, "E215.0.3", {"start": v(26, 3.17) * mm, "end": v(26, 0) * mm});
            skLineSegment(sketch, "E216.0.0", {"start": v(19.66, 0) * mm, "end": v(22.83, 0) * mm});
            skLineSegment(sketch, "E216.0.1", {"start": v(22.83, 0) * mm, "end": v(22.83, 3.17) * mm});
            skLineSegment(sketch, "E216.0.2", {"start": v(22.83, 3.18) * mm, "end": v(19.66, 3.18) * mm});
            skLineSegment(sketch, "E216.0.3", {"start": v(19.66, 3.18) * mm, "end": v(19.66, 0) * mm});
            skSolve(sketch);
        }
        {
            var Q0;
            Q0 = qSketchRegion(id + "F45", true);
            extrude(context, id + "F46", {"entities" : qUnion([Q0]), "operationType" : NewBodyOperationType.REMOVE, "oppositeDirection" : true, "depth" : 25.4 * mm, "offsetDistance" : 25.4 * mm});
        }
        {
            var Q0;
            Q0=makeQuery(id+"F6.opExtrude","CAP_FACE",FACE,{"disambiguationData":[OSD([sQuery(id+"F0.wireOp",EDGE,"E0"),sQuery(id+"F0.wireOp",EDGE,"E1"),sQuery(id+"F2.wireOp",EDGE,"E13"),sQuery(id+"F2.wireOp",EDGE,"E14")])],"isStart":false});
            var sketch = newSketch(context, id + "F47", { "sketchPlane" : qUnion([Q0])});
            skLineSegment(sketch, "E217", {"start": v(0, 73.01) * mm, "end": v(-2.26, 75.24) * mm});
            skLineSegment(sketch, "E218.0", {"start": v(-73.94, -2.23) * mm, "end": v(2.23, 75.28) * mm});
            skLineSegment(sketch, "E219.0", {"start": v(-2.23, 75.28) * mm, "end": v(73.94, -2.23) * mm});
            skSolve(sketch);
        }
        {
            var Q0;
            Q0=makeQuery(id+"F6.opExtrude","SWEPT_FACE",FACE,{"disambiguationData":[OSD([sQuery(id+"F0.wireOp",EDGE,"E0")])]});
            var sketch = newSketch(context, id + "F48", { "sketchPlane" : qUnion([Q0])});
            skLineSegment(sketch, "E220.bottom", {"start": v(55.3, -40.48) * mm, "end": v(52.08, -40.48) * mm});
            skLineSegment(sketch, "E220.top", {"start": v(55.3, -34.13) * mm, "end": v(52.08, -34.13) * mm});
            skLineSegment(sketch, "E220.left", {"start": v(55.3, -40.48) * mm, "end": v(55.3, -34.13) * mm});
            skLineSegment(sketch, "E220.right", {"start": v(52.08, -40.48) * mm, "end": v(52.08, -34.13) * mm});
            skLineSegment(sketch, "E221.bottom", {"start": v(55.3, -26.99) * mm, "end": v(52.08, -26.99) * mm});
            skLineSegment(sketch, "E221.top", {"start": v(55.3, -20.64) * mm, "end": v(52.08, -20.64) * mm});
            skLineSegment(sketch, "E221.left", {"start": v(55.3, -26.99) * mm, "end": v(55.3, -20.64) * mm});
            skLineSegment(sketch, "E221.right", {"start": v(52.08, -26.99) * mm, "end": v(52.08, -20.64) * mm});
            skLineSegment(sketch, "E222.bottom", {"start": v(55.3, -13.5) * mm, "end": v(52.08, -13.5) * mm});
            skLineSegment(sketch, "E222.top", {"start": v(55.3, -7.14) * mm, "end": v(52.08, -7.14) * mm});
            skLineSegment(sketch, "E222.left", {"start": v(55.3, -13.5) * mm, "end": v(55.3, -7.14) * mm});
            skLineSegment(sketch, "E222.right", {"start": v(52.08, -13.5) * mm, "end": v(52.08, -7.14) * mm});
            skLineSegment(sketch, "E223", {"start": v(53.7, -34.13) * mm, "end": v(53.7, -26.99) * mm, "construction": true});
            skLineSegment(sketch, "E224", {"start": v(53.7, -20.64) * mm, "end": v(53.7, -13.5) * mm, "construction": true});
            skLineSegment(sketch, "E225", {"start": v(53.7, -7.14) * mm, "end": v(53.7, 0) * mm, "construction": true});
            skLineSegment(sketch, "E226", {"start": v(53.7, -47.63) * mm, "end": v(53.7, -40.48) * mm, "construction": true});
            skSolve(sketch);
        }
        {
            var Q0;
            Q0=makeQuery(id+"F48.imprint","IMPRINT",FACE,{"disambiguationData":[TD([[makeQuery(id+"F48.imprint","IMPRINT",EDGE,{"derivedFrom":sQuery(id+"F48.wireOp",EDGE,"E220.bottom")}),-1.0]])]});
            var Q1;
            Q1=makeQuery(id+"F48.imprint","IMPRINT",FACE,{"disambiguationData":[TD([[makeQuery(id+"F48.imprint","IMPRINT",EDGE,{"derivedFrom":sQuery(id+"F48.wireOp",EDGE,"E221.bottom")}),-1.0]])]});
            var Q2;
            Q2=makeQuery(id+"F48.imprint","IMPRINT",FACE,{"disambiguationData":[TD([[makeQuery(id+"F48.imprint","IMPRINT",EDGE,{"derivedFrom":sQuery(id+"F48.wireOp",EDGE,"E222.bottom")}),-1.0]])]});
            extrude(context, id + "F49", {"entities" : qUnion([Q0, Q1, Q2]), "operationType" : NewBodyOperationType.REMOVE, "oppositeDirection" : true, "depth" : 25.4 * mm, "offsetDistance" : 25.4 * mm});
        }
        {
            var Q0;
            Q0=makeQuery(id+"F7.opExtrude","CAP_FACE",FACE,{"disambiguationData":[OSD([sQuery(id+"F0.wireOp",EDGE,"E0"),sQuery(id+"F0.wireOp",EDGE,"E1"),sQuery(id+"F2.wireOp",EDGE,"E35"),sQuery(id+"F2.wireOp",EDGE,"E36")])],"isStart":false});
            var sketch = newSketch(context, id + "F50", { "sketchPlane" : qUnion([Q0])});
            skLineSegment(sketch, "E227.0.0", {"start": v(76.2, 0) * mm, "end": v(0, 77.54) * mm});
            skLineSegment(sketch, "E227.0.1", {"start": v(0, 77.54) * mm, "end": v(-2.23, 75.28) * mm});
            skLineSegment(sketch, "E227.0.2", {"start": v(-2.23, 75.28) * mm, "end": v(73.94, -2.23) * mm});
            skLineSegment(sketch, "E227.0.3", {"start": v(73.94, -2.23) * mm, "end": v(76.2, 0) * mm});
            skLineSegment(sketch, "E228.0.0", {"start": v(0, 77.54) * mm, "end": v(-76.2, 0) * mm});
            skLineSegment(sketch, "E228.0.1", {"start": v(-76.2, 0) * mm, "end": v(-73.94, -2.23) * mm});
            skLineSegment(sketch, "E228.0.2", {"start": v(-73.94, -2.23) * mm, "end": v(2.23, 75.28) * mm});
            skLineSegment(sketch, "E228.0.3", {"start": v(2.23, 75.28) * mm, "end": v(0, 77.54) * mm});
            skLineSegment(sketch, "E229", {"start": v(0, 73.01) * mm, "end": v(2.26, 75.24) * mm});
            skSolve(sketch);
        }
        {
            var Q0;
            Q0=makeQuery(id+"F7.opExtrude","SWEPT_FACE",FACE,{"disambiguationData":[OSD([sQuery(id+"F0.wireOp",EDGE,"E1")])]});
            var sketch = newSketch(context, id + "F51", { "sketchPlane" : qUnion([Q0])});
            skLineSegment(sketch, "E230.0.0", {"start": v(-52.13, -47.62) * mm, "end": v(-52.13, -40.48) * mm});
            skLineSegment(sketch, "E230.0.1", {"start": v(-52.08, -40.48) * mm, "end": v(-55.3, -40.48) * mm});
            skLineSegment(sketch, "E230.0.2", {"start": v(-55.3, -40.48) * mm, "end": v(-55.3, -47.62) * mm});
            skLineSegment(sketch, "E230.0.3", {"start": v(-55.3, -47.63) * mm, "end": v(-52.08, -47.63) * mm});
            skLineSegment(sketch, "E231.0.0", {"start": v(-55.3, -34.13) * mm, "end": v(-52.08, -34.13) * mm});
            skLineSegment(sketch, "E231.0.1", {"start": v(-52.13, -34.13) * mm, "end": v(-52.13, -26.99) * mm});
            skLineSegment(sketch, "E231.0.2", {"start": v(-52.08, -26.99) * mm, "end": v(-55.3, -26.99) * mm});
            skLineSegment(sketch, "E231.0.3", {"start": v(-55.3, -26.99) * mm, "end": v(-55.3, -34.13) * mm});
            skLineSegment(sketch, "E232.0.0", {"start": v(-55.3, -20.64) * mm, "end": v(-52.08, -20.64) * mm});
            skLineSegment(sketch, "E232.0.1", {"start": v(-52.13, -20.64) * mm, "end": v(-52.13, -13.5) * mm});
            skLineSegment(sketch, "E232.0.2", {"start": v(-52.08, -13.5) * mm, "end": v(-55.3, -13.5) * mm});
            skLineSegment(sketch, "E232.0.3", {"start": v(-55.3, -13.5) * mm, "end": v(-55.3, -20.64) * mm});
            skLineSegment(sketch, "E233.0.0", {"start": v(-55.3, -7.14) * mm, "end": v(-52.08, -7.14) * mm});
            skLineSegment(sketch, "E233.0.1", {"start": v(-52.13, -7.14) * mm, "end": v(-52.13, 0) * mm});
            skLineSegment(sketch, "E233.0.2", {"start": v(-52.08, 0) * mm, "end": v(-55.3, 0) * mm});
            skLineSegment(sketch, "E233.0.3", {"start": v(-55.3, 0) * mm, "end": v(-55.3, -7.14) * mm});
            skPoint(sketch, "E234.0", {"position": v(-52.08, -47.62) * mm});
            skLineSegment(sketch, "E235", {"start": v(-52.08, -47.62) * mm, "end": v(-52.08, 0) * mm});
            skSolve(sketch);
        }
        {
            var Q0;
            {var subQ2=sQuery(id+"F51.wireOp",EDGE,"E233.0.1");Q0=makeQuery(id+"F51.imprint","IMPRINT",FACE,{"disambiguationData":[TD([[makeQuery(id+"F51.imprint","IMPRINT",EDGE,{"derivedFrom":subQ2}),1.0]])]});}
            var Q1;
            {var subQ3=sQuery(id+"F51.wireOp",EDGE,"E233.0.1");Q1=makeQuery(id+"F51.imprint","IMPRINT",FACE,{"disambiguationData":[TD([[makeQuery(id+"F51.imprint","IMPRINT",EDGE,{"derivedFrom":subQ3}),-1.0]])]});}
            var Q2;
            {var subQ3=sQuery(id+"F51.wireOp",EDGE,"E232.0.1");Q2=makeQuery(id+"F51.imprint","IMPRINT",FACE,{"disambiguationData":[TD([[makeQuery(id+"F51.imprint","IMPRINT",EDGE,{"derivedFrom":subQ3}),1.0]])]});}
            var Q3;
            {var subQ3=sQuery(id+"F51.wireOp",EDGE,"E232.0.1");Q3=makeQuery(id+"F51.imprint","IMPRINT",FACE,{"disambiguationData":[TD([[makeQuery(id+"F51.imprint","IMPRINT",EDGE,{"derivedFrom":subQ3}),-1.0]])]});}
            var Q4;
            {var subQ3=sQuery(id+"F51.wireOp",EDGE,"E231.0.1");Q4=makeQuery(id+"F51.imprint","IMPRINT",FACE,{"disambiguationData":[TD([[makeQuery(id+"F51.imprint","IMPRINT",EDGE,{"derivedFrom":subQ3}),1.0]])]});}
            var Q5;
            {var subQ3=sQuery(id+"F51.wireOp",EDGE,"E231.0.1");Q5=makeQuery(id+"F51.imprint","IMPRINT",FACE,{"disambiguationData":[TD([[makeQuery(id+"F51.imprint","IMPRINT",EDGE,{"derivedFrom":subQ3}),-1.0]])]});}
            var Q6;
            {var subQ0=sQuery(id+"F51.wireOp",EDGE,"E230.0.0");Q6=makeQuery(id+"F51.imprint","IMPRINT",FACE,{"disambiguationData":[TD([[makeQuery(id+"F51.imprint","IMPRINT",EDGE,{"derivedFrom":subQ0}),1.0]])]});}
            var Q7;
            {var subQ0=sQuery(id+"F51.wireOp",EDGE,"E230.0.0");Q7=makeQuery(id+"F51.imprint","IMPRINT",FACE,{"disambiguationData":[TD([[makeQuery(id+"F51.imprint","IMPRINT",EDGE,{"derivedFrom":subQ0}),-1.0]])]});}
            extrude(context, id + "F52", {"entities" : qUnion([Q0, Q1, Q2, Q3, Q4, Q5, Q6, Q7]), "operationType" : NewBodyOperationType.REMOVE, "oppositeDirection" : true, "depth" : 25.4 * mm, "offsetDistance" : 25.4 * mm});
        }
        {
            var Q0;
            {var subQ0=sQuery(id+"F50.wireOp",EDGE,"E227.0.3");Q0=makeQuery(id+"F50.imprint","IMPRINT",FACE,{"disambiguationData":[TD([[makeQuery(id+"F50.imprint","IMPRINT",EDGE,{"derivedFrom":subQ0}),1.0]])]});}
            var sketch = newSketch(context, id + "F53", { "sketchPlane" : qUnion([Q0])});
            skLineSegment(sketch, "E236.0.0", {"start": v(73.03, -25.4) * mm, "end": v(76.2, -25.4) * mm});
            skLineSegment(sketch, "E236.0.1", {"start": v(76.2, -25.4) * mm, "end": v(76.2, 0) * mm});
            skLineSegment(sketch, "E236.0.2", {"start": v(76.2, 0) * mm, "end": v(73.03, 0) * mm});
            skLineSegment(sketch, "E236.0.3", {"start": v(73.03, 0) * mm, "end": v(73.03, -25.4) * mm});
            skLineSegment(sketch, "E237.0.0", {"start": v(2.26, 75.24) * mm, "end": v(0, 73.01) * mm});
            skLineSegment(sketch, "E237.0.1", {"start": v(0, 73.01) * mm, "end": v(73.94, -2.23) * mm});
            skLineSegment(sketch, "E237.0.2", {"start": v(73.94, -2.23) * mm, "end": v(76.2, 0) * mm});
            skLineSegment(sketch, "E237.0.3", {"start": v(76.2, 0) * mm, "end": v(2.26, 75.24) * mm});
            skLineSegment(sketch, "E238", {"start": v(72.38, -0.64) * mm, "end": v(74.64, 1.59) * mm});
            skSolve(sketch);
        }
        {
            var Q0;
            Q0=makeQuery(id+"F7.opExtrude","SWEPT_FACE",FACE,{"disambiguationData":[OSD([sQuery(id+"F0.wireOp",EDGE,"E1")])]});
            var sketch = newSketch(context, id + "F54", { "sketchPlane" : qUnion([Q0])});
            skLineSegment(sketch, "E239.0", {"start": v(53.4, -40.48) * mm, "end": v(-55.3, -40.48) * mm});
            skLineSegment(sketch, "E240.0", {"start": v(53.4, -34.13) * mm, "end": v(-55.3, -34.13) * mm});
            skLineSegment(sketch, "E241.0", {"start": v(53.4, -26.99) * mm, "end": v(-55.3, -26.99) * mm});
            skLineSegment(sketch, "E242.0.0", {"start": v(-55.3, -34.13) * mm, "end": v(-52.13, -34.13) * mm});
            skLineSegment(sketch, "E242.0.1", {"start": v(-52.13, -34.13) * mm, "end": v(-52.13, -26.99) * mm});
            skLineSegment(sketch, "E242.0.2", {"start": v(-52.13, -26.99) * mm, "end": v(-55.3, -26.99) * mm});
            skLineSegment(sketch, "E242.0.3", {"start": v(-55.3, -26.99) * mm, "end": v(-55.3, -34.13) * mm});
            skLineSegment(sketch, "E243.0.0", {"start": v(-52.13, -47.62) * mm, "end": v(-52.13, -40.48) * mm});
            skLineSegment(sketch, "E243.0.1", {"start": v(-52.13, -40.48) * mm, "end": v(-55.3, -40.48) * mm});
            skLineSegment(sketch, "E243.0.2", {"start": v(-55.3, -40.48) * mm, "end": v(-55.3, -47.62) * mm});
            skLineSegment(sketch, "E243.0.3", {"start": v(-55.3, -47.63) * mm, "end": v(53.4, -47.63) * mm});
            skLineSegment(sketch, "E244.0.0", {"start": v(-55.3, -20.64) * mm, "end": v(53.4, -20.64) * mm});
            skLineSegment(sketch, "E244.0.1", {"start": v(-52.13, -20.64) * mm, "end": v(-52.13, -13.5) * mm});
            skLineSegment(sketch, "E244.0.2", {"start": v(53.4, -13.5) * mm, "end": v(-55.3, -13.5) * mm});
            skLineSegment(sketch, "E244.0.3", {"start": v(-55.3, -13.5) * mm, "end": v(-55.3, -20.64) * mm});
            skLineSegment(sketch, "E245.0.0", {"start": v(-55.3, -7.14) * mm, "end": v(53.4, -7.14) * mm});
            skLineSegment(sketch, "E245.0.1", {"start": v(-52.13, -7.14) * mm, "end": v(-52.13, 0) * mm});
            skLineSegment(sketch, "E245.0.2", {"start": v(53.4, 0) * mm, "end": v(-55.3, 0) * mm});
            skLineSegment(sketch, "E245.0.3", {"start": v(-55.3, 0) * mm, "end": v(-55.3, -7.14) * mm});
            skLineSegment(sketch, "E246.0", {"start": v(53.4, -47.62) * mm, "end": v(53.4, 0) * mm});
            skPoint(sketch, "E247.0", {"position": v(51.18, -47.62) * mm});
            skLineSegment(sketch, "E248", {"start": v(51.18, -47.62) * mm, "end": v(51.18, 0) * mm});
            skSolve(sketch);
        }
        {
            var Q0;
            {var subQ0=sQuery(id+"F54.wireOp",EDGE,"E246.0");var subQ1=sQuery(id+"F54.wireOp",EDGE,"E239.0");var subQ2=makeQuery(id+"F54.imprint","INTERSECT",VERTEX,{"derivedFrom":[subQ1,subQ0]});Q0=makeQuery(id+"F54.imprint","IMPRINT",FACE,{"disambiguationData":[TD([[makeQuery(id+"F54.imprint","IMPRINT",EDGE,{"disambiguationData":[TD([[subQ2,-1.0]])],"derivedFrom":subQ1}),-1.0]])]});}
            var Q1;
            {var subQ0=sQuery(id+"F54.wireOp",EDGE,"E246.0");var subQ1=sQuery(id+"F54.wireOp",EDGE,"E241.0");var subQ2=makeQuery(id+"F54.imprint","INTERSECT",VERTEX,{"derivedFrom":[subQ1,subQ0]});Q1=makeQuery(id+"F54.imprint","IMPRINT",FACE,{"disambiguationData":[TD([[makeQuery(id+"F54.imprint","IMPRINT",EDGE,{"disambiguationData":[TD([[subQ2,-1.0]])],"derivedFrom":subQ1}),-1.0]])]});}
            var Q2;
            {var subQ0=sQuery(id+"F54.wireOp",EDGE,"E246.0");var subQ1=sQuery(id+"F54.wireOp",EDGE,"E244.0.2");var subQ2=makeQuery(id+"F54.imprint","INTERSECT",VERTEX,{"derivedFrom":[subQ1,subQ0]});Q2=makeQuery(id+"F54.imprint","IMPRINT",FACE,{"disambiguationData":[TD([[makeQuery(id+"F54.imprint","IMPRINT",EDGE,{"disambiguationData":[TD([[subQ2,-1.0]])],"derivedFrom":subQ1}),-1.0]])]});}
            extrude(context, id + "F55", {"entities" : qUnion([Q0, Q1, Q2]), "operationType" : NewBodyOperationType.REMOVE, "oppositeDirection" : true, "depth" : 25.4 * mm, "offsetDistance" : 25.4 * mm});
        }
        {
            var Q0;
            {var subQ4=sQuery(id+"F53.wireOp",EDGE,"E236.0.0");Q0=makeQuery(id+"F53.imprint","IMPRINT",FACE,{"disambiguationData":[TD([[makeQuery(id+"F53.imprint","IMPRINT",EDGE,{"derivedFrom":subQ4}),1.0]])]});}
            var sketch = newSketch(context, id + "F56", { "sketchPlane" : qUnion([Q0])});
            skLineSegment(sketch, "E249.0.0", {"start": v(73.94, -2.23) * mm, "end": v(73.03, -1.3) * mm});
            skLineSegment(sketch, "E249.0.1", {"start": v(73.03, -1.3) * mm, "end": v(73.03, -25.4) * mm});
            skLineSegment(sketch, "E249.0.2", {"start": v(73.03, -25.4) * mm, "end": v(76.2, -25.4) * mm});
            skLineSegment(sketch, "E249.0.3", {"start": v(76.2, -25.4) * mm, "end": v(76.2, 0) * mm});
            skLineSegment(sketch, "E249.0.4", {"start": v(76.2, 0) * mm, "end": v(73.94, -2.23) * mm});
            skLineSegment(sketch, "E250.0.0", {"start": v(76.2, 0) * mm, "end": v(73.03, 0) * mm});
            skLineSegment(sketch, "E250.0.1", {"start": v(73.03, 0) * mm, "end": v(73.03, -1.3) * mm});
            skLineSegment(sketch, "E250.0.2", {"start": v(73.03, -1.3) * mm, "end": v(73.94, -2.23) * mm});
            skLineSegment(sketch, "E250.0.3", {"start": v(73.94, -2.23) * mm, "end": v(76.2, 0) * mm});
            skLineSegment(sketch, "E251", {"start": v(73.03, -2.23) * mm, "end": v(76.2, -2.23) * mm});
            skSolve(sketch);
        }
        {
            var Q0;
            Q0=makeQuery(id+"F8.opExtrude","SWEPT_FACE",FACE,{"disambiguationData":[OSD([sQuery(id+"F0.wireOp",EDGE,"E2")])]});
            var sketch = newSketch(context, id + "F57", { "sketchPlane" : qUnion([Q0])});
            skLineSegment(sketch, "E252.0.0", {"start": v(2.23, -47.62) * mm, "end": v(2.23, -40.48) * mm});
            skLineSegment(sketch, "E252.0.1", {"start": v(2.23, -40.48) * mm, "end": v(0, -40.48) * mm});
            skLineSegment(sketch, "E252.0.2", {"start": v(0, -40.48) * mm, "end": v(0, -47.62) * mm});
            skLineSegment(sketch, "E252.0.3", {"start": v(0, -47.63) * mm, "end": v(2.23, -47.63) * mm});
            skLineSegment(sketch, "E253.0.0", {"start": v(0, -34.13) * mm, "end": v(2.23, -34.13) * mm});
            skLineSegment(sketch, "E253.0.1", {"start": v(2.23, -34.13) * mm, "end": v(2.23, -26.99) * mm});
            skLineSegment(sketch, "E253.0.2", {"start": v(2.23, -26.99) * mm, "end": v(0, -26.99) * mm});
            skLineSegment(sketch, "E253.0.3", {"start": v(0, -26.99) * mm, "end": v(0, -34.13) * mm});
            skLineSegment(sketch, "E254.0.0", {"start": v(0, -20.64) * mm, "end": v(2.23, -20.64) * mm});
            skLineSegment(sketch, "E254.0.1", {"start": v(2.23, -20.64) * mm, "end": v(2.23, -13.5) * mm});
            skLineSegment(sketch, "E254.0.2", {"start": v(2.23, -13.5) * mm, "end": v(0, -13.5) * mm});
            skLineSegment(sketch, "E254.0.3", {"start": v(0, -13.5) * mm, "end": v(0, -20.64) * mm});
            skLineSegment(sketch, "E255.0.0", {"start": v(0, -7.14) * mm, "end": v(2.23, -7.14) * mm});
            skLineSegment(sketch, "E255.0.1", {"start": v(2.23, -7.14) * mm, "end": v(2.23, 0) * mm});
            skLineSegment(sketch, "E255.0.2", {"start": v(2.23, 0) * mm, "end": v(0, 0) * mm});
            skLineSegment(sketch, "E255.0.3", {"start": v(0, 0) * mm, "end": v(0, -7.14) * mm});
            skSolve(sketch);
        }
        {
            var Q0;
            Q0 = qSketchRegion(id + "F57", true);
            extrude(context, id + "F58", {"entities" : qUnion([Q0]), "operationType" : NewBodyOperationType.REMOVE, "oppositeDirection" : true, "depth" : 25.4 * mm, "offsetDistance" : 25.4 * mm});
        }
        {
            var Q0;
            {var subQ5=sQuery(id+"F56.wireOp",EDGE,"E249.0.2");Q0=makeQuery(id+"F56.imprint","IMPRINT",FACE,{"disambiguationData":[TD([[makeQuery(id+"F56.imprint","IMPRINT",EDGE,{"derivedFrom":subQ5}),1.0]])]});}
            var sketch = newSketch(context, id + "F59", { "sketchPlane" : qUnion([Q0])});
            skLineSegment(sketch, "E256.0.0", {"start": v(73.94, -2.23) * mm, "end": v(73.03, -2.23) * mm});
            skLineSegment(sketch, "E256.0.1", {"start": v(73.03, -2.23) * mm, "end": v(73.03, -25.4) * mm});
            skLineSegment(sketch, "E256.0.2", {"start": v(73.03, -25.4) * mm, "end": v(76.2, -25.4) * mm});
            skLineSegment(sketch, "E256.0.3", {"start": v(76.2, -25.4) * mm, "end": v(76.2, -2.23) * mm});
            skLineSegment(sketch, "E256.0.4", {"start": v(76.2, -2.23) * mm, "end": v(73.94, -2.23) * mm});
            skLineSegment(sketch, "E257.0.0", {"start": v(60.32, -52.9) * mm, "end": v(76.2, -25.4) * mm});
            skLineSegment(sketch, "E257.0.1", {"start": v(76.2, -25.4) * mm, "end": v(73.45, -23.81) * mm});
            skLineSegment(sketch, "E257.0.2", {"start": v(73.45, -23.81) * mm, "end": v(57.58, -51.3) * mm});
            skLineSegment(sketch, "E257.0.3", {"start": v(57.58, -51.3) * mm, "end": v(60.32, -52.9) * mm});
            skLineSegment(sketch, "E258", {"start": v(73.03, -23.81) * mm, "end": v(76.2, -23.81) * mm});
            skSolve(sketch);
        }
        {
            var Q0;
            Q0=makeQuery(id+"F8.opExtrude","SWEPT_FACE",FACE,{"disambiguationData":[OSD([sQuery(id+"F0.wireOp",EDGE,"E2")])]});
            var sketch = newSketch(context, id + "F60", { "sketchPlane" : qUnion([Q0])});
            skLineSegment(sketch, "E259.0.0", {"start": v(2.23, -47.62) * mm, "end": v(2.23, -40.48) * mm});
            skLineSegment(sketch, "E259.0.1", {"start": v(25.4, -40.48) * mm, "end": v(2.23, -40.48) * mm});
            skLineSegment(sketch, "E259.0.2", {"start": v(0, -40.48) * mm, "end": v(0, -47.62) * mm});
            skLineSegment(sketch, "E259.0.3", {"start": v(2.23, -47.63) * mm, "end": v(25.4, -47.63) * mm});
            skLineSegment(sketch, "E260.0.0", {"start": v(0, -34.13) * mm, "end": v(25.4, -34.13) * mm});
            skLineSegment(sketch, "E260.0.1", {"start": v(2.23, -34.13) * mm, "end": v(2.23, -26.99) * mm});
            skLineSegment(sketch, "E260.0.2", {"start": v(25.4, -26.99) * mm, "end": v(0, -26.99) * mm});
            skLineSegment(sketch, "E260.0.3", {"start": v(0, -26.99) * mm, "end": v(0, -34.13) * mm});
            skLineSegment(sketch, "E261.0.0", {"start": v(0, -20.64) * mm, "end": v(25.4, -20.64) * mm});
            skLineSegment(sketch, "E261.0.1", {"start": v(2.23, -20.64) * mm, "end": v(2.23, -13.5) * mm});
            skLineSegment(sketch, "E261.0.2", {"start": v(25.4, -13.5) * mm, "end": v(0, -13.5) * mm});
            skLineSegment(sketch, "E261.0.3", {"start": v(0, -13.5) * mm, "end": v(0, -20.64) * mm});
            skLineSegment(sketch, "E262.0.0", {"start": v(0, -7.14) * mm, "end": v(25.4, -7.14) * mm});
            skLineSegment(sketch, "E262.0.2", {"start": v(25.4, 0) * mm, "end": v(2.23, 0) * mm});
            skLineSegment(sketch, "E262.0.3", {"start": v(0, 0) * mm, "end": v(0, -7.14) * mm});
            skLineSegment(sketch, "E263.0", {"start": v(25.4, -47.62) * mm, "end": v(25.4, 0) * mm});
            skPoint(sketch, "E264.orphan", {"position": v(2.23, -7.14) * mm});
            skPoint(sketch, "E265.0", {"position": v(23.81, -47.62) * mm});
            skLineSegment(sketch, "E266", {"start": v(23.81, -47.62) * mm, "end": v(23.81, 0) * mm});
            skSolve(sketch);
        }
        {
            var Q0;
            {var subQ0=sQuery(id+"F60.wireOp",EDGE,"E263.0");var subQ1=sQuery(id+"F60.wireOp",EDGE,"E261.0.2");var subQ2=makeQuery(id+"F60.imprint","INTERSECT",VERTEX,{"derivedFrom":[subQ1,subQ0]});Q0=makeQuery(id+"F60.imprint","IMPRINT",FACE,{"disambiguationData":[TD([[makeQuery(id+"F60.imprint","IMPRINT",EDGE,{"disambiguationData":[TD([[subQ2,-1.0]])],"derivedFrom":subQ1}),-1.0]])]});}
            var Q1;
            {var subQ0=sQuery(id+"F60.wireOp",EDGE,"E263.0");var subQ1=sQuery(id+"F60.wireOp",EDGE,"E260.0.2");var subQ2=makeQuery(id+"F60.imprint","INTERSECT",VERTEX,{"derivedFrom":[subQ1,subQ0]});Q1=makeQuery(id+"F60.imprint","IMPRINT",FACE,{"disambiguationData":[TD([[makeQuery(id+"F60.imprint","IMPRINT",EDGE,{"disambiguationData":[TD([[subQ2,-1.0]])],"derivedFrom":subQ1}),-1.0]])]});}
            var Q2;
            {var subQ0=sQuery(id+"F60.wireOp",EDGE,"E263.0");var subQ1=sQuery(id+"F60.wireOp",EDGE,"E259.0.1");var subQ2=makeQuery(id+"F60.imprint","INTERSECT",VERTEX,{"derivedFrom":[subQ1,subQ0]});Q2=makeQuery(id+"F60.imprint","IMPRINT",FACE,{"disambiguationData":[TD([[makeQuery(id+"F60.imprint","IMPRINT",EDGE,{"disambiguationData":[TD([[subQ2,-1.0]])],"derivedFrom":subQ1}),-1.0]])]});}
            extrude(context, id + "F61", {"entities" : qUnion([Q0, Q1, Q2]), "operationType" : NewBodyOperationType.REMOVE, "oppositeDirection" : true, "depth" : 25.4 * mm, "offsetDistance" : 25.4 * mm});
        }
        {
            var Q0;
            {var subQ3=sQuery(id+"F38.wireOp",EDGE,"E197.0.0");Q0=makeQuery(id+"F38.imprint","IMPRINT",FACE,{"disambiguationData":[TD([[makeQuery(id+"F38.imprint","IMPRINT",EDGE,{"derivedFrom":subQ3}),-1.0]])]});}
            var sketch = newSketch(context, id + "F62", { "sketchPlane" : qUnion([Q0])});
            skLineSegment(sketch, "E267.0.0", {"start": v(-14.52, -34.13) * mm, "end": v(-14.52, -26.99) * mm});
            skLineSegment(sketch, "E267.0.1", {"start": v(-14.52, -26.99) * mm, "end": v(-16.1, -26.99) * mm});
            skLineSegment(sketch, "E267.0.2", {"start": v(-16.1, -26.99) * mm, "end": v(-16.1, -34.13) * mm});
            skLineSegment(sketch, "E267.0.3", {"start": v(-16.1, -34.13) * mm, "end": v(-14.52, -34.13) * mm});
            skLineSegment(sketch, "E268.0.0", {"start": v(-14.52, -47.62) * mm, "end": v(-14.52, -40.48) * mm});
            skLineSegment(sketch, "E268.0.1", {"start": v(-14.52, -40.48) * mm, "end": v(-16.1, -40.48) * mm});
            skLineSegment(sketch, "E268.0.2", {"start": v(-16.1, -40.48) * mm, "end": v(-16.1, -47.62) * mm});
            skLineSegment(sketch, "E268.0.3", {"start": v(-16.1, -47.63) * mm, "end": v(-14.52, -47.63) * mm});
            skLineSegment(sketch, "E269.0.0", {"start": v(-14.52, -20.64) * mm, "end": v(-14.52, -13.5) * mm});
            skLineSegment(sketch, "E269.0.1", {"start": v(-14.52, -13.5) * mm, "end": v(-16.1, -13.5) * mm});
            skLineSegment(sketch, "E269.0.2", {"start": v(-16.1, -13.5) * mm, "end": v(-16.1, -20.64) * mm});
            skLineSegment(sketch, "E269.0.3", {"start": v(-16.1, -20.64) * mm, "end": v(-14.52, -20.64) * mm});
            skLineSegment(sketch, "E270.0.0", {"start": v(-16.1, -7.14) * mm, "end": v(-14.52, -7.14) * mm});
            skLineSegment(sketch, "E270.0.1", {"start": v(-14.52, -7.14) * mm, "end": v(-14.52, 0) * mm});
            skLineSegment(sketch, "E270.0.2", {"start": v(-14.52, 0) * mm, "end": v(-16.1, 0) * mm});
            skLineSegment(sketch, "E270.0.3", {"start": v(-16.1, 0) * mm, "end": v(-16.1, -7.14) * mm});
            skSolve(sketch);
        }
        {
            var Q0;
            Q0 = qSketchRegion(id + "F62", true);
            extrude(context, id + "F63", {"entities" : qUnion([Q0]), "operationType" : NewBodyOperationType.REMOVE, "oppositeDirection" : true, "depth" : 25.4 * mm, "offsetDistance" : 25.4 * mm});
        }
        {
            var Q0;
            Q0=makeQuery(id+"F9.opExtrude","CAP_FACE",FACE,{"disambiguationData":[OSD([sQuery(id+"F0.wireOp",EDGE,"E3"),sQuery(id+"F2.wireOp",EDGE,"E37"),sQuery(id+"F2.wireOp",EDGE,"E38"),sQuery(id+"F2.wireOp",EDGE,"E39")])],"isStart":false});
            var sketch = newSketch(context, id + "F64", { "sketchPlane" : qUnion([Q0])});
            skLineSegment(sketch, "E271", {"start": v(58.95, -48.93) * mm, "end": v(61.7, -50.52) * mm});
            skLineSegment(sketch, "E272.0", {"start": v(57.58, -51.3) * mm, "end": v(72.66, -25.19) * mm});
            skLineSegment(sketch, "E273.0.0", {"start": v(75.4, -26.77) * mm, "end": v(72.66, -25.19) * mm});
            skLineSegment(sketch, "E273.0.1", {"start": v(72.66, -25.19) * mm, "end": v(57.58, -51.3) * mm});
            skLineSegment(sketch, "E273.0.2", {"start": v(57.58, -51.3) * mm, "end": v(60.32, -52.9) * mm});
            skLineSegment(sketch, "E273.0.3", {"start": v(60.32, -52.9) * mm, "end": v(75.4, -26.77) * mm});
            skLineSegment(sketch, "E274.0.0", {"start": v(60.32, -52.9) * mm, "end": v(60.32, -49.72) * mm});
            skLineSegment(sketch, "E274.0.1", {"start": v(60.32, -49.72) * mm, "end": v(22.23, -49.72) * mm});
            skLineSegment(sketch, "E274.0.2", {"start": v(22.23, -49.72) * mm, "end": v(22.23, -52.9) * mm});
            skLineSegment(sketch, "E274.0.3", {"start": v(22.23, -52.9) * mm, "end": v(60.32, -52.9) * mm});
            skSolve(sketch);
        }
        {
            var Q0;
            {var subQ3=sQuery(id+"F38.wireOp",EDGE,"E197.0.0");Q0=makeQuery(id+"F38.imprint","IMPRINT",FACE,{"disambiguationData":[TD([[makeQuery(id+"F38.imprint","IMPRINT",EDGE,{"derivedFrom":subQ3}),-1.0]])]});}
            var sketch = newSketch(context, id + "F65", { "sketchPlane" : qUnion([Q0])});
            skLineSegment(sketch, "E275.0.0", {"start": v(-12.93, 0) * mm, "end": v(-16.1, 0) * mm});
            skLineSegment(sketch, "E275.0.1", {"start": v(-16.1, 0) * mm, "end": v(-16.1, -47.62) * mm});
            skLineSegment(sketch, "E275.0.2", {"start": v(-16.1, -47.63) * mm, "end": v(15.65, -47.63) * mm});
            skLineSegment(sketch, "E275.0.3", {"start": v(15.65, -47.62) * mm, "end": v(15.65, 0) * mm});
            skLineSegment(sketch, "E275.0.4", {"start": v(15.65, 0) * mm, "end": v(12.47, 0) * mm});
            skLineSegment(sketch, "E275.0.5", {"start": v(12.47, 0) * mm, "end": v(12.47, 3.18) * mm});
            skLineSegment(sketch, "E275.0.6", {"start": v(12.47, 3.18) * mm, "end": v(8.96, 3.18) * mm});
            skLineSegment(sketch, "E275.0.7", {"start": v(8.96, 3.18) * mm, "end": v(8.96, 0) * mm});
            skLineSegment(sketch, "E275.0.8", {"start": v(8.96, 0) * mm, "end": v(1.53, 0) * mm});
            skLineSegment(sketch, "E275.0.9", {"start": v(1.53, 0) * mm, "end": v(1.53, 3.18) * mm});
            skLineSegment(sketch, "E275.0.10", {"start": v(1.53, 3.18) * mm, "end": v(-1.98, 3.18) * mm});
            skLineSegment(sketch, "E275.0.11", {"start": v(-1.98, 3.18) * mm, "end": v(-1.98, 0) * mm});
            skLineSegment(sketch, "E275.0.12", {"start": v(-1.98, 0) * mm, "end": v(-9.42, 0) * mm});
            skLineSegment(sketch, "E275.0.13", {"start": v(-9.42, 0) * mm, "end": v(-9.42, 3.18) * mm});
            skLineSegment(sketch, "E275.0.14", {"start": v(-9.42, 3.18) * mm, "end": v(-12.93, 3.18) * mm});
            skLineSegment(sketch, "E275.0.15", {"start": v(-12.93, 3.18) * mm, "end": v(-12.93, 0) * mm});
            skLineSegment(sketch, "E276.0.0", {"start": v(15.65, -34.13) * mm, "end": v(-15.9, -34.13) * mm});
            skLineSegment(sketch, "E276.0.1", {"start": v(-17.48, -34.13) * mm, "end": v(-17.48, -40.48) * mm});
            skLineSegment(sketch, "E276.0.2", {"start": v(-15.9, -40.48) * mm, "end": v(15.65, -40.48) * mm});
            skLineSegment(sketch, "E276.0.3", {"start": v(-15.9, -40.48) * mm, "end": v(-15.9, -34.13) * mm});
            skLineSegment(sketch, "E277.0.0", {"start": v(15.65, -20.64) * mm, "end": v(-17.48, -20.64) * mm});
            skLineSegment(sketch, "E277.0.1", {"start": v(-17.48, -20.64) * mm, "end": v(-17.48, -26.99) * mm});
            skLineSegment(sketch, "E277.0.2", {"start": v(-17.48, -26.99) * mm, "end": v(15.65, -26.99) * mm});
            skLineSegment(sketch, "E277.0.3", {"start": v(-15.9, -26.99) * mm, "end": v(-15.9, -20.64) * mm});
            skLineSegment(sketch, "E278.0.0", {"start": v(15.65, -7.14) * mm, "end": v(-15.9, -7.14) * mm});
            skLineSegment(sketch, "E278.0.1", {"start": v(-17.48, -7.14) * mm, "end": v(-17.48, -13.5) * mm});
            skLineSegment(sketch, "E278.0.2", {"start": v(-15.9, -13.5) * mm, "end": v(15.65, -13.5) * mm});
            skLineSegment(sketch, "E278.0.3", {"start": v(-15.9, -13.5) * mm, "end": v(-15.9, -7.14) * mm});
            skPoint(sketch, "E279.0", {"position": v(12.9, -47.62) * mm});
            skLineSegment(sketch, "E280", {"start": v(12.9, -47.62) * mm, "end": v(12.9, 0) * mm});
            skPoint(sketch, "E281.orphan", {"position": v(12.9, 14.3) * mm});
            skSolve(sketch);
        }
        {
            var Q0;
            {var subQ0=sQuery(id+"F65.wireOp",EDGE,"E276.0.0");var subQ1=sQuery(id+"F65.wireOp",EDGE,"E275.0.3");var subQ2=makeQuery(id+"F65.imprint","INTERSECT",VERTEX,{"derivedFrom":[subQ1,subQ0]});Q0=makeQuery(id+"F65.imprint","IMPRINT",FACE,{"disambiguationData":[TD([[makeQuery(id+"F65.imprint","IMPRINT",EDGE,{"disambiguationData":[TD([[subQ2,1.0]])],"derivedFrom":subQ1}),1.0]])]});}
            var Q1;
            {var subQ0=sQuery(id+"F65.wireOp",EDGE,"E277.0.0");var subQ1=sQuery(id+"F65.wireOp",EDGE,"E275.0.3");var subQ2=makeQuery(id+"F65.imprint","INTERSECT",VERTEX,{"derivedFrom":[subQ1,subQ0]});Q1=makeQuery(id+"F65.imprint","IMPRINT",FACE,{"disambiguationData":[TD([[makeQuery(id+"F65.imprint","IMPRINT",EDGE,{"disambiguationData":[TD([[subQ2,1.0]])],"derivedFrom":subQ1}),1.0]])]});}
            var Q2;
            {var subQ0=sQuery(id+"F65.wireOp",EDGE,"E278.0.0");var subQ1=sQuery(id+"F65.wireOp",EDGE,"E275.0.3");var subQ2=makeQuery(id+"F65.imprint","INTERSECT",VERTEX,{"derivedFrom":[subQ1,subQ0]});Q2=makeQuery(id+"F65.imprint","IMPRINT",FACE,{"disambiguationData":[TD([[makeQuery(id+"F65.imprint","IMPRINT",EDGE,{"disambiguationData":[TD([[subQ2,1.0]])],"derivedFrom":subQ1}),1.0]])]});}
            extrude(context, id + "F66", {"entities" : qUnion([Q0, Q1, Q2]), "operationType" : NewBodyOperationType.REMOVE, "oppositeDirection" : true, "depth" : 25.4 * mm, "offsetDistance" : 25.4 * mm});
        }
        {
            var Q0;
            Q0=makeQuery(id+"F10.opExtrude","SWEPT_FACE",FACE,{"disambiguationData":[OSD([sQuery(id+"F0.wireOp",EDGE,"E4")])]});
            var sketch = newSketch(context, id + "F67", { "sketchPlane" : qUnion([Q0])});
            skLineSegment(sketch, "E282.0.0", {"start": v(-57.58, -47.62) * mm, "end": v(-57.58, -40.48) * mm});
            skLineSegment(sketch, "E282.0.1", {"start": v(-57.58, -40.48) * mm, "end": v(-60.32, -40.48) * mm});
            skLineSegment(sketch, "E282.0.2", {"start": v(-60.33, -40.48) * mm, "end": v(-60.33, -47.62) * mm});
            skLineSegment(sketch, "E282.0.3", {"start": v(-60.32, -47.63) * mm, "end": v(-57.58, -47.63) * mm});
            skLineSegment(sketch, "E283.0.0", {"start": v(-60.32, -34.13) * mm, "end": v(-57.58, -34.13) * mm});
            skLineSegment(sketch, "E283.0.1", {"start": v(-57.58, -34.13) * mm, "end": v(-57.58, -26.99) * mm});
            skLineSegment(sketch, "E283.0.2", {"start": v(-57.58, -26.99) * mm, "end": v(-60.32, -26.99) * mm});
            skLineSegment(sketch, "E283.0.3", {"start": v(-60.33, -26.99) * mm, "end": v(-60.33, -34.13) * mm});
            skLineSegment(sketch, "E284.0.0", {"start": v(-60.32, -20.64) * mm, "end": v(-57.58, -20.64) * mm});
            skLineSegment(sketch, "E284.0.1", {"start": v(-57.58, -20.64) * mm, "end": v(-57.58, -13.5) * mm});
            skLineSegment(sketch, "E284.0.2", {"start": v(-57.58, -13.5) * mm, "end": v(-60.32, -13.5) * mm});
            skLineSegment(sketch, "E284.0.3", {"start": v(-60.33, -13.5) * mm, "end": v(-60.33, -20.64) * mm});
            skLineSegment(sketch, "E285.0.0", {"start": v(-60.32, -7.14) * mm, "end": v(-57.58, -7.14) * mm});
            skLineSegment(sketch, "E285.0.1", {"start": v(-57.58, -7.14) * mm, "end": v(-57.58, 0) * mm});
            skLineSegment(sketch, "E285.0.2", {"start": v(-57.58, 0) * mm, "end": v(-60.32, 0) * mm});
            skLineSegment(sketch, "E285.0.3", {"start": v(-60.33, 0) * mm, "end": v(-60.33, -7.14) * mm});
            skSolve(sketch);
        }
        {
            var Q0;
            Q0 = qSketchRegion(id + "F67", true);
            extrude(context, id + "F68", {"entities" : qUnion([Q0]), "operationType" : NewBodyOperationType.REMOVE, "oppositeDirection" : true, "depth" : 25.4 * mm, "offsetDistance" : 25.4 * mm});
        }
        {
            var Q0;
            {var subQ4=sQuery(id+"F64.wireOp",EDGE,"E273.0.2");Q0=makeQuery(id+"F64.imprint","IMPRINT",FACE,{"disambiguationData":[TD([[makeQuery(id+"F64.imprint","IMPRINT",EDGE,{"derivedFrom":subQ4}),1.0]])]});}
            var sketch = newSketch(context, id + "F69", { "sketchPlane" : qUnion([Q0])});
            skLineSegment(sketch, "E286.0.0", {"start": v(22.23, -52.9) * mm, "end": v(23.76, -50.12) * mm});
            skLineSegment(sketch, "E286.0.1", {"start": v(23.76, -50.12) * mm, "end": v(0, -36.97) * mm});
            skLineSegment(sketch, "E286.0.2", {"start": v(0, -36.97) * mm, "end": v(-1.54, -39.75) * mm});
            skLineSegment(sketch, "E286.0.3", {"start": v(-1.54, -39.75) * mm, "end": v(22.23, -52.9) * mm});
            skLineSegment(sketch, "E287.0.0", {"start": v(22.23, -49.72) * mm, "end": v(22.23, -52.9) * mm});
            skLineSegment(sketch, "E287.0.1", {"start": v(22.23, -52.9) * mm, "end": v(60.32, -52.9) * mm});
            skLineSegment(sketch, "E287.0.2", {"start": v(60.32, -52.9) * mm, "end": v(57.58, -51.3) * mm});
            skLineSegment(sketch, "E287.0.3", {"start": v(57.58, -51.3) * mm, "end": v(58.5, -49.72) * mm});
            skLineSegment(sketch, "E287.0.4", {"start": v(58.5, -49.72) * mm, "end": v(22.23, -49.72) * mm});
            skLineSegment(sketch, "E288", {"start": v(23.76, -49.72) * mm, "end": v(23.76, -52.9) * mm});
            skSolve(sketch);
        }
        {
            var Q0;
            Q0=makeQuery(id+"F10.opExtrude","SWEPT_FACE",FACE,{"disambiguationData":[OSD([sQuery(id+"F0.wireOp",EDGE,"E4")])]});
            var sketch = newSketch(context, id + "F70", { "sketchPlane" : qUnion([Q0])});
            skLineSegment(sketch, "E289.0.0", {"start": v(-57.58, -40.48) * mm, "end": v(-57.58, -47.62) * mm});
            skLineSegment(sketch, "E289.0.1", {"start": v(-57.58, -47.63) * mm, "end": v(-22.23, -47.63) * mm});
            skLineSegment(sketch, "E289.0.2", {"start": v(-22.23, -47.62) * mm, "end": v(-22.23, 0) * mm});
            skLineSegment(sketch, "E289.0.3", {"start": v(-22.23, 0) * mm, "end": v(-25.4, 0) * mm});
            skLineSegment(sketch, "E289.0.4", {"start": v(-25.4, 0) * mm, "end": v(-25.4, 3.18) * mm});
            skLineSegment(sketch, "E289.0.5", {"start": v(-25.4, 3.18) * mm, "end": v(-31.75, 3.18) * mm});
            skLineSegment(sketch, "E289.0.6", {"start": v(-31.75, 3.18) * mm, "end": v(-31.75, 0) * mm});
            skLineSegment(sketch, "E289.0.7", {"start": v(-31.75, 0) * mm, "end": v(-38.1, 0) * mm});
            skLineSegment(sketch, "E289.0.8", {"start": v(-38.1, 0) * mm, "end": v(-38.1, 3.18) * mm});
            skLineSegment(sketch, "E289.0.9", {"start": v(-38.1, 3.18) * mm, "end": v(-44.45, 3.18) * mm});
            skLineSegment(sketch, "E289.0.10", {"start": v(-44.45, 3.18) * mm, "end": v(-44.45, 0) * mm});
            skLineSegment(sketch, "E289.0.11", {"start": v(-44.45, 0) * mm, "end": v(-50.8, 0) * mm});
            skLineSegment(sketch, "E289.0.12", {"start": v(-50.8, 0) * mm, "end": v(-50.8, 3.18) * mm});
            skLineSegment(sketch, "E289.0.13", {"start": v(-50.8, 3.18) * mm, "end": v(-57.15, 3.18) * mm});
            skLineSegment(sketch, "E289.0.14", {"start": v(-57.15, 3.18) * mm, "end": v(-57.15, 0) * mm});
            skLineSegment(sketch, "E289.0.15", {"start": v(-57.15, 0) * mm, "end": v(-57.58, 0) * mm});
            skLineSegment(sketch, "E289.0.16", {"start": v(-57.58, 0) * mm, "end": v(-57.58, -7.14) * mm});
            skLineSegment(sketch, "E289.0.17", {"start": v(-22.23, -7.14) * mm, "end": v(-57.58, -7.14) * mm});
            skLineSegment(sketch, "E289.0.18", {"start": v(-60.33, -7.14) * mm, "end": v(-60.33, -13.5) * mm});
            skLineSegment(sketch, "E289.0.19", {"start": v(-60.32, -13.5) * mm, "end": v(-22.23, -13.5) * mm});
            skLineSegment(sketch, "E289.0.20", {"start": v(-57.58, -13.5) * mm, "end": v(-57.58, -20.64) * mm});
            skLineSegment(sketch, "E289.0.21", {"start": v(-22.23, -20.64) * mm, "end": v(-57.58, -20.64) * mm});
            skLineSegment(sketch, "E289.0.22", {"start": v(-60.33, -20.64) * mm, "end": v(-60.33, -26.99) * mm});
            skLineSegment(sketch, "E289.0.23", {"start": v(-57.58, -26.99) * mm, "end": v(-22.23, -26.99) * mm});
            skLineSegment(sketch, "E289.0.24", {"start": v(-57.58, -26.99) * mm, "end": v(-57.58, -34.13) * mm});
            skLineSegment(sketch, "E289.0.25", {"start": v(-22.23, -34.13) * mm, "end": v(-57.58, -34.13) * mm});
            skLineSegment(sketch, "E289.0.26", {"start": v(-60.33, -34.13) * mm, "end": v(-60.33, -40.48) * mm});
            skLineSegment(sketch, "E289.0.27", {"start": v(-60.32, -40.48) * mm, "end": v(-22.23, -40.48) * mm});
            skPoint(sketch, "E290.0", {"position": v(-23.76, -47.62) * mm});
            skLineSegment(sketch, "E291", {"start": v(-23.76, -47.62) * mm, "end": v(-23.76, 0) * mm});
            skSolve(sketch);
        }
        {
            var Q0;
            {var subQ0=sQuery(id+"F70.wireOp",EDGE,"E289.0.25");var subQ1=sQuery(id+"F70.wireOp",EDGE,"E289.0.2");var subQ2=makeQuery(id+"F70.imprint","INTERSECT",VERTEX,{"derivedFrom":[subQ1,subQ0]});Q0=makeQuery(id+"F70.imprint","IMPRINT",FACE,{"disambiguationData":[TD([[makeQuery(id+"F70.imprint","IMPRINT",EDGE,{"disambiguationData":[TD([[subQ2,1.0]])],"derivedFrom":subQ1}),1.0]])]});}
            var Q1;
            {var subQ0=sQuery(id+"F70.wireOp",EDGE,"E289.0.21");var subQ1=sQuery(id+"F70.wireOp",EDGE,"E289.0.2");var subQ2=makeQuery(id+"F70.imprint","INTERSECT",VERTEX,{"derivedFrom":[subQ1,subQ0]});Q1=makeQuery(id+"F70.imprint","IMPRINT",FACE,{"disambiguationData":[TD([[makeQuery(id+"F70.imprint","IMPRINT",EDGE,{"disambiguationData":[TD([[subQ2,1.0]])],"derivedFrom":subQ1}),1.0]])]});}
            var Q2;
            {var subQ0=sQuery(id+"F70.wireOp",EDGE,"E289.0.17");var subQ1=sQuery(id+"F70.wireOp",EDGE,"E289.0.2");var subQ2=makeQuery(id+"F70.imprint","INTERSECT",VERTEX,{"derivedFrom":[subQ1,subQ0]});Q2=makeQuery(id+"F70.imprint","IMPRINT",FACE,{"disambiguationData":[TD([[makeQuery(id+"F70.imprint","IMPRINT",EDGE,{"disambiguationData":[TD([[subQ2,1.0]])],"derivedFrom":subQ1}),1.0]])]});}
            extrude(context, id + "F71", {"entities" : qUnion([Q0, Q1, Q2]), "operationType" : NewBodyOperationType.REMOVE, "oppositeDirection" : true, "depth" : 25.4 * mm, "offsetDistance" : 25.4 * mm});
        }
        {
            var Q0;
            Q0=makeQuery(id+"F11.opExtrude","SWEPT_FACE",FACE,{"disambiguationData":[OSD([sQuery(id+"F0.wireOp",EDGE,"E5"),sQuery(id+"F2.wireOp",EDGE,"E45")])]});
            var sketch = newSketch(context, id + "F72", { "sketchPlane" : qUnion([Q0])});
            skLineSegment(sketch, "E292.0.0", {"start": v(-45.06, -7.14) * mm, "end": v(-43.52, -7.14) * mm});
            skLineSegment(sketch, "E292.0.1", {"start": v(-43.52, -7.14) * mm, "end": v(-43.52, 0) * mm});
            skLineSegment(sketch, "E292.0.2", {"start": v(-43.52, 0) * mm, "end": v(-45.06, 0) * mm});
            skLineSegment(sketch, "E292.0.3", {"start": v(-45.06, 0) * mm, "end": v(-45.06, -7.14) * mm});
            skLineSegment(sketch, "E292.1.0", {"start": v(-45.06, -20.64) * mm, "end": v(-43.52, -20.64) * mm});
            skLineSegment(sketch, "E292.1.1", {"start": v(-43.52, -20.64) * mm, "end": v(-43.52, -13.5) * mm});
            skLineSegment(sketch, "E292.1.2", {"start": v(-43.52, -13.5) * mm, "end": v(-45.06, -13.5) * mm});
            skLineSegment(sketch, "E292.1.3", {"start": v(-45.06, -13.5) * mm, "end": v(-45.06, -20.64) * mm});
            skLineSegment(sketch, "E292.2.0", {"start": v(-45.06, -34.13) * mm, "end": v(-43.52, -34.13) * mm});
            skLineSegment(sketch, "E292.2.1", {"start": v(-43.52, -34.13) * mm, "end": v(-43.52, -26.99) * mm});
            skLineSegment(sketch, "E292.2.2", {"start": v(-43.52, -26.99) * mm, "end": v(-45.06, -26.99) * mm});
            skLineSegment(sketch, "E292.2.3", {"start": v(-45.06, -26.99) * mm, "end": v(-45.06, -34.13) * mm});
            skLineSegment(sketch, "E292.3.0", {"start": v(-43.52, -47.62) * mm, "end": v(-43.52, -40.48) * mm});
            skLineSegment(sketch, "E292.3.1", {"start": v(-43.52, -40.48) * mm, "end": v(-45.06, -40.48) * mm});
            skLineSegment(sketch, "E292.3.2", {"start": v(-45.06, -40.48) * mm, "end": v(-45.06, -47.62) * mm});
            skLineSegment(sketch, "E292.3.3", {"start": v(-45.06, -47.63) * mm, "end": v(-43.52, -47.63) * mm});
            skSolve(sketch);
        }
        {
            var Q0;
            Q0 = qSketchRegion(id + "F72", true);
            extrude(context, id + "F73", {"entities" : qUnion([Q0]), "operationType" : NewBodyOperationType.REMOVE, "oppositeDirection" : true, "depth" : 25.4 * mm, "offsetDistance" : 25.4 * mm});
        }
        {
            var Q0;
            {var subQ1=sQuery(id+"F69.wireOp",EDGE,"E286.0.2");Q0=makeQuery(id+"F69.imprint","IMPRINT",FACE,{"disambiguationData":[TD([[makeQuery(id+"F69.imprint","IMPRINT",EDGE,{"derivedFrom":subQ1}),1.0]])]});}
            var sketch = newSketch(context, id + "F74", { "sketchPlane" : qUnion([Q0])});
            skLineSegment(sketch, "E293.0", {"start": v(-23.76, -50.12) * mm, "end": v(0, -36.97) * mm});
            skLineSegment(sketch, "E294.0.0", {"start": v(0, -36.97) * mm, "end": v(-1.54, -39.75) * mm});
            skLineSegment(sketch, "E294.0.1", {"start": v(-1.54, -39.75) * mm, "end": v(22.23, -52.9) * mm});
            skLineSegment(sketch, "E294.0.2", {"start": v(22.23, -52.9) * mm, "end": v(22.23, -49.72) * mm});
            skLineSegment(sketch, "E294.0.3", {"start": v(22.23, -49.72) * mm, "end": v(23.04, -49.72) * mm});
            skLineSegment(sketch, "E294.0.4", {"start": v(23.04, -49.72) * mm, "end": v(0, -36.97) * mm});
            skLineSegment(sketch, "E294.1.0", {"start": v(-22.23, -52.9) * mm, "end": v(1.54, -39.75) * mm});
            skLineSegment(sketch, "E294.1.1", {"start": v(1.54, -39.75) * mm, "end": v(0, -36.97) * mm});
            skLineSegment(sketch, "E294.1.2", {"start": v(0, -36.97) * mm, "end": v(-23.76, -50.12) * mm});
            skLineSegment(sketch, "E294.1.3", {"start": v(-23.76, -50.12) * mm, "end": v(-22.23, -52.9) * mm});
            skLineSegment(sketch, "E295", {"start": v(2.35, -38.27) * mm, "end": v(0.82, -41.05) * mm});
            skSolve(sketch);
        }
        {
            var Q0;
            Q0=makeQuery(id+"F11.opExtrude","SWEPT_FACE",FACE,{"disambiguationData":[OSD([sQuery(id+"F0.wireOp",EDGE,"E5"),sQuery(id+"F2.wireOp",EDGE,"E45")])]});
            var sketch = newSketch(context, id + "F75", { "sketchPlane" : qUnion([Q0])});
            skLineSegment(sketch, "E296.0.0", {"start": v(-17.9, -7.14) * mm, "end": v(-43.52, -7.14) * mm});
            skLineSegment(sketch, "E296.0.1", {"start": v(-45.06, -7.14) * mm, "end": v(-45.06, -13.5) * mm});
            skLineSegment(sketch, "E296.0.2", {"start": v(-43.52, -13.5) * mm, "end": v(-17.9, -13.5) * mm});
            skLineSegment(sketch, "E296.0.3", {"start": v(-43.52, -13.5) * mm, "end": v(-43.52, -20.64) * mm});
            skLineSegment(sketch, "E296.0.4", {"start": v(-17.9, -20.64) * mm, "end": v(-43.52, -20.64) * mm});
            skLineSegment(sketch, "E296.0.5", {"start": v(-45.06, -20.64) * mm, "end": v(-45.06, -26.99) * mm});
            skLineSegment(sketch, "E296.0.6", {"start": v(-45.06, -26.99) * mm, "end": v(-17.9, -26.99) * mm});
            skLineSegment(sketch, "E296.0.7", {"start": v(-43.52, -26.99) * mm, "end": v(-43.52, -34.13) * mm});
            skLineSegment(sketch, "E296.0.8", {"start": v(-17.9, -34.13) * mm, "end": v(-45.06, -34.13) * mm});
            skLineSegment(sketch, "E296.0.9", {"start": v(-45.06, -34.13) * mm, "end": v(-45.06, -40.48) * mm});
            skLineSegment(sketch, "E296.0.10", {"start": v(-43.52, -40.48) * mm, "end": v(-17.9, -40.48) * mm});
            skLineSegment(sketch, "E296.0.11", {"start": v(-43.52, -40.48) * mm, "end": v(-43.52, -47.62) * mm});
            skLineSegment(sketch, "E296.0.12", {"start": v(-43.52, -47.63) * mm, "end": v(-17.9, -47.63) * mm});
            skLineSegment(sketch, "E296.0.13", {"start": v(-17.9, -47.62) * mm, "end": v(-17.9, 3.17) * mm});
            skLineSegment(sketch, "E296.0.14", {"start": v(-17.9, 3.18) * mm, "end": v(-19.66, 3.18) * mm});
            skLineSegment(sketch, "E296.0.15", {"start": v(-19.66, 3.18) * mm, "end": v(-19.66, 0) * mm});
            skLineSegment(sketch, "E296.0.16", {"start": v(-19.66, 0) * mm, "end": v(-22.83, 0) * mm});
            skLineSegment(sketch, "E296.0.17", {"start": v(-22.83, 0) * mm, "end": v(-22.83, 3.18) * mm});
            skLineSegment(sketch, "E296.0.18", {"start": v(-22.83, 3.18) * mm, "end": v(-26, 3.18) * mm});
            skLineSegment(sketch, "E296.0.19", {"start": v(-26, 3.18) * mm, "end": v(-26, 0) * mm});
            skLineSegment(sketch, "E296.0.20", {"start": v(-26, 0) * mm, "end": v(-30.77, 0) * mm});
            skLineSegment(sketch, "E296.0.21", {"start": v(-30.77, 0) * mm, "end": v(-30.77, 3.18) * mm});
            skLineSegment(sketch, "E296.0.22", {"start": v(-30.77, 3.18) * mm, "end": v(-33.94, 3.18) * mm});
            skLineSegment(sketch, "E296.0.23", {"start": v(-33.94, 3.18) * mm, "end": v(-33.94, 0) * mm});
            skLineSegment(sketch, "E296.0.24", {"start": v(-33.94, 0) * mm, "end": v(-38.7, 0) * mm});
            skLineSegment(sketch, "E296.0.25", {"start": v(-38.7, 0) * mm, "end": v(-38.7, 3.18) * mm});
            skLineSegment(sketch, "E296.0.26", {"start": v(-38.7, 3.18) * mm, "end": v(-41.88, 3.18) * mm});
            skLineSegment(sketch, "E296.0.27", {"start": v(-41.88, 3.18) * mm, "end": v(-41.88, 0) * mm});
            skLineSegment(sketch, "E296.0.28", {"start": v(-41.88, 0) * mm, "end": v(-43.52, 0) * mm});
            skLineSegment(sketch, "E296.0.29", {"start": v(-43.52, 0) * mm, "end": v(-43.52, -7.14) * mm});
            skPoint(sketch, "E297.0", {"position": v(-20.59, -47.62) * mm});
            skLineSegment(sketch, "E298", {"start": v(-20.59, -47.62) * mm, "end": v(-20.59, 0) * mm});
            skSolve(sketch);
        }
        {
            var Q0;
            {var subQ0=sQuery(id+"F75.wireOp",EDGE,"E296.0.13");var subQ1=sQuery(id+"F75.wireOp",EDGE,"E296.0.8");var subQ2=makeQuery(id+"F75.imprint","INTERSECT",VERTEX,{"derivedFrom":[subQ1,subQ0]});Q0=makeQuery(id+"F75.imprint","IMPRINT",FACE,{"disambiguationData":[TD([[makeQuery(id+"F75.imprint","IMPRINT",EDGE,{"disambiguationData":[TD([[subQ2,-1.0]])],"derivedFrom":subQ1}),1.0]])]});}
            var Q1;
            {var subQ0=sQuery(id+"F75.wireOp",EDGE,"E296.0.13");var subQ1=sQuery(id+"F75.wireOp",EDGE,"E296.0.4");var subQ2=makeQuery(id+"F75.imprint","INTERSECT",VERTEX,{"derivedFrom":[subQ1,subQ0]});Q1=makeQuery(id+"F75.imprint","IMPRINT",FACE,{"disambiguationData":[TD([[makeQuery(id+"F75.imprint","IMPRINT",EDGE,{"disambiguationData":[TD([[subQ2,-1.0]])],"derivedFrom":subQ1}),1.0]])]});}
            var Q2;
            {var subQ0=sQuery(id+"F75.wireOp",EDGE,"E296.0.13");var subQ1=sQuery(id+"F75.wireOp",EDGE,"E296.0.0");var subQ2=makeQuery(id+"F75.imprint","INTERSECT",VERTEX,{"derivedFrom":[subQ1,subQ0]});Q2=makeQuery(id+"F75.imprint","IMPRINT",FACE,{"disambiguationData":[TD([[makeQuery(id+"F75.imprint","IMPRINT",EDGE,{"disambiguationData":[TD([[subQ2,-1.0]])],"derivedFrom":subQ1}),1.0]])]});}
            extrude(context, id + "F76", {"entities" : qUnion([Q0, Q1, Q2]), "operationType" : NewBodyOperationType.REMOVE, "oppositeDirection" : true, "depth" : 25.4 * mm, "offsetDistance" : 25.4 * mm});
        }
        {
            var Q0;
            Q0=makeQuery(id+"F12.opExtrude","SWEPT_FACE",FACE,{"disambiguationData":[OSD([sQuery(id+"F0.wireOp",EDGE,"E6"),sQuery(id+"F2.wireOp",EDGE,"E40")])]});
            var sketch = newSketch(context, id + "F77", { "sketchPlane" : qUnion([Q0])});
            skLineSegment(sketch, "E299.0.0", {"start": v(20.59, -7.14) * mm, "end": v(17.9, -7.14) * mm});
            skLineSegment(sketch, "E299.0.1", {"start": v(17.9, -7.14) * mm, "end": v(17.9, 3.17) * mm});
            skLineSegment(sketch, "E299.0.2", {"start": v(17.9, 3.18) * mm, "end": v(20.59, 3.18) * mm});
            skLineSegment(sketch, "E299.0.3", {"start": v(20.59, 3.17) * mm, "end": v(20.59, -7.14) * mm});
            skLineSegment(sketch, "E299.1.0", {"start": v(20.59, -20.64) * mm, "end": v(17.9, -20.64) * mm});
            skLineSegment(sketch, "E299.1.1", {"start": v(17.9, -20.64) * mm, "end": v(17.9, -13.5) * mm});
            skLineSegment(sketch, "E299.1.2", {"start": v(17.9, -13.5) * mm, "end": v(20.59, -13.5) * mm});
            skLineSegment(sketch, "E299.1.3", {"start": v(20.59, -13.5) * mm, "end": v(20.59, -20.64) * mm});
            skLineSegment(sketch, "E299.2.0", {"start": v(20.59, -34.13) * mm, "end": v(17.9, -34.13) * mm});
            skLineSegment(sketch, "E299.2.1", {"start": v(17.9, -34.13) * mm, "end": v(17.9, -26.99) * mm});
            skLineSegment(sketch, "E299.2.2", {"start": v(17.9, -26.99) * mm, "end": v(20.59, -26.99) * mm});
            skLineSegment(sketch, "E299.2.3", {"start": v(20.59, -26.99) * mm, "end": v(20.59, -34.13) * mm});
            skLineSegment(sketch, "E299.3.0", {"start": v(17.9, -47.62) * mm, "end": v(17.9, -40.48) * mm});
            skLineSegment(sketch, "E299.3.1", {"start": v(17.9, -40.48) * mm, "end": v(20.59, -40.48) * mm});
            skLineSegment(sketch, "E299.3.2", {"start": v(20.59, -40.48) * mm, "end": v(20.59, -47.62) * mm});
            skLineSegment(sketch, "E299.3.3", {"start": v(20.59, -47.63) * mm, "end": v(17.9, -47.63) * mm});
            skSolve(sketch);
        }
        {
            var Q0;
            Q0 = qSketchRegion(id + "F77", true);
            extrude(context, id + "F78", {"entities" : qUnion([Q0]), "operationType" : NewBodyOperationType.REMOVE, "oppositeDirection" : true, "depth" : 25.4 * mm, "offsetDistance" : 25.4 * mm});
        }
        {
            var Q0;
            {var subQ4=sQuery(id+"F74.wireOp",EDGE,"E294.0.0");Q0=makeQuery(id+"F74.imprint","IMPRINT",FACE,{"disambiguationData":[TD([[makeQuery(id+"F74.imprint","IMPRINT",EDGE,{"derivedFrom":subQ4}),-1.0]])]});}
            var sketch = newSketch(context, id + "F79", { "sketchPlane" : qUnion([Q0])});
            skLineSegment(sketch, "E300.0.0", {"start": v(-1.54, -39.75) * mm, "end": v(0, -36.97) * mm});
            skLineSegment(sketch, "E300.0.1", {"start": v(0, -36.97) * mm, "end": v(-23.76, -50.12) * mm});
            skLineSegment(sketch, "E300.0.2", {"start": v(-23.76, -50.12) * mm, "end": v(-22.23, -52.9) * mm});
            skLineSegment(sketch, "E300.0.3", {"start": v(-22.23, -52.9) * mm, "end": v(0, -40.6) * mm});
            skLineSegment(sketch, "E300.0.4", {"start": v(0, -40.6) * mm, "end": v(-1.54, -39.75) * mm});
            skLineSegment(sketch, "E301.0.0", {"start": v(-22.23, -49.72) * mm, "end": v(-60.33, -49.72) * mm});
            skLineSegment(sketch, "E301.0.1", {"start": v(-60.33, -49.72) * mm, "end": v(-60.33, -52.9) * mm});
            skLineSegment(sketch, "E301.0.2", {"start": v(-60.33, -52.9) * mm, "end": v(-22.23, -52.9) * mm});
            skLineSegment(sketch, "E301.0.3", {"start": v(-22.23, -52.9) * mm, "end": v(-22.23, -49.72) * mm});
            skLineSegment(sketch, "E302", {"start": v(-22.42, -49.37) * mm, "end": v(-20.88, -52.15) * mm});
            skPoint(sketch, "E302.endSnap0", {"position": v(-22.23, -51.3) * mm});
            skSolve(sketch);
        }
        {
            var Q0;
            Q0=makeQuery(id+"F12.opExtrude","SWEPT_FACE",FACE,{"disambiguationData":[OSD([sQuery(id+"F0.wireOp",EDGE,"E6"),sQuery(id+"F2.wireOp",EDGE,"E40")])]});
            var sketch = newSketch(context, id + "F80", { "sketchPlane" : qUnion([Q0])});
            skLineSegment(sketch, "E303.0.0", {"start": v(20.59, 0) * mm, "end": v(20.59, -7.14) * mm});
            skLineSegment(sketch, "E303.0.1", {"start": v(45.06, -7.14) * mm, "end": v(17.9, -7.14) * mm});
            skLineSegment(sketch, "E303.0.2", {"start": v(17.9, -7.14) * mm, "end": v(17.9, -13.5) * mm});
            skLineSegment(sketch, "E303.0.3", {"start": v(17.9, -13.5) * mm, "end": v(45.06, -13.5) * mm});
            skLineSegment(sketch, "E303.0.4", {"start": v(20.59, -13.5) * mm, "end": v(20.59, -20.64) * mm});
            skLineSegment(sketch, "E303.0.5", {"start": v(45.06, -20.64) * mm, "end": v(17.9, -20.64) * mm});
            skLineSegment(sketch, "E303.0.6", {"start": v(17.9, -20.64) * mm, "end": v(17.9, -26.99) * mm});
            skLineSegment(sketch, "E303.0.7", {"start": v(17.9, -26.99) * mm, "end": v(45.06, -26.99) * mm});
            skLineSegment(sketch, "E303.0.8", {"start": v(20.59, -26.99) * mm, "end": v(20.59, -34.13) * mm});
            skLineSegment(sketch, "E303.0.9", {"start": v(45.06, -34.13) * mm, "end": v(17.9, -34.13) * mm});
            skLineSegment(sketch, "E303.0.10", {"start": v(17.9, -34.13) * mm, "end": v(17.9, -40.48) * mm});
            skLineSegment(sketch, "E303.0.11", {"start": v(17.9, -40.48) * mm, "end": v(45.06, -40.48) * mm});
            skLineSegment(sketch, "E303.0.12", {"start": v(20.59, -40.48) * mm, "end": v(20.59, -47.62) * mm});
            skLineSegment(sketch, "E303.0.13", {"start": v(20.59, -47.63) * mm, "end": v(45.06, -47.63) * mm});
            skLineSegment(sketch, "E303.0.14", {"start": v(45.06, -47.62) * mm, "end": v(45.06, 0) * mm});
            skLineSegment(sketch, "E303.0.15", {"start": v(45.06, 0) * mm, "end": v(41.88, 0) * mm});
            skLineSegment(sketch, "E303.0.16", {"start": v(41.88, 0) * mm, "end": v(41.88, 3.18) * mm});
            skLineSegment(sketch, "E303.0.17", {"start": v(41.88, 3.18) * mm, "end": v(38.7, 3.18) * mm});
            skLineSegment(sketch, "E303.0.18", {"start": v(38.7, 3.18) * mm, "end": v(38.7, 0) * mm});
            skLineSegment(sketch, "E303.0.19", {"start": v(38.7, 0) * mm, "end": v(33.94, 0) * mm});
            skLineSegment(sketch, "E303.0.20", {"start": v(33.94, 0) * mm, "end": v(33.94, 3.18) * mm});
            skLineSegment(sketch, "E303.0.21", {"start": v(33.94, 3.18) * mm, "end": v(30.77, 3.18) * mm});
            skLineSegment(sketch, "E303.0.22", {"start": v(30.77, 3.18) * mm, "end": v(30.77, 0) * mm});
            skLineSegment(sketch, "E303.0.23", {"start": v(30.77, 0) * mm, "end": v(26, 0) * mm});
            skLineSegment(sketch, "E303.0.24", {"start": v(26, 0) * mm, "end": v(26, 3.18) * mm});
            skLineSegment(sketch, "E303.0.25", {"start": v(26, 3.18) * mm, "end": v(22.83, 3.18) * mm});
            skLineSegment(sketch, "E303.0.26", {"start": v(22.83, 3.18) * mm, "end": v(22.83, 0) * mm});
            skLineSegment(sketch, "E303.0.27", {"start": v(22.83, 0) * mm, "end": v(20.59, 0) * mm});
            skPoint(sketch, "E304.0", {"position": v(43.52, -47.62) * mm});
            skLineSegment(sketch, "E305", {"start": v(43.52, -47.62) * mm, "end": v(43.52, 0) * mm});
            skSolve(sketch);
        }
        {
            var Q0;
            {var subQ0=sQuery(id+"F80.wireOp",EDGE,"E303.0.14");var subQ1=sQuery(id+"F80.wireOp",EDGE,"E303.0.1");var subQ2=makeQuery(id+"F80.imprint","INTERSECT",VERTEX,{"derivedFrom":[subQ1,subQ0]});Q0=makeQuery(id+"F80.imprint","IMPRINT",FACE,{"disambiguationData":[TD([[makeQuery(id+"F80.imprint","IMPRINT",EDGE,{"disambiguationData":[TD([[subQ2,-1.0]])],"derivedFrom":subQ1}),1.0]])]});}
            var Q1;
            {var subQ0=sQuery(id+"F80.wireOp",EDGE,"E303.0.14");var subQ1=sQuery(id+"F80.wireOp",EDGE,"E303.0.5");var subQ2=makeQuery(id+"F80.imprint","INTERSECT",VERTEX,{"derivedFrom":[subQ1,subQ0]});Q1=makeQuery(id+"F80.imprint","IMPRINT",FACE,{"disambiguationData":[TD([[makeQuery(id+"F80.imprint","IMPRINT",EDGE,{"disambiguationData":[TD([[subQ2,-1.0]])],"derivedFrom":subQ1}),1.0]])]});}
            var Q2;
            {var subQ0=sQuery(id+"F80.wireOp",EDGE,"E303.0.14");var subQ1=sQuery(id+"F80.wireOp",EDGE,"E303.0.9");var subQ2=makeQuery(id+"F80.imprint","INTERSECT",VERTEX,{"derivedFrom":[subQ1,subQ0]});Q2=makeQuery(id+"F80.imprint","IMPRINT",FACE,{"disambiguationData":[TD([[makeQuery(id+"F80.imprint","IMPRINT",EDGE,{"disambiguationData":[TD([[subQ2,-1.0]])],"derivedFrom":subQ1}),1.0]])]});}
            extrude(context, id + "F81", {"entities" : qUnion([Q0, Q1, Q2]), "operationType" : NewBodyOperationType.REMOVE, "oppositeDirection" : true, "depth" : 25.4 * mm, "offsetDistance" : 25.4 * mm});
        }
        {
            var Q0;
            Q0=makeQuery(id+"F3.opExtrude","SWEPT_FACE",FACE,{"disambiguationData":[OSD([sQuery(id+"F0.wireOp",EDGE,"E7")])]});
            var sketch = newSketch(context, id + "F82", { "sketchPlane" : qUnion([Q0])});
            skLineSegment(sketch, "E306.0.0", {"start": v(23.76, -47.62) * mm, "end": v(23.76, -40.48) * mm});
            skLineSegment(sketch, "E306.0.1", {"start": v(23.76, -40.48) * mm, "end": v(22.23, -40.48) * mm});
            skLineSegment(sketch, "E306.0.2", {"start": v(22.23, -40.48) * mm, "end": v(22.23, -47.62) * mm});
            skLineSegment(sketch, "E306.0.3", {"start": v(22.23, -47.63) * mm, "end": v(23.76, -47.63) * mm});
            skLineSegment(sketch, "E307.0.0", {"start": v(23.76, -34.13) * mm, "end": v(23.76, -26.99) * mm});
            skLineSegment(sketch, "E307.0.1", {"start": v(23.76, -26.99) * mm, "end": v(22.23, -26.99) * mm});
            skLineSegment(sketch, "E307.0.2", {"start": v(22.23, -26.99) * mm, "end": v(22.23, -34.13) * mm});
            skLineSegment(sketch, "E307.0.3", {"start": v(22.23, -34.13) * mm, "end": v(23.76, -34.13) * mm});
            skLineSegment(sketch, "E308.0.0", {"start": v(23.76, -20.64) * mm, "end": v(23.76, -13.5) * mm});
            skLineSegment(sketch, "E308.0.1", {"start": v(23.76, -13.5) * mm, "end": v(22.23, -13.5) * mm});
            skLineSegment(sketch, "E308.0.2", {"start": v(22.23, -13.5) * mm, "end": v(22.23, -20.64) * mm});
            skLineSegment(sketch, "E308.0.3", {"start": v(22.23, -20.64) * mm, "end": v(23.76, -20.64) * mm});
            skLineSegment(sketch, "E309.0.0", {"start": v(22.23, -7.14) * mm, "end": v(23.76, -7.14) * mm});
            skLineSegment(sketch, "E309.0.1", {"start": v(23.76, -7.14) * mm, "end": v(23.76, 0) * mm});
            skLineSegment(sketch, "E309.0.2", {"start": v(23.76, 0) * mm, "end": v(22.23, 0) * mm});
            skLineSegment(sketch, "E309.0.3", {"start": v(22.23, 0) * mm, "end": v(22.23, -7.14) * mm});
            skSolve(sketch);
        }
        {
            var Q0;
            Q0=makeQuery(id+"F82.imprint","IMPRINT",FACE,{"disambiguationData":[TD([[makeQuery(id+"F82.imprint","IMPRINT",EDGE,{"derivedFrom":sQuery(id+"F82.wireOp",EDGE,"E306.0.0")}),1.0]])]});
            var Q1;
            Q1=makeQuery(id+"F82.imprint","IMPRINT",FACE,{"disambiguationData":[TD([[makeQuery(id+"F82.imprint","IMPRINT",EDGE,{"derivedFrom":sQuery(id+"F82.wireOp",EDGE,"E307.0.0")}),1.0]])]});
            var Q2;
            Q2=makeQuery(id+"F82.imprint","IMPRINT",FACE,{"disambiguationData":[TD([[makeQuery(id+"F82.imprint","IMPRINT",EDGE,{"derivedFrom":sQuery(id+"F82.wireOp",EDGE,"E308.0.0")}),1.0]])]});
            var Q3;
            Q3=makeQuery(id+"F82.imprint","IMPRINT",FACE,{"disambiguationData":[TD([[makeQuery(id+"F82.imprint","IMPRINT",EDGE,{"derivedFrom":sQuery(id+"F82.wireOp",EDGE,"E309.0.0")}),1.0]])]});
            extrude(context, id + "F83", {"entities" : qUnion([Q0, Q1, Q2, Q3]), "operationType" : NewBodyOperationType.REMOVE, "oppositeDirection" : true, "depth" : 25.4 * mm, "offsetDistance" : 25.4 * mm});
        }
        {
            var Q0;
            {var subQ4=sQuery(id+"F79.wireOp",EDGE,"E301.0.1");Q0=makeQuery(id+"F79.imprint","IMPRINT",FACE,{"disambiguationData":[TD([[makeQuery(id+"F79.imprint","IMPRINT",EDGE,{"derivedFrom":subQ4}),1.0]])]});}
            var sketch = newSketch(context, id + "F84", { "sketchPlane" : qUnion([Q0])});
            skLineSegment(sketch, "E310.0.0", {"start": v(-60.33, -49.72) * mm, "end": v(-60.33, -52.9) * mm});
            skLineSegment(sketch, "E310.0.1", {"start": v(-60.33, -52.9) * mm, "end": v(-22.23, -52.9) * mm});
            skLineSegment(sketch, "E310.0.2", {"start": v(-22.23, -52.9) * mm, "end": v(-23.76, -50.12) * mm});
            skLineSegment(sketch, "E310.0.3", {"start": v(-23.76, -50.12) * mm, "end": v(-23.04, -49.72) * mm});
            skLineSegment(sketch, "E310.0.4", {"start": v(-23.04, -49.72) * mm, "end": v(-60.33, -49.72) * mm});
            skLineSegment(sketch, "E311.0.0", {"start": v(-57.58, -51.3) * mm, "end": v(-73.45, -23.81) * mm});
            skLineSegment(sketch, "E311.0.1", {"start": v(-73.45, -23.81) * mm, "end": v(-76.2, -25.4) * mm});
            skLineSegment(sketch, "E311.0.2", {"start": v(-76.2, -25.4) * mm, "end": v(-60.32, -52.9) * mm});
            skLineSegment(sketch, "E311.0.3", {"start": v(-60.33, -52.9) * mm, "end": v(-57.58, -51.3) * mm});
            skLineSegment(sketch, "E312", {"start": v(-57.58, -49.72) * mm, "end": v(-57.58, -52.9) * mm});
            skSolve(sketch);
        }
        {
            var Q0;
            Q0=makeQuery(id+"F3.opExtrude","SWEPT_FACE",FACE,{"disambiguationData":[OSD([sQuery(id+"F0.wireOp",EDGE,"E7")])]});
            var sketch = newSketch(context, id + "F85", { "sketchPlane" : qUnion([Q0])});
            skLineSegment(sketch, "E313.0.0", {"start": v(23.76, -40.48) * mm, "end": v(23.76, -47.62) * mm});
            skLineSegment(sketch, "E313.0.1", {"start": v(23.76, -47.63) * mm, "end": v(60.32, -47.63) * mm});
            skLineSegment(sketch, "E313.0.2", {"start": v(60.32, -47.63) * mm, "end": v(60.32, 0) * mm});
            skLineSegment(sketch, "E313.0.3", {"start": v(60.32, 0) * mm, "end": v(57.15, 0) * mm});
            skLineSegment(sketch, "E313.0.4", {"start": v(57.15, 0) * mm, "end": v(57.15, 3.18) * mm});
            skLineSegment(sketch, "E313.0.5", {"start": v(57.15, 3.18) * mm, "end": v(50.8, 3.18) * mm});
            skLineSegment(sketch, "E313.0.6", {"start": v(50.8, 3.18) * mm, "end": v(50.8, 0) * mm});
            skLineSegment(sketch, "E313.0.7", {"start": v(50.8, 0) * mm, "end": v(44.45, 0) * mm});
            skLineSegment(sketch, "E313.0.8", {"start": v(44.45, 0) * mm, "end": v(44.45, 3.18) * mm});
            skLineSegment(sketch, "E313.0.9", {"start": v(44.45, 3.18) * mm, "end": v(38.1, 3.18) * mm});
            skLineSegment(sketch, "E313.0.10", {"start": v(38.1, 3.18) * mm, "end": v(38.1, 0) * mm});
            skLineSegment(sketch, "E313.0.11", {"start": v(38.1, 0) * mm, "end": v(31.75, 0) * mm});
            skLineSegment(sketch, "E313.0.12", {"start": v(31.75, 0) * mm, "end": v(31.75, 3.18) * mm});
            skLineSegment(sketch, "E313.0.13", {"start": v(31.75, 3.18) * mm, "end": v(25.4, 3.18) * mm});
            skLineSegment(sketch, "E313.0.14", {"start": v(25.4, 3.18) * mm, "end": v(25.4, 0) * mm});
            skLineSegment(sketch, "E313.0.15", {"start": v(25.4, 0) * mm, "end": v(23.76, 0) * mm});
            skLineSegment(sketch, "E313.0.16", {"start": v(23.76, 0) * mm, "end": v(23.76, -7.14) * mm});
            skLineSegment(sketch, "E313.0.17", {"start": v(60.32, -7.14) * mm, "end": v(22.23, -7.14) * mm});
            skLineSegment(sketch, "E313.0.18", {"start": v(22.23, -7.14) * mm, "end": v(22.23, -13.5) * mm});
            skLineSegment(sketch, "E313.0.19", {"start": v(22.23, -13.5) * mm, "end": v(60.32, -13.5) * mm});
            skLineSegment(sketch, "E313.0.20", {"start": v(23.76, -13.5) * mm, "end": v(23.76, -20.64) * mm});
            skLineSegment(sketch, "E313.0.21", {"start": v(60.32, -20.64) * mm, "end": v(22.23, -20.64) * mm});
            skLineSegment(sketch, "E313.0.22", {"start": v(22.23, -20.64) * mm, "end": v(22.23, -26.99) * mm});
            skLineSegment(sketch, "E313.0.23", {"start": v(22.23, -26.99) * mm, "end": v(60.32, -26.99) * mm});
            skLineSegment(sketch, "E313.0.24", {"start": v(23.76, -26.99) * mm, "end": v(23.76, -34.13) * mm});
            skLineSegment(sketch, "E313.0.25", {"start": v(60.32, -34.13) * mm, "end": v(22.23, -34.13) * mm});
            skLineSegment(sketch, "E313.0.26", {"start": v(22.23, -34.13) * mm, "end": v(22.23, -40.48) * mm});
            skLineSegment(sketch, "E313.0.27", {"start": v(22.23, -40.48) * mm, "end": v(60.32, -40.48) * mm});
            skPoint(sketch, "E314.0", {"position": v(57.58, -47.62) * mm});
            skLineSegment(sketch, "E315", {"start": v(57.58, -47.62) * mm, "end": v(57.58, 0) * mm});
            skSolve(sketch);
        }
        {
            var Q0;
            {var subQ0=sQuery(id+"F85.wireOp",EDGE,"E313.0.25");var subQ1=sQuery(id+"F85.wireOp",EDGE,"E313.0.2");var subQ2=makeQuery(id+"F85.imprint","INTERSECT",VERTEX,{"derivedFrom":[subQ1,subQ0]});Q0=makeQuery(id+"F85.imprint","IMPRINT",FACE,{"disambiguationData":[TD([[makeQuery(id+"F85.imprint","IMPRINT",EDGE,{"disambiguationData":[TD([[subQ2,1.0]])],"derivedFrom":subQ1}),1.0]])]});}
            var Q1;
            {var subQ0=sQuery(id+"F85.wireOp",EDGE,"E313.0.21");var subQ1=sQuery(id+"F85.wireOp",EDGE,"E313.0.2");var subQ2=makeQuery(id+"F85.imprint","INTERSECT",VERTEX,{"derivedFrom":[subQ1,subQ0]});Q1=makeQuery(id+"F85.imprint","IMPRINT",FACE,{"disambiguationData":[TD([[makeQuery(id+"F85.imprint","IMPRINT",EDGE,{"disambiguationData":[TD([[subQ2,1.0]])],"derivedFrom":subQ1}),1.0]])]});}
            var Q2;
            {var subQ0=sQuery(id+"F85.wireOp",EDGE,"E313.0.17");var subQ1=sQuery(id+"F85.wireOp",EDGE,"E313.0.2");var subQ2=makeQuery(id+"F85.imprint","INTERSECT",VERTEX,{"derivedFrom":[subQ1,subQ0]});Q2=makeQuery(id+"F85.imprint","IMPRINT",FACE,{"disambiguationData":[TD([[makeQuery(id+"F85.imprint","IMPRINT",EDGE,{"disambiguationData":[TD([[subQ2,1.0]])],"derivedFrom":subQ1}),1.0]])]});}
            extrude(context, id + "F86", {"entities" : qUnion([Q0, Q1, Q2]), "operationType" : NewBodyOperationType.REMOVE, "oppositeDirection" : true, "depth" : 25.4 * mm, "offsetDistance" : 25.4 * mm});
        }
        {
            var Q0;
            Q0=makeQuery(id+"F4.opExtrude","SWEPT_FACE",FACE,{"disambiguationData":[OSD([sQuery(id+"F0.wireOp",EDGE,"E8")])]});
            var sketch = newSketch(context, id + "F87", { "sketchPlane" : qUnion([Q0])});
            skLineSegment(sketch, "E316.0.0", {"start": v(-12.9, -47.63) * mm, "end": v(-12.9, -40.48) * mm});
            skLineSegment(sketch, "E316.0.1", {"start": v(-12.9, -40.48) * mm, "end": v(-15.65, -40.48) * mm});
            skLineSegment(sketch, "E316.0.2", {"start": v(-15.65, -40.48) * mm, "end": v(-15.65, -47.63) * mm});
            skLineSegment(sketch, "E316.0.3", {"start": v(-15.65, -47.63) * mm, "end": v(-12.9, -47.63) * mm});
            skLineSegment(sketch, "E317.0.0", {"start": v(-15.65, -34.13) * mm, "end": v(-12.9, -34.13) * mm});
            skLineSegment(sketch, "E317.0.1", {"start": v(-12.9, -34.13) * mm, "end": v(-12.9, -26.99) * mm});
            skLineSegment(sketch, "E317.0.2", {"start": v(-12.9, -26.99) * mm, "end": v(-15.65, -26.99) * mm});
            skLineSegment(sketch, "E317.0.3", {"start": v(-15.65, -26.99) * mm, "end": v(-15.65, -34.13) * mm});
            skLineSegment(sketch, "E318.0.0", {"start": v(-15.65, -20.64) * mm, "end": v(-12.9, -20.64) * mm});
            skLineSegment(sketch, "E318.0.1", {"start": v(-12.9, -20.64) * mm, "end": v(-12.9, -13.5) * mm});
            skLineSegment(sketch, "E318.0.2", {"start": v(-12.9, -13.5) * mm, "end": v(-15.65, -13.5) * mm});
            skLineSegment(sketch, "E318.0.3", {"start": v(-15.65, -13.5) * mm, "end": v(-15.65, -20.64) * mm});
            skLineSegment(sketch, "E319.0.0", {"start": v(-15.65, -7.14) * mm, "end": v(-12.9, -7.14) * mm});
            skLineSegment(sketch, "E319.0.1", {"start": v(-12.9, -7.14) * mm, "end": v(-12.9, 0) * mm});
            skLineSegment(sketch, "E319.0.2", {"start": v(-12.9, 0) * mm, "end": v(-15.65, 0) * mm});
            skLineSegment(sketch, "E319.0.3", {"start": v(-15.65, 0) * mm, "end": v(-15.65, -7.14) * mm});
            skSolve(sketch);
        }
        {
            var Q0;
            Q0=makeQuery(id+"F87.imprint","IMPRINT",FACE,{"disambiguationData":[TD([[makeQuery(id+"F87.imprint","IMPRINT",EDGE,{"derivedFrom":sQuery(id+"F87.wireOp",EDGE,"E316.0.0")}),1.0]])]});
            var Q1;
            Q1=makeQuery(id+"F87.imprint","IMPRINT",FACE,{"disambiguationData":[TD([[makeQuery(id+"F87.imprint","IMPRINT",EDGE,{"derivedFrom":sQuery(id+"F87.wireOp",EDGE,"E317.0.0")}),1.0]])]});
            var Q2;
            Q2=makeQuery(id+"F87.imprint","IMPRINT",FACE,{"disambiguationData":[TD([[makeQuery(id+"F87.imprint","IMPRINT",EDGE,{"derivedFrom":sQuery(id+"F87.wireOp",EDGE,"E318.0.0")}),1.0]])]});
            var Q3;
            Q3=makeQuery(id+"F87.imprint","IMPRINT",FACE,{"disambiguationData":[TD([[makeQuery(id+"F87.imprint","IMPRINT",EDGE,{"derivedFrom":sQuery(id+"F87.wireOp",EDGE,"E319.0.0")}),1.0]])]});
            extrude(context, id + "F88", {"entities" : qUnion([Q0, Q1, Q2, Q3]), "operationType" : NewBodyOperationType.REMOVE, "oppositeDirection" : true, "depth" : 25.4 * mm, "offsetDistance" : 25.4 * mm});
        }
        {
            var Q0;
            {var subQ4=sQuery(id+"F84.wireOp",EDGE,"E310.0.0");Q0=makeQuery(id+"F84.imprint","IMPRINT",FACE,{"disambiguationData":[TD([[makeQuery(id+"F84.imprint","IMPRINT",EDGE,{"derivedFrom":subQ4}),-1.0]])]});}
            var sketch = newSketch(context, id + "F89", { "sketchPlane" : qUnion([Q0])});
            skLineSegment(sketch, "E320.0.0", {"start": v(-73.45, -23.81) * mm, "end": v(-76.2, -25.4) * mm});
            skLineSegment(sketch, "E320.0.1", {"start": v(-76.2, -25.4) * mm, "end": v(-60.32, -52.9) * mm});
            skLineSegment(sketch, "E320.0.2", {"start": v(-60.33, -52.9) * mm, "end": v(-60.33, -49.72) * mm});
            skLineSegment(sketch, "E320.0.3", {"start": v(-60.33, -49.72) * mm, "end": v(-58.5, -49.72) * mm});
            skLineSegment(sketch, "E320.0.4", {"start": v(-58.5, -49.72) * mm, "end": v(-73.45, -23.81) * mm});
            skLineSegment(sketch, "E321.0.0", {"start": v(-76.2, -25.4) * mm, "end": v(-73.03, -25.4) * mm});
            skLineSegment(sketch, "E321.0.1", {"start": v(-73.03, -25.4) * mm, "end": v(-73.03, 0) * mm});
            skLineSegment(sketch, "E321.0.2", {"start": v(-73.03, 0) * mm, "end": v(-76.2, 0) * mm});
            skLineSegment(sketch, "E321.0.3", {"start": v(-76.2, 0) * mm, "end": v(-76.2, -25.4) * mm});
            skLineSegment(sketch, "E322", {"start": v(-72.66, -25.19) * mm, "end": v(-75.4, -26.77) * mm});
            skSolve(sketch);
        }
        {
            var Q0;
            Q0=makeQuery(id+"F4.opExtrude","SWEPT_FACE",FACE,{"disambiguationData":[OSD([sQuery(id+"F0.wireOp",EDGE,"E8")])]});
            var sketch = newSketch(context, id + "F90", { "sketchPlane" : qUnion([Q0])});
            skLineSegment(sketch, "E323.0.0", {"start": v(-12.9, -40.48) * mm, "end": v(-12.9, -47.62) * mm});
            skLineSegment(sketch, "E323.0.1", {"start": v(-12.9, -47.63) * mm, "end": v(16.1, -47.63) * mm});
            skLineSegment(sketch, "E323.0.2", {"start": v(16.1, -47.62) * mm, "end": v(16.1, 0) * mm});
            skLineSegment(sketch, "E323.0.3", {"start": v(16.1, 0) * mm, "end": v(12.93, 0) * mm});
            skLineSegment(sketch, "E323.0.4", {"start": v(12.93, 0) * mm, "end": v(12.93, 3.18) * mm});
            skLineSegment(sketch, "E323.0.5", {"start": v(12.93, 3.18) * mm, "end": v(9.42, 3.18) * mm});
            skLineSegment(sketch, "E323.0.6", {"start": v(9.42, 3.18) * mm, "end": v(9.42, 0) * mm});
            skLineSegment(sketch, "E323.0.7", {"start": v(9.42, 0) * mm, "end": v(1.98, 0) * mm});
            skLineSegment(sketch, "E323.0.8", {"start": v(1.98, 0) * mm, "end": v(1.98, 3.18) * mm});
            skLineSegment(sketch, "E323.0.9", {"start": v(1.98, 3.18) * mm, "end": v(-1.53, 3.18) * mm});
            skLineSegment(sketch, "E323.0.10", {"start": v(-1.53, 3.18) * mm, "end": v(-1.53, 0) * mm});
            skLineSegment(sketch, "E323.0.11", {"start": v(-1.53, 0) * mm, "end": v(-8.96, 0) * mm});
            skLineSegment(sketch, "E323.0.12", {"start": v(-8.96, 0) * mm, "end": v(-8.96, 3.18) * mm});
            skLineSegment(sketch, "E323.0.13", {"start": v(-8.96, 3.18) * mm, "end": v(-12.47, 3.18) * mm});
            skLineSegment(sketch, "E323.0.14", {"start": v(-12.47, 3.18) * mm, "end": v(-12.47, 0) * mm});
            skLineSegment(sketch, "E323.0.15", {"start": v(-12.47, 0) * mm, "end": v(-12.9, 0) * mm});
            skLineSegment(sketch, "E323.0.16", {"start": v(-12.9, 0) * mm, "end": v(-12.9, -7.14) * mm});
            skLineSegment(sketch, "E323.0.17", {"start": v(16.1, -7.14) * mm, "end": v(-15.65, -7.14) * mm});
            skLineSegment(sketch, "E323.0.18", {"start": v(-15.65, -7.14) * mm, "end": v(-15.65, -13.5) * mm});
            skLineSegment(sketch, "E323.0.19", {"start": v(-15.65, -13.5) * mm, "end": v(16.1, -13.5) * mm});
            skLineSegment(sketch, "E323.0.20", {"start": v(-12.9, -13.5) * mm, "end": v(-12.9, -20.64) * mm});
            skLineSegment(sketch, "E323.0.21", {"start": v(16.1, -20.64) * mm, "end": v(-15.65, -20.64) * mm});
            skLineSegment(sketch, "E323.0.22", {"start": v(-15.65, -20.64) * mm, "end": v(-15.65, -26.99) * mm});
            skLineSegment(sketch, "E323.0.23", {"start": v(-15.65, -26.99) * mm, "end": v(16.1, -26.99) * mm});
            skLineSegment(sketch, "E323.0.24", {"start": v(-12.9, -26.99) * mm, "end": v(-12.9, -34.13) * mm});
            skLineSegment(sketch, "E323.0.25", {"start": v(16.1, -34.13) * mm, "end": v(-15.65, -34.13) * mm});
            skLineSegment(sketch, "E323.0.26", {"start": v(-15.65, -34.13) * mm, "end": v(-15.65, -40.48) * mm});
            skLineSegment(sketch, "E323.0.27", {"start": v(-15.65, -40.48) * mm, "end": v(16.1, -40.48) * mm});
            skLineSegment(sketch, "E324.0.0", {"start": v(-13.81, -47.63) * mm, "end": v(14.52, -47.63) * mm});
            skLineSegment(sketch, "E324.0.3", {"start": v(14.52, -47.63) * mm, "end": v(-15.65, -47.63) * mm});
            skLineSegment(sketch, "E324.0.4", {"start": v(-15.65, -47.63) * mm, "end": v(-12.9, -47.63) * mm});
            skLineSegment(sketch, "E324.0.5", {"start": v(-12.9, -47.63) * mm, "end": v(-13.81, -47.63) * mm});
            skPoint(sketch, "E325.0", {"position": v(14.52, -47.62) * mm});
            skLineSegment(sketch, "E326", {"start": v(14.52, -47.62) * mm, "end": v(14.52, 0) * mm});
            skSolve(sketch);
        }
        {
            var Q0;
            {var subQ0=sQuery(id+"F90.wireOp",EDGE,"E323.0.27");var subQ1=sQuery(id+"F90.wireOp",EDGE,"E323.0.2");var subQ2=makeQuery(id+"F90.imprint","INTERSECT",VERTEX,{"derivedFrom":[subQ1,subQ0]});Q0=makeQuery(id+"F90.imprint","IMPRINT",FACE,{"disambiguationData":[TD([[makeQuery(id+"F90.imprint","IMPRINT",EDGE,{"disambiguationData":[TD([[subQ2,-1.0]])],"derivedFrom":subQ1}),1.0]])]});}
            var Q1;
            {var subQ0=sQuery(id+"F90.wireOp",EDGE,"E323.0.23");var subQ1=sQuery(id+"F90.wireOp",EDGE,"E323.0.2");var subQ2=makeQuery(id+"F90.imprint","INTERSECT",VERTEX,{"derivedFrom":[subQ1,subQ0]});Q1=makeQuery(id+"F90.imprint","IMPRINT",FACE,{"disambiguationData":[TD([[makeQuery(id+"F90.imprint","IMPRINT",EDGE,{"disambiguationData":[TD([[subQ2,-1.0]])],"derivedFrom":subQ1}),1.0]])]});}
            var Q2;
            {var subQ0=sQuery(id+"F90.wireOp",EDGE,"E323.0.19");var subQ1=sQuery(id+"F90.wireOp",EDGE,"E323.0.2");var subQ2=makeQuery(id+"F90.imprint","INTERSECT",VERTEX,{"derivedFrom":[subQ1,subQ0]});Q2=makeQuery(id+"F90.imprint","IMPRINT",FACE,{"disambiguationData":[TD([[makeQuery(id+"F90.imprint","IMPRINT",EDGE,{"disambiguationData":[TD([[subQ2,-1.0]])],"derivedFrom":subQ1}),1.0]])]});}
            extrude(context, id + "F91", {"entities" : qUnion([Q0, Q1, Q2]), "operationType" : NewBodyOperationType.REMOVE, "oppositeDirection" : true, "depth" : 25.4 * mm, "offsetDistance" : 25.4 * mm});
        }
        {
            var Q0;
            Q0=makeQuery(id+"F5.opExtrude","SWEPT_FACE",FACE,{"disambiguationData":[OSD([sQuery(id+"F0.wireOp",EDGE,"E9")])]});
            var sketch = newSketch(context, id + "F92", { "sketchPlane" : qUnion([Q0])});
            skLineSegment(sketch, "E327.0.0", {"start": v(-23.81, -47.62) * mm, "end": v(-23.81, -40.48) * mm});
            skLineSegment(sketch, "E327.0.1", {"start": v(-23.81, -40.48) * mm, "end": v(-25.4, -40.48) * mm});
            skLineSegment(sketch, "E327.0.2", {"start": v(-25.4, -40.48) * mm, "end": v(-25.4, -47.62) * mm});
            skLineSegment(sketch, "E327.0.3", {"start": v(-25.4, -47.63) * mm, "end": v(-23.81, -47.63) * mm});
            skLineSegment(sketch, "E328.0.0", {"start": v(-25.4, -34.13) * mm, "end": v(-23.81, -34.13) * mm});
            skLineSegment(sketch, "E328.0.1", {"start": v(-23.81, -34.13) * mm, "end": v(-23.81, -26.99) * mm});
            skLineSegment(sketch, "E328.0.2", {"start": v(-23.81, -26.99) * mm, "end": v(-25.4, -26.99) * mm});
            skLineSegment(sketch, "E328.0.3", {"start": v(-25.4, -26.99) * mm, "end": v(-25.4, -34.13) * mm});
            skLineSegment(sketch, "E329.0.0", {"start": v(-25.4, -20.64) * mm, "end": v(-23.81, -20.64) * mm});
            skLineSegment(sketch, "E329.0.1", {"start": v(-23.81, -20.64) * mm, "end": v(-23.81, -13.5) * mm});
            skLineSegment(sketch, "E329.0.2", {"start": v(-23.81, -13.5) * mm, "end": v(-25.4, -13.5) * mm});
            skLineSegment(sketch, "E329.0.3", {"start": v(-25.4, -13.5) * mm, "end": v(-25.4, -20.64) * mm});
            skLineSegment(sketch, "E330.0.0", {"start": v(-25.4, -7.14) * mm, "end": v(-23.81, -7.14) * mm});
            skLineSegment(sketch, "E330.0.1", {"start": v(-23.81, -7.14) * mm, "end": v(-23.81, 0) * mm});
            skLineSegment(sketch, "E330.0.2", {"start": v(-23.81, 0) * mm, "end": v(-25.4, 0) * mm});
            skLineSegment(sketch, "E330.0.3", {"start": v(-25.4, 0) * mm, "end": v(-25.4, -7.14) * mm});
            skSolve(sketch);
        }
        {
            var Q0;
            Q0=makeQuery(id+"F92.imprint","IMPRINT",FACE,{"disambiguationData":[TD([[makeQuery(id+"F92.imprint","IMPRINT",EDGE,{"derivedFrom":sQuery(id+"F92.wireOp",EDGE,"E327.0.0")}),1.0]])]});
            var Q1;
            Q1=makeQuery(id+"F92.imprint","IMPRINT",FACE,{"disambiguationData":[TD([[makeQuery(id+"F92.imprint","IMPRINT",EDGE,{"derivedFrom":sQuery(id+"F92.wireOp",EDGE,"E328.0.0")}),1.0]])]});
            var Q2;
            Q2=makeQuery(id+"F92.imprint","IMPRINT",FACE,{"disambiguationData":[TD([[makeQuery(id+"F92.imprint","IMPRINT",EDGE,{"derivedFrom":sQuery(id+"F92.wireOp",EDGE,"E329.0.0")}),1.0]])]});
            var Q3;
            Q3=makeQuery(id+"F92.imprint","IMPRINT",FACE,{"disambiguationData":[TD([[makeQuery(id+"F92.imprint","IMPRINT",EDGE,{"derivedFrom":sQuery(id+"F92.wireOp",EDGE,"E330.0.0")}),1.0]])]});
            extrude(context, id + "F93", {"entities" : qUnion([Q0, Q1, Q2, Q3]), "operationType" : NewBodyOperationType.REMOVE, "oppositeDirection" : true, "depth" : 25.4 * mm, "offsetDistance" : 25.4 * mm});
        }
        {
            var Q0;
            {var subQ1=sQuery(id+"F89.wireOp",EDGE,"E320.0.0");Q0=makeQuery(id+"F89.imprint","IMPRINT",FACE,{"disambiguationData":[TD([[makeQuery(id+"F89.imprint","IMPRINT",EDGE,{"derivedFrom":subQ1}),-1.0]])]});}
            var sketch = newSketch(context, id + "F94", { "sketchPlane" : qUnion([Q0])});
            skLineSegment(sketch, "E331.0.0", {"start": v(-73.03, 0) * mm, "end": v(-76.2, 0) * mm});
            skLineSegment(sketch, "E331.0.1", {"start": v(-76.2, 0) * mm, "end": v(-76.2, -25.4) * mm});
            skLineSegment(sketch, "E331.0.2", {"start": v(-76.2, -25.4) * mm, "end": v(-73.45, -23.81) * mm});
            skLineSegment(sketch, "E331.0.3", {"start": v(-73.45, -23.81) * mm, "end": v(-73.03, -24.55) * mm});
            skLineSegment(sketch, "E331.0.4", {"start": v(-73.03, -24.55) * mm, "end": v(-73.03, 0) * mm});
            skLineSegment(sketch, "E332.0.0", {"start": v(0, 77.54) * mm, "end": v(-76.2, 0) * mm});
            skLineSegment(sketch, "E332.0.1", {"start": v(-76.2, 0) * mm, "end": v(-73.94, -2.23) * mm});
            skLineSegment(sketch, "E332.0.2", {"start": v(-73.94, -2.23) * mm, "end": v(2.23, 75.28) * mm});
            skLineSegment(sketch, "E332.0.3", {"start": v(2.23, 75.28) * mm, "end": v(0, 77.54) * mm});
            skLineSegment(sketch, "E333", {"start": v(-73.03, -2.23) * mm, "end": v(-76.2, -2.23) * mm});
            skSolve(sketch);
        }
        {
            var Q0;
            Q0=makeQuery(id+"F5.opExtrude","SWEPT_FACE",FACE,{"disambiguationData":[OSD([sQuery(id+"F0.wireOp",EDGE,"E9")])]});
            var sketch = newSketch(context, id + "F95", { "sketchPlane" : qUnion([Q0])});
            skLineSegment(sketch, "E334.0.0", {"start": v(-23.81, -40.48) * mm, "end": v(-23.81, -47.62) * mm});
            skLineSegment(sketch, "E334.0.1", {"start": v(-23.81, -47.63) * mm, "end": v(0, -47.63) * mm});
            skLineSegment(sketch, "E334.0.2", {"start": v(0, -47.62) * mm, "end": v(0, 0) * mm});
            skLineSegment(sketch, "E334.0.3", {"start": v(0, 0) * mm, "end": v(-3.17, 0) * mm});
            skLineSegment(sketch, "E334.0.4", {"start": v(-3.17, 0) * mm, "end": v(-3.17, 3.18) * mm});
            skLineSegment(sketch, "E334.0.5", {"start": v(-3.17, 3.18) * mm, "end": v(-8.22, 3.18) * mm});
            skLineSegment(sketch, "E334.0.6", {"start": v(-8.22, 3.18) * mm, "end": v(-8.22, 0) * mm});
            skLineSegment(sketch, "E334.0.7", {"start": v(-8.22, 0) * mm, "end": v(-10.18, 0) * mm});
            skLineSegment(sketch, "E334.0.8", {"start": v(-10.18, 0) * mm, "end": v(-10.18, 3.18) * mm});
            skLineSegment(sketch, "E334.0.9", {"start": v(-10.18, 3.18) * mm, "end": v(-15.22, 3.18) * mm});
            skLineSegment(sketch, "E334.0.10", {"start": v(-15.22, 3.18) * mm, "end": v(-15.22, 0) * mm});
            skLineSegment(sketch, "E334.0.11", {"start": v(-15.22, 0) * mm, "end": v(-17.18, 0) * mm});
            skLineSegment(sketch, "E334.0.12", {"start": v(-17.18, 0) * mm, "end": v(-17.18, 3.18) * mm});
            skLineSegment(sketch, "E334.0.13", {"start": v(-17.18, 3.18) * mm, "end": v(-22.22, 3.18) * mm});
            skLineSegment(sketch, "E334.0.14", {"start": v(-22.22, 3.18) * mm, "end": v(-22.22, 0) * mm});
            skLineSegment(sketch, "E334.0.15", {"start": v(-22.22, 0) * mm, "end": v(-23.81, 0) * mm});
            skLineSegment(sketch, "E334.0.16", {"start": v(-23.81, 0) * mm, "end": v(-23.81, -7.14) * mm});
            skLineSegment(sketch, "E334.0.17", {"start": v(0, -7.14) * mm, "end": v(-25.4, -7.14) * mm});
            skLineSegment(sketch, "E334.0.18", {"start": v(-25.4, -7.14) * mm, "end": v(-25.4, -13.5) * mm});
            skLineSegment(sketch, "E334.0.19", {"start": v(-25.4, -13.5) * mm, "end": v(0, -13.5) * mm});
            skLineSegment(sketch, "E334.0.20", {"start": v(-23.81, -13.5) * mm, "end": v(-23.81, -20.64) * mm});
            skLineSegment(sketch, "E334.0.21", {"start": v(0, -20.64) * mm, "end": v(-25.4, -20.64) * mm});
            skLineSegment(sketch, "E334.0.22", {"start": v(-25.4, -20.64) * mm, "end": v(-25.4, -26.99) * mm});
            skLineSegment(sketch, "E334.0.23", {"start": v(-25.4, -26.99) * mm, "end": v(0, -26.99) * mm});
            skLineSegment(sketch, "E334.0.24", {"start": v(-23.81, -26.99) * mm, "end": v(-23.81, -34.13) * mm});
            skLineSegment(sketch, "E334.0.25", {"start": v(0, -34.13) * mm, "end": v(-25.4, -34.13) * mm});
            skLineSegment(sketch, "E334.0.26", {"start": v(-25.4, -34.13) * mm, "end": v(-25.4, -40.48) * mm});
            skLineSegment(sketch, "E334.0.27", {"start": v(-25.4, -40.48) * mm, "end": v(0, -40.48) * mm});
            skPoint(sketch, "E335.0", {"position": v(-2.23, -47.62) * mm});
            skLineSegment(sketch, "E336", {"start": v(-2.23, -47.62) * mm, "end": v(-2.23, 7.97) * mm});
            skSolve(sketch);
        }
        {
            var Q0;
            {var subQ0=sQuery(id+"F95.wireOp",EDGE,"E334.0.27");var subQ1=sQuery(id+"F95.wireOp",EDGE,"E334.0.2");var subQ2=makeQuery(id+"F95.imprint","INTERSECT",VERTEX,{"derivedFrom":[subQ1,subQ0]});Q0=makeQuery(id+"F95.imprint","IMPRINT",FACE,{"disambiguationData":[TD([[makeQuery(id+"F95.imprint","IMPRINT",EDGE,{"disambiguationData":[TD([[subQ2,-1.0]])],"derivedFrom":subQ1}),1.0]])]});}
            var Q1;
            {var subQ0=sQuery(id+"F95.wireOp",EDGE,"E334.0.23");var subQ1=sQuery(id+"F95.wireOp",EDGE,"E334.0.2");var subQ2=makeQuery(id+"F95.imprint","INTERSECT",VERTEX,{"derivedFrom":[subQ1,subQ0]});Q1=makeQuery(id+"F95.imprint","IMPRINT",FACE,{"disambiguationData":[TD([[makeQuery(id+"F95.imprint","IMPRINT",EDGE,{"disambiguationData":[TD([[subQ2,-1.0]])],"derivedFrom":subQ1}),1.0]])]});}
            var Q2;
            {var subQ0=sQuery(id+"F95.wireOp",EDGE,"E334.0.19");var subQ1=sQuery(id+"F95.wireOp",EDGE,"E334.0.2");var subQ2=makeQuery(id+"F95.imprint","INTERSECT",VERTEX,{"derivedFrom":[subQ1,subQ0]});Q2=makeQuery(id+"F95.imprint","IMPRINT",FACE,{"disambiguationData":[TD([[makeQuery(id+"F95.imprint","IMPRINT",EDGE,{"disambiguationData":[TD([[subQ2,-1.0]])],"derivedFrom":subQ1}),1.0]])]});}
            extrude(context, id + "F96", {"entities" : qUnion([Q0, Q1, Q2]), "operationType" : NewBodyOperationType.REMOVE, "oppositeDirection" : true, "depth" : 25.4 * mm, "offsetDistance" : 25.4 * mm});
        }
        {
            var Q0;
            Q0=makeQuery(id+"F6.opExtrude","SWEPT_FACE",FACE,{"disambiguationData":[OSD([sQuery(id+"F0.wireOp",EDGE,"E0")])]});
            var sketch = newSketch(context, id + "F97", { "sketchPlane" : qUnion([Q0])});
            skLineSegment(sketch, "E337.0.0", {"start": v(-51.18, -47.62) * mm, "end": v(-51.18, -40.48) * mm});
            skLineSegment(sketch, "E337.0.1", {"start": v(-51.18, -40.48) * mm, "end": v(-53.4, -40.48) * mm});
            skLineSegment(sketch, "E337.0.2", {"start": v(-53.4, -40.48) * mm, "end": v(-53.4, -47.62) * mm});
            skLineSegment(sketch, "E337.0.3", {"start": v(-53.4, -47.63) * mm, "end": v(-51.18, -47.63) * mm});
            skLineSegment(sketch, "E338.0.0", {"start": v(-53.4, -34.13) * mm, "end": v(-51.18, -34.13) * mm});
            skLineSegment(sketch, "E338.0.1", {"start": v(-51.18, -34.13) * mm, "end": v(-51.18, -26.99) * mm});
            skLineSegment(sketch, "E338.0.2", {"start": v(-51.18, -26.99) * mm, "end": v(-53.4, -26.99) * mm});
            skLineSegment(sketch, "E338.0.3", {"start": v(-53.4, -26.99) * mm, "end": v(-53.4, -34.13) * mm});
            skLineSegment(sketch, "E339.0.0", {"start": v(-53.4, -20.64) * mm, "end": v(-51.18, -20.64) * mm});
            skLineSegment(sketch, "E339.0.1", {"start": v(-51.18, -20.64) * mm, "end": v(-51.18, -13.5) * mm});
            skLineSegment(sketch, "E339.0.2", {"start": v(-51.18, -13.5) * mm, "end": v(-53.4, -13.5) * mm});
            skLineSegment(sketch, "E339.0.3", {"start": v(-53.4, -13.5) * mm, "end": v(-53.4, -20.64) * mm});
            skLineSegment(sketch, "E340.0.0", {"start": v(-53.4, -7.14) * mm, "end": v(-51.18, -7.14) * mm});
            skLineSegment(sketch, "E340.0.1", {"start": v(-51.18, -7.14) * mm, "end": v(-51.18, 0) * mm});
            skLineSegment(sketch, "E340.0.2", {"start": v(-51.18, 0) * mm, "end": v(-53.4, 0) * mm});
            skLineSegment(sketch, "E340.0.3", {"start": v(-53.4, 0) * mm, "end": v(-53.4, -7.14) * mm});
            skSolve(sketch);
        }
        {
            var Q0;
            Q0=makeQuery(id+"F97.imprint","IMPRINT",FACE,{"disambiguationData":[TD([[makeQuery(id+"F97.imprint","IMPRINT",EDGE,{"derivedFrom":sQuery(id+"F97.wireOp",EDGE,"E337.0.0")}),1.0]])]});
            var Q1;
            Q1=makeQuery(id+"F97.imprint","IMPRINT",FACE,{"disambiguationData":[TD([[makeQuery(id+"F97.imprint","IMPRINT",EDGE,{"derivedFrom":sQuery(id+"F97.wireOp",EDGE,"E338.0.0")}),1.0]])]});
            var Q2;
            Q2=makeQuery(id+"F97.imprint","IMPRINT",FACE,{"disambiguationData":[TD([[makeQuery(id+"F97.imprint","IMPRINT",EDGE,{"derivedFrom":sQuery(id+"F97.wireOp",EDGE,"E339.0.0")}),1.0]])]});
            var Q3;
            Q3=makeQuery(id+"F97.imprint","IMPRINT",FACE,{"disambiguationData":[TD([[makeQuery(id+"F97.imprint","IMPRINT",EDGE,{"derivedFrom":sQuery(id+"F97.wireOp",EDGE,"E340.0.0")}),1.0]])]});
            extrude(context, id + "F98", {"entities" : qUnion([Q0, Q1, Q2, Q3]), "operationType" : NewBodyOperationType.REMOVE, "oppositeDirection" : true, "depth" : 25.4 * mm, "offsetDistance" : 25.4 * mm});
        }
        {
            var Q0;
            {var subQ0=sQuery(id+"F2.wireOp",EDGE,"E43");var subQ1=sQuery(id+"F2.wireOp",EDGE,"E29");var subQ2=sQuery(id+"F2.wireOp",EDGE,"E44");var subQ3=sQuery(id+"F2.wireOp",EDGE,"E45");var subQ4=sQuery(id+"F0.wireOp",EDGE,"E5");Q0=makeQuery(id+"F44.boolean.opBoolean","SPLIT",FACE,{"disambiguationData":[TD([makeQuery(id+"F11.opExtrude","SWEPT_FACE",FACE,{"disambiguationData":[OSD([subQ2])]})])],"derivedFrom":makeQuery(id+"F11.opExtrude","CAP_FACE",FACE,{"disambiguationData":[OSD([subQ4,subQ1,sQuery(id+"F2.wireOp",EDGE,"E30"),subQ0,subQ2,subQ3])],"isStart":true})});}
            var sketch = newSketch(context, id + "F99", { "sketchPlane" : qUnion([Q0])});
            skLineSegment(sketch, "E341.0.0", {"start": v(0, 36.97) * mm, "end": v(1.54, 37.82) * mm});
            skLineSegment(sketch, "E341.0.1", {"start": v(1.54, 37.82) * mm, "end": v(0, 40.6) * mm});
            skLineSegment(sketch, "E341.0.2", {"start": v(0, 40.6) * mm, "end": v(-1.54, 39.75) * mm});
            skLineSegment(sketch, "E341.0.3", {"start": v(-1.54, 39.75) * mm, "end": v(0, 36.97) * mm});
            skSolve(sketch);
        }
        {
            var Q0;
            Q0 = qSketchRegion(id + "F99", true);
            var Q1;
            Q1=makeQuery(id+"F44.boolean.opBoolean","COPY",FACE,{"derivedFrom":makeQuery(id+"F44.opExtrude","SWEPT_FACE",FACE,{"disambiguationData":[OSD([sQuery(id+"F43.wireOp",EDGE,"E209.0.1")])]})});
            extrude(context, id + "F100", {"entities" : qUnion([Q0]), "operationType" : NewBodyOperationType.REMOVE, "endBound" : BoundingType.UP_TO_SURFACE, "oppositeDirection" : true, "depth" : 25.4 * mm, "endBoundEntityFace" : qUnion([Q1]), "offsetDistance" : 25.4 * mm});
        }
    });
